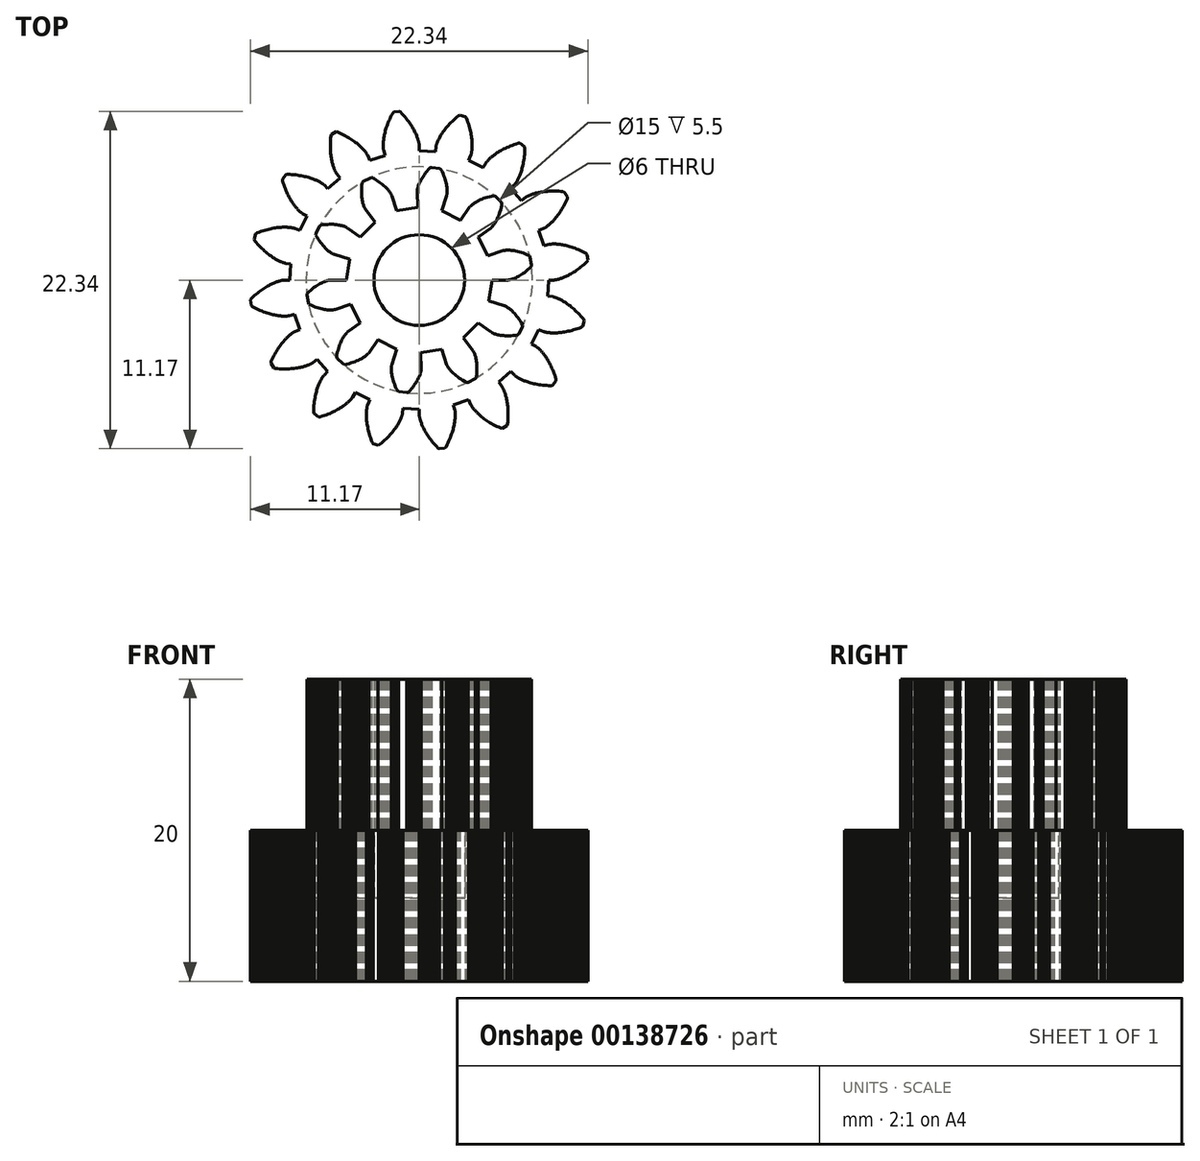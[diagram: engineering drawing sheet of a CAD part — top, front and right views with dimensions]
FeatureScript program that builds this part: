
annotation { "Feature Type Name" : "Feature", "Feature Type Description" : "" }
export const myFeature = defineFeature(function(context is Context, id is Id, definition is map)
    precondition{}
    {
        {
            var Q0;
            Q0=qCreatedBy(makeId("Top.planeOp"),FACE);
            var sketch = newSketch(context, id + "F0", { "sketchPlane" : qUnion([Q0])});
            skLineSegment(sketch, "E0", {"start": v(8.56, 0) * mm, "end": v(8.91, 0) * mm});
            skLineSegment(sketch, "E1", {"start": v(8.91, 0) * mm, "end": v(8.92, 0) * mm});
            skLineSegment(sketch, "E2", {"start": v(8.92, 0) * mm, "end": v(8.93, 0) * mm});
            skLineSegment(sketch, "E3", {"start": v(8.93, 0) * mm, "end": v(8.94, 0) * mm});
            skLineSegment(sketch, "E4", {"start": v(8.94, 0) * mm, "end": v(8.96, 0) * mm});
            skLineSegment(sketch, "E5", {"start": v(8.96, 0) * mm, "end": v(8.98, 0) * mm});
            skLineSegment(sketch, "E6", {"start": v(8.98, 0) * mm, "end": v(9, 0) * mm});
            skLineSegment(sketch, "E7", {"start": v(9, 0) * mm, "end": v(9.04, 0.01) * mm});
            skLineSegment(sketch, "E8", {"start": v(9.04, 0.01) * mm, "end": v(9.07, 0.02) * mm});
            skLineSegment(sketch, "E9", {"start": v(9.07, 0.02) * mm, "end": v(9.11, 0.03) * mm});
            skLineSegment(sketch, "E10", {"start": v(9.11, 0.03) * mm, "end": v(9.15, 0.04) * mm});
            skLineSegment(sketch, "E11", {"start": v(9.15, 0.04) * mm, "end": v(9.2, 0.05) * mm});
            skLineSegment(sketch, "E12", {"start": v(9.2, 0.05) * mm, "end": v(9.25, 0.06) * mm});
            skLineSegment(sketch, "E13", {"start": v(9.25, 0.06) * mm, "end": v(9.3, 0.08) * mm});
            skLineSegment(sketch, "E14", {"start": v(9.3, 0.08) * mm, "end": v(9.36, 0.1) * mm});
            skLineSegment(sketch, "E15", {"start": v(9.36, 0.1) * mm, "end": v(9.42, 0.12) * mm});
            skLineSegment(sketch, "E16", {"start": v(9.42, 0.12) * mm, "end": v(9.49, 0.14) * mm});
            skLineSegment(sketch, "E17", {"start": v(9.49, 0.14) * mm, "end": v(9.56, 0.17) * mm});
            skLineSegment(sketch, "E18", {"start": v(9.56, 0.17) * mm, "end": v(9.63, 0.2) * mm});
            skLineSegment(sketch, "E19", {"start": v(9.63, 0.2) * mm, "end": v(9.7, 0.23) * mm});
            skLineSegment(sketch, "E20", {"start": v(9.7, 0.23) * mm, "end": v(9.78, 0.27) * mm});
            skLineSegment(sketch, "E21", {"start": v(9.78, 0.27) * mm, "end": v(9.86, 0.31) * mm});
            skLineSegment(sketch, "E22", {"start": v(9.86, 0.31) * mm, "end": v(9.95, 0.36) * mm});
            skLineSegment(sketch, "E23", {"start": v(9.95, 0.36) * mm, "end": v(10.03, 0.4) * mm});
            skLineSegment(sketch, "E24", {"start": v(10.03, 0.4) * mm, "end": v(10.12, 0.46) * mm});
            skLineSegment(sketch, "E25", {"start": v(10.12, 0.46) * mm, "end": v(10.21, 0.51) * mm});
            skLineSegment(sketch, "E26", {"start": v(10.21, 0.51) * mm, "end": v(10.3, 0.57) * mm});
            skLineSegment(sketch, "E27", {"start": v(10.3, 0.57) * mm, "end": v(10.4, 0.64) * mm});
            skLineSegment(sketch, "E28", {"start": v(10.4, 0.64) * mm, "end": v(10.5, 0.7) * mm});
            skLineSegment(sketch, "E29", {"start": v(10.5, 0.7) * mm, "end": v(10.6, 0.78) * mm});
            skLineSegment(sketch, "E30", {"start": v(10.6, 0.78) * mm, "end": v(10.7, 0.86) * mm});
            skLineSegment(sketch, "E31", {"start": v(10.7, 0.86) * mm, "end": v(10.8, 0.94) * mm});
            skLineSegment(sketch, "E32", {"start": v(10.8, 0.94) * mm, "end": v(10.9, 1.03) * mm});
            skLineSegment(sketch, "E33", {"start": v(10.9, 1.03) * mm, "end": v(11.01, 1.13) * mm});
            skLineSegment(sketch, "E34", {"start": v(11.01, 1.13) * mm, "end": v(11.12, 1.23) * mm});
            skLineSegment(sketch, "E35", {"start": v(11.12, 1.23) * mm, "end": v(11.17, 1.32) * mm});
            skLineSegment(sketch, "E36", {"start": v(11.17, 1.32) * mm, "end": v(11.12, 1.68) * mm});
            skLineSegment(sketch, "E37", {"start": v(11.12, 1.68) * mm, "end": v(11.05, 1.76) * mm});
            skLineSegment(sketch, "E38", {"start": v(11.05, 1.76) * mm, "end": v(10.92, 1.83) * mm});
            skLineSegment(sketch, "E39", {"start": v(10.92, 1.83) * mm, "end": v(10.8, 1.9) * mm});
            skLineSegment(sketch, "E40", {"start": v(10.8, 1.9) * mm, "end": v(10.67, 1.95) * mm});
            skLineSegment(sketch, "E41", {"start": v(10.67, 1.95) * mm, "end": v(10.55, 2) * mm});
            skLineSegment(sketch, "E42", {"start": v(10.55, 2) * mm, "end": v(10.43, 2.05) * mm});
            skLineSegment(sketch, "E43", {"start": v(10.43, 2.05) * mm, "end": v(10.31, 2.1) * mm});
            skLineSegment(sketch, "E44", {"start": v(10.31, 2.1) * mm, "end": v(10.2, 2.14) * mm});
            skLineSegment(sketch, "E45", {"start": v(10.2, 2.14) * mm, "end": v(10.09, 2.18) * mm});
            skLineSegment(sketch, "E46", {"start": v(10.09, 2.18) * mm, "end": v(9.98, 2.2) * mm});
            skLineSegment(sketch, "E47", {"start": v(9.98, 2.2) * mm, "end": v(9.88, 2.24) * mm});
            skLineSegment(sketch, "E48", {"start": v(9.88, 2.24) * mm, "end": v(9.78, 2.27) * mm});
            skLineSegment(sketch, "E49", {"start": v(9.78, 2.27) * mm, "end": v(9.68, 2.29) * mm});
            skLineSegment(sketch, "E50", {"start": v(9.68, 2.29) * mm, "end": v(9.6, 2.31) * mm});
            skLineSegment(sketch, "E51", {"start": v(9.6, 2.31) * mm, "end": v(9.5, 2.33) * mm});
            skLineSegment(sketch, "E52", {"start": v(9.5, 2.33) * mm, "end": v(9.42, 2.34) * mm});
            skLineSegment(sketch, "E53", {"start": v(9.42, 2.34) * mm, "end": v(9.34, 2.36) * mm});
            skLineSegment(sketch, "E54", {"start": v(9.34, 2.36) * mm, "end": v(9.26, 2.37) * mm});
            skLineSegment(sketch, "E55", {"start": v(9.26, 2.37) * mm, "end": v(9.19, 2.37) * mm});
            skLineSegment(sketch, "E56", {"start": v(9.19, 2.37) * mm, "end": v(9.12, 2.38) * mm});
            skLineSegment(sketch, "E57", {"start": v(9.12, 2.38) * mm, "end": v(9.05, 2.38) * mm});
            skLineSegment(sketch, "E58", {"start": v(9.05, 2.38) * mm, "end": v(9, 2.39) * mm});
            skLineSegment(sketch, "E59", {"start": v(9, 2.39) * mm, "end": v(8.94, 2.39) * mm});
            skLineSegment(sketch, "E60", {"start": v(8.94, 2.39) * mm, "end": v(8.89, 2.39) * mm});
            skLineSegment(sketch, "E61", {"start": v(8.89, 2.39) * mm, "end": v(8.84, 2.39) * mm});
            skLineSegment(sketch, "E62", {"start": v(8.84, 2.39) * mm, "end": v(8.8, 2.39) * mm});
            skLineSegment(sketch, "E63", {"start": v(8.8, 2.39) * mm, "end": v(8.75, 2.38) * mm});
            skLineSegment(sketch, "E64", {"start": v(8.75, 2.38) * mm, "end": v(8.72, 2.38) * mm});
            skLineSegment(sketch, "E65", {"start": v(8.72, 2.38) * mm, "end": v(8.69, 2.38) * mm});
            skLineSegment(sketch, "E66", {"start": v(8.69, 2.38) * mm, "end": v(8.66, 2.37) * mm});
            skLineSegment(sketch, "E67", {"start": v(8.66, 2.37) * mm, "end": v(8.64, 2.37) * mm});
            skLineSegment(sketch, "E68", {"start": v(8.64, 2.37) * mm, "end": v(8.62, 2.37) * mm});
            skLineSegment(sketch, "E69", {"start": v(8.62, 2.37) * mm, "end": v(8.6, 2.36) * mm});
            skLineSegment(sketch, "E70", {"start": v(8.6, 2.36) * mm, "end": v(8.6, 2.36) * mm});
            skLineSegment(sketch, "E71", {"start": v(8.6, 2.36) * mm, "end": v(8.26, 2.27) * mm});
            skLineSegment(sketch, "E72", {"start": v(8.26, 2.27) * mm, "end": v(7.91, 3.28) * mm});
            skLineSegment(sketch, "E73", {"start": v(7.91, 3.28) * mm, "end": v(8.23, 3.41) * mm});
            skLineSegment(sketch, "E74", {"start": v(8.23, 3.41) * mm, "end": v(8.24, 3.41) * mm});
            skLineSegment(sketch, "E75", {"start": v(8.24, 3.41) * mm, "end": v(8.25, 3.42) * mm});
            skLineSegment(sketch, "E76", {"start": v(8.25, 3.42) * mm, "end": v(8.26, 3.42) * mm});
            skLineSegment(sketch, "E77", {"start": v(8.26, 3.42) * mm, "end": v(8.28, 3.43) * mm});
            skLineSegment(sketch, "E78", {"start": v(8.28, 3.43) * mm, "end": v(8.3, 3.44) * mm});
            skLineSegment(sketch, "E79", {"start": v(8.3, 3.44) * mm, "end": v(8.32, 3.46) * mm});
            skLineSegment(sketch, "E80", {"start": v(8.32, 3.46) * mm, "end": v(8.34, 3.47) * mm});
            skLineSegment(sketch, "E81", {"start": v(8.34, 3.47) * mm, "end": v(8.37, 3.5) * mm});
            skLineSegment(sketch, "E82", {"start": v(8.37, 3.5) * mm, "end": v(8.4, 3.51) * mm});
            skLineSegment(sketch, "E83", {"start": v(8.4, 3.51) * mm, "end": v(8.44, 3.54) * mm});
            skLineSegment(sketch, "E84", {"start": v(8.44, 3.54) * mm, "end": v(8.48, 3.57) * mm});
            skLineSegment(sketch, "E85", {"start": v(8.48, 3.57) * mm, "end": v(8.52, 3.6) * mm});
            skLineSegment(sketch, "E86", {"start": v(8.52, 3.6) * mm, "end": v(8.57, 3.63) * mm});
            skLineSegment(sketch, "E87", {"start": v(8.57, 3.63) * mm, "end": v(8.61, 3.67) * mm});
            skLineSegment(sketch, "E88", {"start": v(8.61, 3.67) * mm, "end": v(8.66, 3.72) * mm});
            skLineSegment(sketch, "E89", {"start": v(8.66, 3.72) * mm, "end": v(8.71, 3.76) * mm});
            skLineSegment(sketch, "E90", {"start": v(8.71, 3.76) * mm, "end": v(8.76, 3.82) * mm});
            skLineSegment(sketch, "E91", {"start": v(8.76, 3.82) * mm, "end": v(8.82, 3.87) * mm});
            skLineSegment(sketch, "E92", {"start": v(8.82, 3.87) * mm, "end": v(8.87, 3.93) * mm});
            skLineSegment(sketch, "E93", {"start": v(8.87, 3.93) * mm, "end": v(8.93, 4) * mm});
            skLineSegment(sketch, "E94", {"start": v(8.93, 4) * mm, "end": v(9, 4.06) * mm});
            skLineSegment(sketch, "E95", {"start": v(9, 4.06) * mm, "end": v(9.05, 4.14) * mm});
            skLineSegment(sketch, "E96", {"start": v(9.05, 4.14) * mm, "end": v(9.11, 4.21) * mm});
            skLineSegment(sketch, "E97", {"start": v(9.11, 4.21) * mm, "end": v(9.18, 4.3) * mm});
            skLineSegment(sketch, "E98", {"start": v(9.18, 4.3) * mm, "end": v(9.24, 4.38) * mm});
            skLineSegment(sketch, "E99", {"start": v(9.24, 4.38) * mm, "end": v(9.3, 4.47) * mm});
            skLineSegment(sketch, "E100", {"start": v(9.3, 4.47) * mm, "end": v(9.37, 4.57) * mm});
            skLineSegment(sketch, "E101", {"start": v(9.37, 4.57) * mm, "end": v(9.43, 4.67) * mm});
            skLineSegment(sketch, "E102", {"start": v(9.43, 4.67) * mm, "end": v(9.5, 4.78) * mm});
            skLineSegment(sketch, "E103", {"start": v(9.5, 4.78) * mm, "end": v(9.56, 4.9) * mm});
            skLineSegment(sketch, "E104", {"start": v(9.56, 4.9) * mm, "end": v(9.62, 5) * mm});
            skLineSegment(sketch, "E105", {"start": v(9.62, 5) * mm, "end": v(9.68, 5.13) * mm});
            skLineSegment(sketch, "E106", {"start": v(9.68, 5.13) * mm, "end": v(9.74, 5.26) * mm});
            skLineSegment(sketch, "E107", {"start": v(9.74, 5.26) * mm, "end": v(9.8, 5.39) * mm});
            skLineSegment(sketch, "E108", {"start": v(9.8, 5.39) * mm, "end": v(9.81, 5.5) * mm});
            skLineSegment(sketch, "E109", {"start": v(9.81, 5.5) * mm, "end": v(9.63, 5.81) * mm});
            skLineSegment(sketch, "E110", {"start": v(9.63, 5.81) * mm, "end": v(9.53, 5.86) * mm});
            skLineSegment(sketch, "E111", {"start": v(9.53, 5.86) * mm, "end": v(9.39, 5.87) * mm});
            skLineSegment(sketch, "E112", {"start": v(9.39, 5.87) * mm, "end": v(9.25, 5.88) * mm});
            skLineSegment(sketch, "E113", {"start": v(9.25, 5.88) * mm, "end": v(9.1, 5.88) * mm});
            skLineSegment(sketch, "E114", {"start": v(9.1, 5.88) * mm, "end": v(8.98, 5.89) * mm});
            skLineSegment(sketch, "E115", {"start": v(8.98, 5.89) * mm, "end": v(8.85, 5.89) * mm});
            skLineSegment(sketch, "E116", {"start": v(8.85, 5.89) * mm, "end": v(8.72, 5.88) * mm});
            skLineSegment(sketch, "E117", {"start": v(8.72, 5.88) * mm, "end": v(8.6, 5.88) * mm});
            skLineSegment(sketch, "E118", {"start": v(8.6, 5.88) * mm, "end": v(8.49, 5.87) * mm});
            skLineSegment(sketch, "E119", {"start": v(8.49, 5.87) * mm, "end": v(8.38, 5.86) * mm});
            skLineSegment(sketch, "E120", {"start": v(8.38, 5.86) * mm, "end": v(8.27, 5.85) * mm});
            skLineSegment(sketch, "E121", {"start": v(8.27, 5.85) * mm, "end": v(8.17, 5.84) * mm});
            skLineSegment(sketch, "E122", {"start": v(8.17, 5.84) * mm, "end": v(8.07, 5.82) * mm});
            skLineSegment(sketch, "E123", {"start": v(8.07, 5.82) * mm, "end": v(7.98, 5.8) * mm});
            skLineSegment(sketch, "E124", {"start": v(7.98, 5.8) * mm, "end": v(7.89, 5.79) * mm});
            skLineSegment(sketch, "E125", {"start": v(7.89, 5.79) * mm, "end": v(7.8, 5.77) * mm});
            skLineSegment(sketch, "E126", {"start": v(7.8, 5.77) * mm, "end": v(7.73, 5.75) * mm});
            skLineSegment(sketch, "E127", {"start": v(7.73, 5.75) * mm, "end": v(7.65, 5.73) * mm});
            skLineSegment(sketch, "E128", {"start": v(7.65, 5.73) * mm, "end": v(7.58, 5.7) * mm});
            skLineSegment(sketch, "E129", {"start": v(7.58, 5.7) * mm, "end": v(7.51, 5.69) * mm});
            skLineSegment(sketch, "E130", {"start": v(7.51, 5.69) * mm, "end": v(7.45, 5.67) * mm});
            skLineSegment(sketch, "E131", {"start": v(7.45, 5.67) * mm, "end": v(7.4, 5.65) * mm});
            skLineSegment(sketch, "E132", {"start": v(7.4, 5.65) * mm, "end": v(7.34, 5.63) * mm});
            skLineSegment(sketch, "E133", {"start": v(7.34, 5.63) * mm, "end": v(7.3, 5.6) * mm});
            skLineSegment(sketch, "E134", {"start": v(7.3, 5.6) * mm, "end": v(7.25, 5.59) * mm});
            skLineSegment(sketch, "E135", {"start": v(7.25, 5.59) * mm, "end": v(7.21, 5.57) * mm});
            skLineSegment(sketch, "E136", {"start": v(7.21, 5.57) * mm, "end": v(7.18, 5.55) * mm});
            skLineSegment(sketch, "E137", {"start": v(7.18, 5.55) * mm, "end": v(7.15, 5.54) * mm});
            skLineSegment(sketch, "E138", {"start": v(7.15, 5.54) * mm, "end": v(7.12, 5.52) * mm});
            skLineSegment(sketch, "E139", {"start": v(7.12, 5.52) * mm, "end": v(7.1, 5.5) * mm});
            skLineSegment(sketch, "E140", {"start": v(7.1, 5.5) * mm, "end": v(7.08, 5.5) * mm});
            skLineSegment(sketch, "E141", {"start": v(7.08, 5.5) * mm, "end": v(7.06, 5.49) * mm});
            skLineSegment(sketch, "E142", {"start": v(7.06, 5.49) * mm, "end": v(7.05, 5.48) * mm});
            skLineSegment(sketch, "E143", {"start": v(7.05, 5.48) * mm, "end": v(7.04, 5.47) * mm});
            skLineSegment(sketch, "E144", {"start": v(7.04, 5.47) * mm, "end": v(7.04, 5.47) * mm});
            skLineSegment(sketch, "E145", {"start": v(7.04, 5.47) * mm, "end": v(6.76, 5.25) * mm});
            skLineSegment(sketch, "E146", {"start": v(6.76, 5.25) * mm, "end": v(6.05, 6.05) * mm});
            skLineSegment(sketch, "E147", {"start": v(6.05, 6.05) * mm, "end": v(6.3, 6.3) * mm});
            skLineSegment(sketch, "E148", {"start": v(6.3, 6.3) * mm, "end": v(6.3, 6.3) * mm});
            skLineSegment(sketch, "E149", {"start": v(6.3, 6.3) * mm, "end": v(6.31, 6.31) * mm});
            skLineSegment(sketch, "E150", {"start": v(6.31, 6.31) * mm, "end": v(6.32, 6.32) * mm});
            skLineSegment(sketch, "E151", {"start": v(6.32, 6.32) * mm, "end": v(6.33, 6.34) * mm});
            skLineSegment(sketch, "E152", {"start": v(6.33, 6.34) * mm, "end": v(6.35, 6.35) * mm});
            skLineSegment(sketch, "E153", {"start": v(6.35, 6.35) * mm, "end": v(6.36, 6.38) * mm});
            skLineSegment(sketch, "E154", {"start": v(6.36, 6.38) * mm, "end": v(6.38, 6.4) * mm});
            skLineSegment(sketch, "E155", {"start": v(6.38, 6.4) * mm, "end": v(6.4, 6.43) * mm});
            skLineSegment(sketch, "E156", {"start": v(6.4, 6.43) * mm, "end": v(6.42, 6.46) * mm});
            skLineSegment(sketch, "E157", {"start": v(6.42, 6.46) * mm, "end": v(6.45, 6.5) * mm});
            skLineSegment(sketch, "E158", {"start": v(6.45, 6.5) * mm, "end": v(6.47, 6.54) * mm});
            skLineSegment(sketch, "E159", {"start": v(6.47, 6.54) * mm, "end": v(6.5, 6.59) * mm});
            skLineSegment(sketch, "E160", {"start": v(6.5, 6.59) * mm, "end": v(6.52, 6.64) * mm});
            skLineSegment(sketch, "E161", {"start": v(6.52, 6.64) * mm, "end": v(6.55, 6.7) * mm});
            skLineSegment(sketch, "E162", {"start": v(6.55, 6.7) * mm, "end": v(6.58, 6.75) * mm});
            skLineSegment(sketch, "E163", {"start": v(6.58, 6.75) * mm, "end": v(6.6, 6.81) * mm});
            skLineSegment(sketch, "E164", {"start": v(6.6, 6.81) * mm, "end": v(6.64, 6.88) * mm});
            skLineSegment(sketch, "E165", {"start": v(6.64, 6.88) * mm, "end": v(6.67, 6.95) * mm});
            skLineSegment(sketch, "E166", {"start": v(6.67, 6.95) * mm, "end": v(6.7, 7.03) * mm});
            skLineSegment(sketch, "E167", {"start": v(6.7, 7.03) * mm, "end": v(6.72, 7.1) * mm});
            skLineSegment(sketch, "E168", {"start": v(6.72, 7.1) * mm, "end": v(6.75, 7.2) * mm});
            skLineSegment(sketch, "E169", {"start": v(6.75, 7.2) * mm, "end": v(6.78, 7.28) * mm});
            skLineSegment(sketch, "E170", {"start": v(6.78, 7.28) * mm, "end": v(6.8, 7.38) * mm});
            skLineSegment(sketch, "E171", {"start": v(6.8, 7.38) * mm, "end": v(6.83, 7.48) * mm});
            skLineSegment(sketch, "E172", {"start": v(6.83, 7.48) * mm, "end": v(6.86, 7.58) * mm});
            skLineSegment(sketch, "E173", {"start": v(6.86, 7.58) * mm, "end": v(6.88, 7.7) * mm});
            skLineSegment(sketch, "E174", {"start": v(6.88, 7.7) * mm, "end": v(6.9, 7.8) * mm});
            skLineSegment(sketch, "E175", {"start": v(6.9, 7.8) * mm, "end": v(6.92, 7.92) * mm});
            skLineSegment(sketch, "E176", {"start": v(6.92, 7.92) * mm, "end": v(6.94, 8.05) * mm});
            skLineSegment(sketch, "E177", {"start": v(6.94, 8.05) * mm, "end": v(6.96, 8.18) * mm});
            skLineSegment(sketch, "E178", {"start": v(6.96, 8.18) * mm, "end": v(6.97, 8.3) * mm});
            skLineSegment(sketch, "E179", {"start": v(6.97, 8.3) * mm, "end": v(6.98, 8.44) * mm});
            skLineSegment(sketch, "E180", {"start": v(6.98, 8.44) * mm, "end": v(7, 8.58) * mm});
            skLineSegment(sketch, "E181", {"start": v(7, 8.58) * mm, "end": v(7, 8.73) * mm});
            skLineSegment(sketch, "E182", {"start": v(7, 8.73) * mm, "end": v(6.96, 8.84) * mm});
            skLineSegment(sketch, "E183", {"start": v(6.96, 8.84) * mm, "end": v(6.68, 9.05) * mm});
            skLineSegment(sketch, "E184", {"start": v(6.68, 9.05) * mm, "end": v(6.57, 9.06) * mm});
            skLineSegment(sketch, "E185", {"start": v(6.57, 9.06) * mm, "end": v(6.43, 9.01) * mm});
            skLineSegment(sketch, "E186", {"start": v(6.43, 9.01) * mm, "end": v(6.3, 8.97) * mm});
            skLineSegment(sketch, "E187", {"start": v(6.3, 8.97) * mm, "end": v(6.16, 8.92) * mm});
            skLineSegment(sketch, "E188", {"start": v(6.16, 8.92) * mm, "end": v(6.04, 8.87) * mm});
            skLineSegment(sketch, "E189", {"start": v(6.04, 8.87) * mm, "end": v(5.92, 8.82) * mm});
            skLineSegment(sketch, "E190", {"start": v(5.92, 8.82) * mm, "end": v(5.8, 8.77) * mm});
            skLineSegment(sketch, "E191", {"start": v(5.8, 8.77) * mm, "end": v(5.7, 8.72) * mm});
            skLineSegment(sketch, "E192", {"start": v(5.7, 8.72) * mm, "end": v(5.6, 8.67) * mm});
            skLineSegment(sketch, "E193", {"start": v(5.6, 8.67) * mm, "end": v(5.5, 8.62) * mm});
            skLineSegment(sketch, "E194", {"start": v(5.5, 8.62) * mm, "end": v(5.4, 8.57) * mm});
            skLineSegment(sketch, "E195", {"start": v(5.4, 8.57) * mm, "end": v(5.31, 8.52) * mm});
            skLineSegment(sketch, "E196", {"start": v(5.31, 8.52) * mm, "end": v(5.23, 8.47) * mm});
            skLineSegment(sketch, "E197", {"start": v(5.23, 8.47) * mm, "end": v(5.15, 8.42) * mm});
            skLineSegment(sketch, "E198", {"start": v(5.15, 8.42) * mm, "end": v(5.07, 8.37) * mm});
            skLineSegment(sketch, "E199", {"start": v(5.07, 8.37) * mm, "end": v(5, 8.32) * mm});
            skLineSegment(sketch, "E200", {"start": v(5, 8.32) * mm, "end": v(4.94, 8.27) * mm});
            skLineSegment(sketch, "E201", {"start": v(4.94, 8.27) * mm, "end": v(4.88, 8.22) * mm});
            skLineSegment(sketch, "E202", {"start": v(4.88, 8.22) * mm, "end": v(4.82, 8.18) * mm});
            skLineSegment(sketch, "E203", {"start": v(4.82, 8.18) * mm, "end": v(4.77, 8.13) * mm});
            skLineSegment(sketch, "E204", {"start": v(4.77, 8.13) * mm, "end": v(4.72, 8.09) * mm});
            skLineSegment(sketch, "E205", {"start": v(4.72, 8.09) * mm, "end": v(4.67, 8.05) * mm});
            skLineSegment(sketch, "E206", {"start": v(4.67, 8.05) * mm, "end": v(4.63, 8) * mm});
            skLineSegment(sketch, "E207", {"start": v(4.63, 8) * mm, "end": v(4.6, 7.97) * mm});
            skLineSegment(sketch, "E208", {"start": v(4.6, 7.97) * mm, "end": v(4.56, 7.94) * mm});
            skLineSegment(sketch, "E209", {"start": v(4.56, 7.94) * mm, "end": v(4.53, 7.9) * mm});
            skLineSegment(sketch, "E210", {"start": v(4.53, 7.9) * mm, "end": v(4.5, 7.87) * mm});
            skLineSegment(sketch, "E211", {"start": v(4.5, 7.87) * mm, "end": v(4.48, 7.85) * mm});
            skLineSegment(sketch, "E212", {"start": v(4.48, 7.85) * mm, "end": v(4.46, 7.82) * mm});
            skLineSegment(sketch, "E213", {"start": v(4.46, 7.82) * mm, "end": v(4.45, 7.8) * mm});
            skLineSegment(sketch, "E214", {"start": v(4.45, 7.8) * mm, "end": v(4.43, 7.78) * mm});
            skLineSegment(sketch, "E215", {"start": v(4.43, 7.78) * mm, "end": v(4.42, 7.77) * mm});
            skLineSegment(sketch, "E216", {"start": v(4.42, 7.77) * mm, "end": v(4.42, 7.76) * mm});
            skLineSegment(sketch, "E217", {"start": v(4.42, 7.76) * mm, "end": v(4.41, 7.75) * mm});
            skLineSegment(sketch, "E218", {"start": v(4.41, 7.75) * mm, "end": v(4.4, 7.75) * mm});
            skLineSegment(sketch, "E219", {"start": v(4.4, 7.75) * mm, "end": v(4.24, 7.44) * mm});
            skLineSegment(sketch, "E220", {"start": v(4.24, 7.44) * mm, "end": v(3.28, 7.91) * mm});
            skLineSegment(sketch, "E221", {"start": v(3.28, 7.91) * mm, "end": v(3.41, 8.23) * mm});
            skLineSegment(sketch, "E222", {"start": v(3.41, 8.23) * mm, "end": v(3.41, 8.24) * mm});
            skLineSegment(sketch, "E223", {"start": v(3.41, 8.24) * mm, "end": v(3.42, 8.25) * mm});
            skLineSegment(sketch, "E224", {"start": v(3.42, 8.25) * mm, "end": v(3.42, 8.26) * mm});
            skLineSegment(sketch, "E225", {"start": v(3.42, 8.26) * mm, "end": v(3.43, 8.28) * mm});
            skLineSegment(sketch, "E226", {"start": v(3.43, 8.28) * mm, "end": v(3.43, 8.3) * mm});
            skLineSegment(sketch, "E227", {"start": v(3.43, 8.3) * mm, "end": v(3.44, 8.33) * mm});
            skLineSegment(sketch, "E228", {"start": v(3.44, 8.33) * mm, "end": v(3.45, 8.36) * mm});
            skLineSegment(sketch, "E229", {"start": v(3.45, 8.36) * mm, "end": v(3.45, 8.4) * mm});
            skLineSegment(sketch, "E230", {"start": v(3.45, 8.4) * mm, "end": v(3.46, 8.43) * mm});
            skLineSegment(sketch, "E231", {"start": v(3.46, 8.43) * mm, "end": v(3.47, 8.47) * mm});
            skLineSegment(sketch, "E232", {"start": v(3.47, 8.47) * mm, "end": v(3.47, 8.52) * mm});
            skLineSegment(sketch, "E233", {"start": v(3.47, 8.52) * mm, "end": v(3.48, 8.57) * mm});
            skLineSegment(sketch, "E234", {"start": v(3.48, 8.57) * mm, "end": v(3.49, 8.63) * mm});
            skLineSegment(sketch, "E235", {"start": v(3.49, 8.63) * mm, "end": v(3.5, 8.69) * mm});
            skLineSegment(sketch, "E236", {"start": v(3.5, 8.69) * mm, "end": v(3.5, 8.75) * mm});
            skLineSegment(sketch, "E237", {"start": v(3.5, 8.75) * mm, "end": v(3.5, 8.82) * mm});
            skLineSegment(sketch, "E238", {"start": v(3.5, 8.82) * mm, "end": v(3.5, 8.9) * mm});
            skLineSegment(sketch, "E239", {"start": v(3.5, 8.9) * mm, "end": v(3.5, 8.97) * mm});
            skLineSegment(sketch, "E240", {"start": v(3.5, 8.97) * mm, "end": v(3.5, 9.05) * mm});
            skLineSegment(sketch, "E241", {"start": v(3.5, 9.05) * mm, "end": v(3.5, 9.14) * mm});
            skLineSegment(sketch, "E242", {"start": v(3.5, 9.14) * mm, "end": v(3.49, 9.23) * mm});
            skLineSegment(sketch, "E243", {"start": v(3.49, 9.23) * mm, "end": v(3.48, 9.32) * mm});
            skLineSegment(sketch, "E244", {"start": v(3.48, 9.32) * mm, "end": v(3.47, 9.42) * mm});
            skLineSegment(sketch, "E245", {"start": v(3.47, 9.42) * mm, "end": v(3.45, 9.52) * mm});
            skLineSegment(sketch, "E246", {"start": v(3.45, 9.52) * mm, "end": v(3.43, 9.63) * mm});
            skLineSegment(sketch, "E247", {"start": v(3.43, 9.63) * mm, "end": v(3.41, 9.74) * mm});
            skLineSegment(sketch, "E248", {"start": v(3.41, 9.74) * mm, "end": v(3.4, 9.85) * mm});
            skLineSegment(sketch, "E249", {"start": v(3.4, 9.85) * mm, "end": v(3.36, 9.97) * mm});
            skLineSegment(sketch, "E250", {"start": v(3.36, 9.97) * mm, "end": v(3.33, 10.1) * mm});
            skLineSegment(sketch, "E251", {"start": v(3.33, 10.1) * mm, "end": v(3.3, 10.22) * mm});
            skLineSegment(sketch, "E252", {"start": v(3.3, 10.22) * mm, "end": v(3.26, 10.34) * mm});
            skLineSegment(sketch, "E253", {"start": v(3.26, 10.34) * mm, "end": v(3.22, 10.47) * mm});
            skLineSegment(sketch, "E254", {"start": v(3.22, 10.47) * mm, "end": v(3.17, 10.6) * mm});
            skLineSegment(sketch, "E255", {"start": v(3.17, 10.6) * mm, "end": v(3.12, 10.74) * mm});
            skLineSegment(sketch, "E256", {"start": v(3.12, 10.74) * mm, "end": v(3.05, 10.83) * mm});
            skLineSegment(sketch, "E257", {"start": v(3.05, 10.83) * mm, "end": v(2.7, 10.92) * mm});
            skLineSegment(sketch, "E258", {"start": v(2.7, 10.92) * mm, "end": v(2.6, 10.88) * mm});
            skLineSegment(sketch, "E259", {"start": v(2.6, 10.88) * mm, "end": v(2.49, 10.79) * mm});
            skLineSegment(sketch, "E260", {"start": v(2.49, 10.79) * mm, "end": v(2.38, 10.7) * mm});
            skLineSegment(sketch, "E261", {"start": v(2.38, 10.7) * mm, "end": v(2.28, 10.6) * mm});
            skLineSegment(sketch, "E262", {"start": v(2.28, 10.6) * mm, "end": v(2.18, 10.51) * mm});
            skLineSegment(sketch, "E263", {"start": v(2.18, 10.51) * mm, "end": v(2.1, 10.42) * mm});
            skLineSegment(sketch, "E264", {"start": v(2.1, 10.42) * mm, "end": v(2, 10.33) * mm});
            skLineSegment(sketch, "E265", {"start": v(2, 10.33) * mm, "end": v(1.93, 10.24) * mm});
            skLineSegment(sketch, "E266", {"start": v(1.93, 10.24) * mm, "end": v(1.85, 10.15) * mm});
            skLineSegment(sketch, "E267", {"start": v(1.85, 10.15) * mm, "end": v(1.78, 10.07) * mm});
            skLineSegment(sketch, "E268", {"start": v(1.78, 10.07) * mm, "end": v(1.71, 9.98) * mm});
            skLineSegment(sketch, "E269", {"start": v(1.71, 9.98) * mm, "end": v(1.65, 9.9) * mm});
            skLineSegment(sketch, "E270", {"start": v(1.65, 9.9) * mm, "end": v(1.6, 9.82) * mm});
            skLineSegment(sketch, "E271", {"start": v(1.6, 9.82) * mm, "end": v(1.54, 9.75) * mm});
            skLineSegment(sketch, "E272", {"start": v(1.54, 9.75) * mm, "end": v(1.49, 9.67) * mm});
            skLineSegment(sketch, "E273", {"start": v(1.49, 9.67) * mm, "end": v(1.44, 9.6) * mm});
            skLineSegment(sketch, "E274", {"start": v(1.44, 9.6) * mm, "end": v(1.4, 9.53) * mm});
            skLineSegment(sketch, "E275", {"start": v(1.4, 9.53) * mm, "end": v(1.36, 9.46) * mm});
            skLineSegment(sketch, "E276", {"start": v(1.36, 9.46) * mm, "end": v(1.32, 9.4) * mm});
            skLineSegment(sketch, "E277", {"start": v(1.32, 9.4) * mm, "end": v(1.3, 9.34) * mm});
            skLineSegment(sketch, "E278", {"start": v(1.3, 9.34) * mm, "end": v(1.26, 9.28) * mm});
            skLineSegment(sketch, "E279", {"start": v(1.26, 9.28) * mm, "end": v(1.24, 9.22) * mm});
            skLineSegment(sketch, "E280", {"start": v(1.24, 9.22) * mm, "end": v(1.21, 9.17) * mm});
            skLineSegment(sketch, "E281", {"start": v(1.21, 9.17) * mm, "end": v(1.2, 9.12) * mm});
            skLineSegment(sketch, "E282", {"start": v(1.2, 9.12) * mm, "end": v(1.18, 9.08) * mm});
            skLineSegment(sketch, "E283", {"start": v(1.18, 9.08) * mm, "end": v(1.16, 9.04) * mm});
            skLineSegment(sketch, "E284", {"start": v(1.16, 9.04) * mm, "end": v(1.15, 9) * mm});
            skLineSegment(sketch, "E285", {"start": v(1.15, 9) * mm, "end": v(1.14, 8.97) * mm});
            skLineSegment(sketch, "E286", {"start": v(1.14, 8.97) * mm, "end": v(1.13, 8.94) * mm});
            skLineSegment(sketch, "E287", {"start": v(1.13, 8.94) * mm, "end": v(1.12, 8.91) * mm});
            skLineSegment(sketch, "E288", {"start": v(1.12, 8.91) * mm, "end": v(1.12, 8.89) * mm});
            skLineSegment(sketch, "E289", {"start": v(1.12, 8.89) * mm, "end": v(1.11, 8.87) * mm});
            skLineSegment(sketch, "E290", {"start": v(1.11, 8.87) * mm, "end": v(1.11, 8.86) * mm});
            skLineSegment(sketch, "E291", {"start": v(1.11, 8.86) * mm, "end": v(1.1, 8.85) * mm});
            skLineSegment(sketch, "E292", {"start": v(1.1, 8.85) * mm, "end": v(1.1, 8.84) * mm});
            skLineSegment(sketch, "E293", {"start": v(1.1, 8.84) * mm, "end": v(1.06, 8.5) * mm});
            skLineSegment(sketch, "E294", {"start": v(1.06, 8.5) * mm, "end": v(0, 8.56) * mm});
            skLineSegment(sketch, "E295", {"start": v(0, 8.56) * mm, "end": v(0, 8.91) * mm});
            skLineSegment(sketch, "E296", {"start": v(0, 8.91) * mm, "end": v(0, 8.92) * mm});
            skLineSegment(sketch, "E297", {"start": v(0, 8.92) * mm, "end": v(0, 8.93) * mm});
            skLineSegment(sketch, "E298", {"start": v(0, 8.93) * mm, "end": v(0, 8.94) * mm});
            skLineSegment(sketch, "E299", {"start": v(0, 8.94) * mm, "end": v(0, 8.96) * mm});
            skLineSegment(sketch, "E300", {"start": v(0, 8.96) * mm, "end": v(0, 8.98) * mm});
            skLineSegment(sketch, "E301", {"start": v(0, 8.98) * mm, "end": v(0, 9) * mm});
            skLineSegment(sketch, "E302", {"start": v(0, 9) * mm, "end": v(-0.01, 9.04) * mm});
            skLineSegment(sketch, "E303", {"start": v(-0.01, 9.04) * mm, "end": v(-0.02, 9.07) * mm});
            skLineSegment(sketch, "E304", {"start": v(-0.02, 9.07) * mm, "end": v(-0.03, 9.11) * mm});
            skLineSegment(sketch, "E305", {"start": v(-0.03, 9.11) * mm, "end": v(-0.04, 9.15) * mm});
            skLineSegment(sketch, "E306", {"start": v(-0.04, 9.15) * mm, "end": v(-0.05, 9.2) * mm});
            skLineSegment(sketch, "E307", {"start": v(-0.05, 9.2) * mm, "end": v(-0.06, 9.25) * mm});
            skLineSegment(sketch, "E308", {"start": v(-0.06, 9.25) * mm, "end": v(-0.08, 9.3) * mm});
            skLineSegment(sketch, "E309", {"start": v(-0.08, 9.3) * mm, "end": v(-0.1, 9.36) * mm});
            skLineSegment(sketch, "E310", {"start": v(-0.1, 9.36) * mm, "end": v(-0.12, 9.42) * mm});
            skLineSegment(sketch, "E311", {"start": v(-0.12, 9.42) * mm, "end": v(-0.14, 9.49) * mm});
            skLineSegment(sketch, "E312", {"start": v(-0.14, 9.49) * mm, "end": v(-0.17, 9.56) * mm});
            skLineSegment(sketch, "E313", {"start": v(-0.17, 9.56) * mm, "end": v(-0.2, 9.63) * mm});
            skLineSegment(sketch, "E314", {"start": v(-0.2, 9.63) * mm, "end": v(-0.23, 9.7) * mm});
            skLineSegment(sketch, "E315", {"start": v(-0.23, 9.7) * mm, "end": v(-0.27, 9.78) * mm});
            skLineSegment(sketch, "E316", {"start": v(-0.27, 9.78) * mm, "end": v(-0.31, 9.86) * mm});
            skLineSegment(sketch, "E317", {"start": v(-0.31, 9.86) * mm, "end": v(-0.36, 9.95) * mm});
            skLineSegment(sketch, "E318", {"start": v(-0.36, 9.95) * mm, "end": v(-0.4, 10.03) * mm});
            skLineSegment(sketch, "E319", {"start": v(-0.4, 10.03) * mm, "end": v(-0.46, 10.12) * mm});
            skLineSegment(sketch, "E320", {"start": v(-0.46, 10.12) * mm, "end": v(-0.51, 10.21) * mm});
            skLineSegment(sketch, "E321", {"start": v(-0.51, 10.21) * mm, "end": v(-0.57, 10.3) * mm});
            skLineSegment(sketch, "E322", {"start": v(-0.57, 10.3) * mm, "end": v(-0.64, 10.4) * mm});
            skLineSegment(sketch, "E323", {"start": v(-0.64, 10.4) * mm, "end": v(-0.7, 10.5) * mm});
            skLineSegment(sketch, "E324", {"start": v(-0.7, 10.5) * mm, "end": v(-0.78, 10.6) * mm});
            skLineSegment(sketch, "E325", {"start": v(-0.78, 10.6) * mm, "end": v(-0.86, 10.7) * mm});
            skLineSegment(sketch, "E326", {"start": v(-0.86, 10.7) * mm, "end": v(-0.94, 10.8) * mm});
            skLineSegment(sketch, "E327", {"start": v(-0.94, 10.8) * mm, "end": v(-1.03, 10.9) * mm});
            skLineSegment(sketch, "E328", {"start": v(-1.03, 10.9) * mm, "end": v(-1.13, 11.01) * mm});
            skLineSegment(sketch, "E329", {"start": v(-1.13, 11.01) * mm, "end": v(-1.23, 11.12) * mm});
            skLineSegment(sketch, "E330", {"start": v(-1.23, 11.12) * mm, "end": v(-1.32, 11.17) * mm});
            skLineSegment(sketch, "E331", {"start": v(-1.32, 11.17) * mm, "end": v(-1.68, 11.12) * mm});
            skLineSegment(sketch, "E332", {"start": v(-1.68, 11.12) * mm, "end": v(-1.76, 11.05) * mm});
            skLineSegment(sketch, "E333", {"start": v(-1.76, 11.05) * mm, "end": v(-1.83, 10.92) * mm});
            skLineSegment(sketch, "E334", {"start": v(-1.83, 10.92) * mm, "end": v(-1.9, 10.8) * mm});
            skLineSegment(sketch, "E335", {"start": v(-1.9, 10.8) * mm, "end": v(-1.95, 10.67) * mm});
            skLineSegment(sketch, "E336", {"start": v(-1.95, 10.67) * mm, "end": v(-2, 10.55) * mm});
            skLineSegment(sketch, "E337", {"start": v(-2, 10.55) * mm, "end": v(-2.05, 10.43) * mm});
            skLineSegment(sketch, "E338", {"start": v(-2.05, 10.43) * mm, "end": v(-2.1, 10.31) * mm});
            skLineSegment(sketch, "E339", {"start": v(-2.1, 10.31) * mm, "end": v(-2.14, 10.2) * mm});
            skLineSegment(sketch, "E340", {"start": v(-2.14, 10.2) * mm, "end": v(-2.18, 10.09) * mm});
            skLineSegment(sketch, "E341", {"start": v(-2.18, 10.09) * mm, "end": v(-2.2, 9.98) * mm});
            skLineSegment(sketch, "E342", {"start": v(-2.2, 9.98) * mm, "end": v(-2.24, 9.88) * mm});
            skLineSegment(sketch, "E343", {"start": v(-2.24, 9.88) * mm, "end": v(-2.27, 9.78) * mm});
            skLineSegment(sketch, "E344", {"start": v(-2.27, 9.78) * mm, "end": v(-2.29, 9.68) * mm});
            skLineSegment(sketch, "E345", {"start": v(-2.29, 9.68) * mm, "end": v(-2.31, 9.6) * mm});
            skLineSegment(sketch, "E346", {"start": v(-2.31, 9.6) * mm, "end": v(-2.33, 9.5) * mm});
            skLineSegment(sketch, "E347", {"start": v(-2.33, 9.5) * mm, "end": v(-2.34, 9.42) * mm});
            skLineSegment(sketch, "E348", {"start": v(-2.34, 9.42) * mm, "end": v(-2.36, 9.34) * mm});
            skLineSegment(sketch, "E349", {"start": v(-2.36, 9.34) * mm, "end": v(-2.37, 9.26) * mm});
            skLineSegment(sketch, "E350", {"start": v(-2.37, 9.26) * mm, "end": v(-2.37, 9.19) * mm});
            skLineSegment(sketch, "E351", {"start": v(-2.37, 9.19) * mm, "end": v(-2.38, 9.12) * mm});
            skLineSegment(sketch, "E352", {"start": v(-2.38, 9.12) * mm, "end": v(-2.38, 9.05) * mm});
            skLineSegment(sketch, "E353", {"start": v(-2.38, 9.05) * mm, "end": v(-2.39, 9) * mm});
            skLineSegment(sketch, "E354", {"start": v(-2.39, 9) * mm, "end": v(-2.39, 8.94) * mm});
            skLineSegment(sketch, "E355", {"start": v(-2.39, 8.94) * mm, "end": v(-2.39, 8.89) * mm});
            skLineSegment(sketch, "E356", {"start": v(-2.39, 8.89) * mm, "end": v(-2.39, 8.84) * mm});
            skLineSegment(sketch, "E357", {"start": v(-2.39, 8.84) * mm, "end": v(-2.39, 8.8) * mm});
            skLineSegment(sketch, "E358", {"start": v(-2.39, 8.8) * mm, "end": v(-2.38, 8.75) * mm});
            skLineSegment(sketch, "E359", {"start": v(-2.38, 8.75) * mm, "end": v(-2.38, 8.72) * mm});
            skLineSegment(sketch, "E360", {"start": v(-2.38, 8.72) * mm, "end": v(-2.38, 8.69) * mm});
            skLineSegment(sketch, "E361", {"start": v(-2.38, 8.69) * mm, "end": v(-2.37, 8.66) * mm});
            skLineSegment(sketch, "E362", {"start": v(-2.37, 8.66) * mm, "end": v(-2.37, 8.64) * mm});
            skLineSegment(sketch, "E363", {"start": v(-2.37, 8.64) * mm, "end": v(-2.37, 8.62) * mm});
            skLineSegment(sketch, "E364", {"start": v(-2.37, 8.62) * mm, "end": v(-2.36, 8.6) * mm});
            skLineSegment(sketch, "E365", {"start": v(-2.36, 8.6) * mm, "end": v(-2.36, 8.6) * mm});
            skLineSegment(sketch, "E366", {"start": v(-2.36, 8.6) * mm, "end": v(-2.27, 8.26) * mm});
            skLineSegment(sketch, "E367", {"start": v(-2.27, 8.26) * mm, "end": v(-3.28, 7.91) * mm});
            skLineSegment(sketch, "E368", {"start": v(-3.28, 7.91) * mm, "end": v(-3.41, 8.23) * mm});
            skLineSegment(sketch, "E369", {"start": v(-3.41, 8.23) * mm, "end": v(-3.41, 8.24) * mm});
            skLineSegment(sketch, "E370", {"start": v(-3.41, 8.24) * mm, "end": v(-3.42, 8.25) * mm});
            skLineSegment(sketch, "E371", {"start": v(-3.42, 8.25) * mm, "end": v(-3.42, 8.26) * mm});
            skLineSegment(sketch, "E372", {"start": v(-3.42, 8.26) * mm, "end": v(-3.43, 8.28) * mm});
            skLineSegment(sketch, "E373", {"start": v(-3.43, 8.28) * mm, "end": v(-3.44, 8.3) * mm});
            skLineSegment(sketch, "E374", {"start": v(-3.44, 8.3) * mm, "end": v(-3.46, 8.32) * mm});
            skLineSegment(sketch, "E375", {"start": v(-3.46, 8.32) * mm, "end": v(-3.47, 8.34) * mm});
            skLineSegment(sketch, "E376", {"start": v(-3.47, 8.34) * mm, "end": v(-3.5, 8.37) * mm});
            skLineSegment(sketch, "E377", {"start": v(-3.5, 8.37) * mm, "end": v(-3.51, 8.4) * mm});
            skLineSegment(sketch, "E378", {"start": v(-3.51, 8.4) * mm, "end": v(-3.54, 8.44) * mm});
            skLineSegment(sketch, "E379", {"start": v(-3.54, 8.44) * mm, "end": v(-3.57, 8.48) * mm});
            skLineSegment(sketch, "E380", {"start": v(-3.57, 8.48) * mm, "end": v(-3.6, 8.52) * mm});
            skLineSegment(sketch, "E381", {"start": v(-3.6, 8.52) * mm, "end": v(-3.63, 8.57) * mm});
            skLineSegment(sketch, "E382", {"start": v(-3.63, 8.57) * mm, "end": v(-3.67, 8.61) * mm});
            skLineSegment(sketch, "E383", {"start": v(-3.67, 8.61) * mm, "end": v(-3.72, 8.66) * mm});
            skLineSegment(sketch, "E384", {"start": v(-3.72, 8.66) * mm, "end": v(-3.76, 8.71) * mm});
            skLineSegment(sketch, "E385", {"start": v(-3.76, 8.71) * mm, "end": v(-3.82, 8.76) * mm});
            skLineSegment(sketch, "E386", {"start": v(-3.82, 8.76) * mm, "end": v(-3.87, 8.82) * mm});
            skLineSegment(sketch, "E387", {"start": v(-3.87, 8.82) * mm, "end": v(-3.93, 8.87) * mm});
            skLineSegment(sketch, "E388", {"start": v(-3.93, 8.87) * mm, "end": v(-4, 8.93) * mm});
            skLineSegment(sketch, "E389", {"start": v(-4, 8.93) * mm, "end": v(-4.06, 9) * mm});
            skLineSegment(sketch, "E390", {"start": v(-4.06, 9) * mm, "end": v(-4.14, 9.05) * mm});
            skLineSegment(sketch, "E391", {"start": v(-4.14, 9.05) * mm, "end": v(-4.21, 9.11) * mm});
            skLineSegment(sketch, "E392", {"start": v(-4.21, 9.11) * mm, "end": v(-4.3, 9.18) * mm});
            skLineSegment(sketch, "E393", {"start": v(-4.3, 9.18) * mm, "end": v(-4.38, 9.24) * mm});
            skLineSegment(sketch, "E394", {"start": v(-4.38, 9.24) * mm, "end": v(-4.47, 9.3) * mm});
            skLineSegment(sketch, "E395", {"start": v(-4.47, 9.3) * mm, "end": v(-4.57, 9.37) * mm});
            skLineSegment(sketch, "E396", {"start": v(-4.57, 9.37) * mm, "end": v(-4.67, 9.43) * mm});
            skLineSegment(sketch, "E397", {"start": v(-4.67, 9.43) * mm, "end": v(-4.78, 9.5) * mm});
            skLineSegment(sketch, "E398", {"start": v(-4.78, 9.5) * mm, "end": v(-4.9, 9.56) * mm});
            skLineSegment(sketch, "E399", {"start": v(-4.9, 9.56) * mm, "end": v(-5, 9.62) * mm});
            skLineSegment(sketch, "E400", {"start": v(-5, 9.62) * mm, "end": v(-5.13, 9.68) * mm});
            skLineSegment(sketch, "E401", {"start": v(-5.13, 9.68) * mm, "end": v(-5.26, 9.74) * mm});
            skLineSegment(sketch, "E402", {"start": v(-5.26, 9.74) * mm, "end": v(-5.39, 9.8) * mm});
            skLineSegment(sketch, "E403", {"start": v(-5.39, 9.8) * mm, "end": v(-5.5, 9.81) * mm});
            skLineSegment(sketch, "E404", {"start": v(-5.5, 9.81) * mm, "end": v(-5.81, 9.63) * mm});
            skLineSegment(sketch, "E405", {"start": v(-5.81, 9.63) * mm, "end": v(-5.86, 9.53) * mm});
            skLineSegment(sketch, "E406", {"start": v(-5.86, 9.53) * mm, "end": v(-5.87, 9.39) * mm});
            skLineSegment(sketch, "E407", {"start": v(-5.87, 9.39) * mm, "end": v(-5.88, 9.25) * mm});
            skLineSegment(sketch, "E408", {"start": v(-5.88, 9.25) * mm, "end": v(-5.88, 9.1) * mm});
            skLineSegment(sketch, "E409", {"start": v(-5.88, 9.1) * mm, "end": v(-5.89, 8.98) * mm});
            skLineSegment(sketch, "E410", {"start": v(-5.89, 8.98) * mm, "end": v(-5.89, 8.85) * mm});
            skLineSegment(sketch, "E411", {"start": v(-5.89, 8.85) * mm, "end": v(-5.88, 8.72) * mm});
            skLineSegment(sketch, "E412", {"start": v(-5.88, 8.72) * mm, "end": v(-5.88, 8.6) * mm});
            skLineSegment(sketch, "E413", {"start": v(-5.88, 8.6) * mm, "end": v(-5.87, 8.49) * mm});
            skLineSegment(sketch, "E414", {"start": v(-5.87, 8.49) * mm, "end": v(-5.86, 8.38) * mm});
            skLineSegment(sketch, "E415", {"start": v(-5.86, 8.38) * mm, "end": v(-5.85, 8.27) * mm});
            skLineSegment(sketch, "E416", {"start": v(-5.85, 8.27) * mm, "end": v(-5.84, 8.17) * mm});
            skLineSegment(sketch, "E417", {"start": v(-5.84, 8.17) * mm, "end": v(-5.82, 8.07) * mm});
            skLineSegment(sketch, "E418", {"start": v(-5.82, 8.07) * mm, "end": v(-5.8, 7.98) * mm});
            skLineSegment(sketch, "E419", {"start": v(-5.8, 7.98) * mm, "end": v(-5.79, 7.89) * mm});
            skLineSegment(sketch, "E420", {"start": v(-5.79, 7.89) * mm, "end": v(-5.77, 7.8) * mm});
            skLineSegment(sketch, "E421", {"start": v(-5.77, 7.8) * mm, "end": v(-5.75, 7.73) * mm});
            skLineSegment(sketch, "E422", {"start": v(-5.75, 7.73) * mm, "end": v(-5.73, 7.65) * mm});
            skLineSegment(sketch, "E423", {"start": v(-5.73, 7.65) * mm, "end": v(-5.7, 7.58) * mm});
            skLineSegment(sketch, "E424", {"start": v(-5.7, 7.58) * mm, "end": v(-5.69, 7.51) * mm});
            skLineSegment(sketch, "E425", {"start": v(-5.69, 7.51) * mm, "end": v(-5.67, 7.45) * mm});
            skLineSegment(sketch, "E426", {"start": v(-5.67, 7.45) * mm, "end": v(-5.65, 7.4) * mm});
            skLineSegment(sketch, "E427", {"start": v(-5.65, 7.4) * mm, "end": v(-5.63, 7.34) * mm});
            skLineSegment(sketch, "E428", {"start": v(-5.63, 7.34) * mm, "end": v(-5.6, 7.3) * mm});
            skLineSegment(sketch, "E429", {"start": v(-5.6, 7.3) * mm, "end": v(-5.59, 7.25) * mm});
            skLineSegment(sketch, "E430", {"start": v(-5.59, 7.25) * mm, "end": v(-5.57, 7.21) * mm});
            skLineSegment(sketch, "E431", {"start": v(-5.57, 7.21) * mm, "end": v(-5.55, 7.18) * mm});
            skLineSegment(sketch, "E432", {"start": v(-5.55, 7.18) * mm, "end": v(-5.54, 7.15) * mm});
            skLineSegment(sketch, "E433", {"start": v(-5.54, 7.15) * mm, "end": v(-5.52, 7.12) * mm});
            skLineSegment(sketch, "E434", {"start": v(-5.52, 7.12) * mm, "end": v(-5.5, 7.1) * mm});
            skLineSegment(sketch, "E435", {"start": v(-5.5, 7.1) * mm, "end": v(-5.5, 7.08) * mm});
            skLineSegment(sketch, "E436", {"start": v(-5.5, 7.08) * mm, "end": v(-5.49, 7.06) * mm});
            skLineSegment(sketch, "E437", {"start": v(-5.49, 7.06) * mm, "end": v(-5.48, 7.05) * mm});
            skLineSegment(sketch, "E438", {"start": v(-5.48, 7.05) * mm, "end": v(-5.47, 7.04) * mm});
            skLineSegment(sketch, "E439", {"start": v(-5.47, 7.04) * mm, "end": v(-5.47, 7.04) * mm});
            skLineSegment(sketch, "E440", {"start": v(-5.47, 7.04) * mm, "end": v(-5.25, 6.76) * mm});
            skLineSegment(sketch, "E441", {"start": v(-5.25, 6.76) * mm, "end": v(-6.05, 6.05) * mm});
            skLineSegment(sketch, "E442", {"start": v(-6.05, 6.05) * mm, "end": v(-6.3, 6.3) * mm});
            skLineSegment(sketch, "E443", {"start": v(-6.3, 6.3) * mm, "end": v(-6.3, 6.3) * mm});
            skLineSegment(sketch, "E444", {"start": v(-6.3, 6.3) * mm, "end": v(-6.31, 6.31) * mm});
            skLineSegment(sketch, "E445", {"start": v(-6.31, 6.31) * mm, "end": v(-6.32, 6.32) * mm});
            skLineSegment(sketch, "E446", {"start": v(-6.32, 6.32) * mm, "end": v(-6.34, 6.33) * mm});
            skLineSegment(sketch, "E447", {"start": v(-6.34, 6.33) * mm, "end": v(-6.35, 6.35) * mm});
            skLineSegment(sketch, "E448", {"start": v(-6.35, 6.35) * mm, "end": v(-6.38, 6.36) * mm});
            skLineSegment(sketch, "E449", {"start": v(-6.38, 6.36) * mm, "end": v(-6.4, 6.38) * mm});
            skLineSegment(sketch, "E450", {"start": v(-6.4, 6.38) * mm, "end": v(-6.43, 6.4) * mm});
            skLineSegment(sketch, "E451", {"start": v(-6.43, 6.4) * mm, "end": v(-6.46, 6.42) * mm});
            skLineSegment(sketch, "E452", {"start": v(-6.46, 6.42) * mm, "end": v(-6.5, 6.45) * mm});
            skLineSegment(sketch, "E453", {"start": v(-6.5, 6.45) * mm, "end": v(-6.54, 6.47) * mm});
            skLineSegment(sketch, "E454", {"start": v(-6.54, 6.47) * mm, "end": v(-6.59, 6.5) * mm});
            skLineSegment(sketch, "E455", {"start": v(-6.59, 6.5) * mm, "end": v(-6.64, 6.52) * mm});
            skLineSegment(sketch, "E456", {"start": v(-6.64, 6.52) * mm, "end": v(-6.7, 6.55) * mm});
            skLineSegment(sketch, "E457", {"start": v(-6.7, 6.55) * mm, "end": v(-6.75, 6.58) * mm});
            skLineSegment(sketch, "E458", {"start": v(-6.75, 6.58) * mm, "end": v(-6.81, 6.6) * mm});
            skLineSegment(sketch, "E459", {"start": v(-6.81, 6.6) * mm, "end": v(-6.88, 6.64) * mm});
            skLineSegment(sketch, "E460", {"start": v(-6.88, 6.64) * mm, "end": v(-6.95, 6.67) * mm});
            skLineSegment(sketch, "E461", {"start": v(-6.95, 6.67) * mm, "end": v(-7.03, 6.7) * mm});
            skLineSegment(sketch, "E462", {"start": v(-7.03, 6.7) * mm, "end": v(-7.1, 6.72) * mm});
            skLineSegment(sketch, "E463", {"start": v(-7.1, 6.72) * mm, "end": v(-7.2, 6.75) * mm});
            skLineSegment(sketch, "E464", {"start": v(-7.2, 6.75) * mm, "end": v(-7.28, 6.78) * mm});
            skLineSegment(sketch, "E465", {"start": v(-7.28, 6.78) * mm, "end": v(-7.38, 6.8) * mm});
            skLineSegment(sketch, "E466", {"start": v(-7.38, 6.8) * mm, "end": v(-7.48, 6.83) * mm});
            skLineSegment(sketch, "E467", {"start": v(-7.48, 6.83) * mm, "end": v(-7.58, 6.86) * mm});
            skLineSegment(sketch, "E468", {"start": v(-7.58, 6.86) * mm, "end": v(-7.7, 6.88) * mm});
            skLineSegment(sketch, "E469", {"start": v(-7.7, 6.88) * mm, "end": v(-7.8, 6.9) * mm});
            skLineSegment(sketch, "E470", {"start": v(-7.8, 6.9) * mm, "end": v(-7.92, 6.92) * mm});
            skLineSegment(sketch, "E471", {"start": v(-7.92, 6.92) * mm, "end": v(-8.05, 6.94) * mm});
            skLineSegment(sketch, "E472", {"start": v(-8.05, 6.94) * mm, "end": v(-8.18, 6.96) * mm});
            skLineSegment(sketch, "E473", {"start": v(-8.18, 6.96) * mm, "end": v(-8.3, 6.97) * mm});
            skLineSegment(sketch, "E474", {"start": v(-8.3, 6.97) * mm, "end": v(-8.44, 6.98) * mm});
            skLineSegment(sketch, "E475", {"start": v(-8.44, 6.98) * mm, "end": v(-8.58, 7) * mm});
            skLineSegment(sketch, "E476", {"start": v(-8.58, 7) * mm, "end": v(-8.73, 7) * mm});
            skLineSegment(sketch, "E477", {"start": v(-8.73, 7) * mm, "end": v(-8.84, 6.96) * mm});
            skLineSegment(sketch, "E478", {"start": v(-8.84, 6.96) * mm, "end": v(-9.05, 6.68) * mm});
            skLineSegment(sketch, "E479", {"start": v(-9.05, 6.68) * mm, "end": v(-9.06, 6.57) * mm});
            skLineSegment(sketch, "E480", {"start": v(-9.06, 6.57) * mm, "end": v(-9.01, 6.43) * mm});
            skLineSegment(sketch, "E481", {"start": v(-9.01, 6.43) * mm, "end": v(-8.97, 6.3) * mm});
            skLineSegment(sketch, "E482", {"start": v(-8.97, 6.3) * mm, "end": v(-8.92, 6.16) * mm});
            skLineSegment(sketch, "E483", {"start": v(-8.92, 6.16) * mm, "end": v(-8.87, 6.04) * mm});
            skLineSegment(sketch, "E484", {"start": v(-8.87, 6.04) * mm, "end": v(-8.82, 5.92) * mm});
            skLineSegment(sketch, "E485", {"start": v(-8.82, 5.92) * mm, "end": v(-8.77, 5.8) * mm});
            skLineSegment(sketch, "E486", {"start": v(-8.77, 5.8) * mm, "end": v(-8.72, 5.7) * mm});
            skLineSegment(sketch, "E487", {"start": v(-8.72, 5.7) * mm, "end": v(-8.67, 5.6) * mm});
            skLineSegment(sketch, "E488", {"start": v(-8.67, 5.6) * mm, "end": v(-8.62, 5.5) * mm});
            skLineSegment(sketch, "E489", {"start": v(-8.62, 5.5) * mm, "end": v(-8.57, 5.4) * mm});
            skLineSegment(sketch, "E490", {"start": v(-8.57, 5.4) * mm, "end": v(-8.52, 5.31) * mm});
            skLineSegment(sketch, "E491", {"start": v(-8.52, 5.31) * mm, "end": v(-8.47, 5.23) * mm});
            skLineSegment(sketch, "E492", {"start": v(-8.47, 5.23) * mm, "end": v(-8.42, 5.15) * mm});
            skLineSegment(sketch, "E493", {"start": v(-8.42, 5.15) * mm, "end": v(-8.37, 5.07) * mm});
            skLineSegment(sketch, "E494", {"start": v(-8.37, 5.07) * mm, "end": v(-8.32, 5) * mm});
            skLineSegment(sketch, "E495", {"start": v(-8.32, 5) * mm, "end": v(-8.27, 4.94) * mm});
            skLineSegment(sketch, "E496", {"start": v(-8.27, 4.94) * mm, "end": v(-8.22, 4.88) * mm});
            skLineSegment(sketch, "E497", {"start": v(-8.22, 4.88) * mm, "end": v(-8.18, 4.82) * mm});
            skLineSegment(sketch, "E498", {"start": v(-8.18, 4.82) * mm, "end": v(-8.13, 4.77) * mm});
            skLineSegment(sketch, "E499", {"start": v(-8.13, 4.77) * mm, "end": v(-8.09, 4.72) * mm});
            skLineSegment(sketch, "E500", {"start": v(-8.09, 4.72) * mm, "end": v(-8.05, 4.67) * mm});
            skLineSegment(sketch, "E501", {"start": v(-8.05, 4.67) * mm, "end": v(-8, 4.63) * mm});
            skLineSegment(sketch, "E502", {"start": v(-8, 4.63) * mm, "end": v(-7.97, 4.6) * mm});
            skLineSegment(sketch, "E503", {"start": v(-7.97, 4.6) * mm, "end": v(-7.94, 4.56) * mm});
            skLineSegment(sketch, "E504", {"start": v(-7.94, 4.56) * mm, "end": v(-7.9, 4.53) * mm});
            skLineSegment(sketch, "E505", {"start": v(-7.9, 4.53) * mm, "end": v(-7.87, 4.5) * mm});
            skLineSegment(sketch, "E506", {"start": v(-7.87, 4.5) * mm, "end": v(-7.85, 4.48) * mm});
            skLineSegment(sketch, "E507", {"start": v(-7.85, 4.48) * mm, "end": v(-7.82, 4.46) * mm});
            skLineSegment(sketch, "E508", {"start": v(-7.82, 4.46) * mm, "end": v(-7.8, 4.45) * mm});
            skLineSegment(sketch, "E509", {"start": v(-7.8, 4.45) * mm, "end": v(-7.78, 4.43) * mm});
            skLineSegment(sketch, "E510", {"start": v(-7.78, 4.43) * mm, "end": v(-7.77, 4.42) * mm});
            skLineSegment(sketch, "E511", {"start": v(-7.77, 4.42) * mm, "end": v(-7.76, 4.42) * mm});
            skLineSegment(sketch, "E512", {"start": v(-7.76, 4.42) * mm, "end": v(-7.75, 4.41) * mm});
            skLineSegment(sketch, "E513", {"start": v(-7.75, 4.41) * mm, "end": v(-7.75, 4.4) * mm});
            skLineSegment(sketch, "E514", {"start": v(-7.75, 4.4) * mm, "end": v(-7.44, 4.24) * mm});
            skLineSegment(sketch, "E515", {"start": v(-7.44, 4.24) * mm, "end": v(-7.91, 3.28) * mm});
            skLineSegment(sketch, "E516", {"start": v(-7.91, 3.28) * mm, "end": v(-8.23, 3.41) * mm});
            skLineSegment(sketch, "E517", {"start": v(-8.23, 3.41) * mm, "end": v(-8.24, 3.41) * mm});
            skLineSegment(sketch, "E518", {"start": v(-8.24, 3.41) * mm, "end": v(-8.25, 3.42) * mm});
            skLineSegment(sketch, "E519", {"start": v(-8.25, 3.42) * mm, "end": v(-8.26, 3.42) * mm});
            skLineSegment(sketch, "E520", {"start": v(-8.26, 3.42) * mm, "end": v(-8.28, 3.43) * mm});
            skLineSegment(sketch, "E521", {"start": v(-8.28, 3.43) * mm, "end": v(-8.3, 3.43) * mm});
            skLineSegment(sketch, "E522", {"start": v(-8.3, 3.43) * mm, "end": v(-8.33, 3.44) * mm});
            skLineSegment(sketch, "E523", {"start": v(-8.33, 3.44) * mm, "end": v(-8.36, 3.45) * mm});
            skLineSegment(sketch, "E524", {"start": v(-8.36, 3.45) * mm, "end": v(-8.4, 3.45) * mm});
            skLineSegment(sketch, "E525", {"start": v(-8.4, 3.45) * mm, "end": v(-8.43, 3.46) * mm});
            skLineSegment(sketch, "E526", {"start": v(-8.43, 3.46) * mm, "end": v(-8.47, 3.47) * mm});
            skLineSegment(sketch, "E527", {"start": v(-8.47, 3.47) * mm, "end": v(-8.52, 3.47) * mm});
            skLineSegment(sketch, "E528", {"start": v(-8.52, 3.47) * mm, "end": v(-8.57, 3.48) * mm});
            skLineSegment(sketch, "E529", {"start": v(-8.57, 3.48) * mm, "end": v(-8.63, 3.49) * mm});
            skLineSegment(sketch, "E530", {"start": v(-8.63, 3.49) * mm, "end": v(-8.69, 3.5) * mm});
            skLineSegment(sketch, "E531", {"start": v(-8.69, 3.5) * mm, "end": v(-8.75, 3.5) * mm});
            skLineSegment(sketch, "E532", {"start": v(-8.75, 3.5) * mm, "end": v(-8.82, 3.5) * mm});
            skLineSegment(sketch, "E533", {"start": v(-8.82, 3.5) * mm, "end": v(-8.9, 3.5) * mm});
            skLineSegment(sketch, "E534", {"start": v(-8.9, 3.5) * mm, "end": v(-8.97, 3.5) * mm});
            skLineSegment(sketch, "E535", {"start": v(-8.97, 3.5) * mm, "end": v(-9.05, 3.5) * mm});
            skLineSegment(sketch, "E536", {"start": v(-9.05, 3.5) * mm, "end": v(-9.14, 3.5) * mm});
            skLineSegment(sketch, "E537", {"start": v(-9.14, 3.5) * mm, "end": v(-9.23, 3.49) * mm});
            skLineSegment(sketch, "E538", {"start": v(-9.23, 3.49) * mm, "end": v(-9.32, 3.48) * mm});
            skLineSegment(sketch, "E539", {"start": v(-9.32, 3.48) * mm, "end": v(-9.42, 3.47) * mm});
            skLineSegment(sketch, "E540", {"start": v(-9.42, 3.47) * mm, "end": v(-9.52, 3.45) * mm});
            skLineSegment(sketch, "E541", {"start": v(-9.52, 3.45) * mm, "end": v(-9.63, 3.43) * mm});
            skLineSegment(sketch, "E542", {"start": v(-9.63, 3.43) * mm, "end": v(-9.74, 3.41) * mm});
            skLineSegment(sketch, "E543", {"start": v(-9.74, 3.41) * mm, "end": v(-9.85, 3.4) * mm});
            skLineSegment(sketch, "E544", {"start": v(-9.85, 3.4) * mm, "end": v(-9.97, 3.36) * mm});
            skLineSegment(sketch, "E545", {"start": v(-9.97, 3.36) * mm, "end": v(-10.1, 3.33) * mm});
            skLineSegment(sketch, "E546", {"start": v(-10.1, 3.33) * mm, "end": v(-10.22, 3.3) * mm});
            skLineSegment(sketch, "E547", {"start": v(-10.22, 3.3) * mm, "end": v(-10.34, 3.26) * mm});
            skLineSegment(sketch, "E548", {"start": v(-10.34, 3.26) * mm, "end": v(-10.47, 3.22) * mm});
            skLineSegment(sketch, "E549", {"start": v(-10.47, 3.22) * mm, "end": v(-10.6, 3.17) * mm});
            skLineSegment(sketch, "E550", {"start": v(-10.6, 3.17) * mm, "end": v(-10.74, 3.12) * mm});
            skLineSegment(sketch, "E551", {"start": v(-10.74, 3.12) * mm, "end": v(-10.83, 3.05) * mm});
            skLineSegment(sketch, "E552", {"start": v(-10.83, 3.05) * mm, "end": v(-10.92, 2.7) * mm});
            skLineSegment(sketch, "E553", {"start": v(-10.92, 2.7) * mm, "end": v(-10.88, 2.6) * mm});
            skLineSegment(sketch, "E554", {"start": v(-10.88, 2.6) * mm, "end": v(-10.79, 2.49) * mm});
            skLineSegment(sketch, "E555", {"start": v(-10.79, 2.49) * mm, "end": v(-10.7, 2.38) * mm});
            skLineSegment(sketch, "E556", {"start": v(-10.7, 2.38) * mm, "end": v(-10.6, 2.28) * mm});
            skLineSegment(sketch, "E557", {"start": v(-10.6, 2.28) * mm, "end": v(-10.51, 2.18) * mm});
            skLineSegment(sketch, "E558", {"start": v(-10.51, 2.18) * mm, "end": v(-10.42, 2.1) * mm});
            skLineSegment(sketch, "E559", {"start": v(-10.42, 2.1) * mm, "end": v(-10.33, 2) * mm});
            skLineSegment(sketch, "E560", {"start": v(-10.33, 2) * mm, "end": v(-10.24, 1.93) * mm});
            skLineSegment(sketch, "E561", {"start": v(-10.24, 1.93) * mm, "end": v(-10.15, 1.85) * mm});
            skLineSegment(sketch, "E562", {"start": v(-10.15, 1.85) * mm, "end": v(-10.07, 1.78) * mm});
            skLineSegment(sketch, "E563", {"start": v(-10.07, 1.78) * mm, "end": v(-9.98, 1.71) * mm});
            skLineSegment(sketch, "E564", {"start": v(-9.98, 1.71) * mm, "end": v(-9.9, 1.65) * mm});
            skLineSegment(sketch, "E565", {"start": v(-9.9, 1.65) * mm, "end": v(-9.82, 1.6) * mm});
            skLineSegment(sketch, "E566", {"start": v(-9.82, 1.6) * mm, "end": v(-9.75, 1.54) * mm});
            skLineSegment(sketch, "E567", {"start": v(-9.75, 1.54) * mm, "end": v(-9.67, 1.49) * mm});
            skLineSegment(sketch, "E568", {"start": v(-9.67, 1.49) * mm, "end": v(-9.6, 1.44) * mm});
            skLineSegment(sketch, "E569", {"start": v(-9.6, 1.44) * mm, "end": v(-9.53, 1.4) * mm});
            skLineSegment(sketch, "E570", {"start": v(-9.53, 1.4) * mm, "end": v(-9.46, 1.36) * mm});
            skLineSegment(sketch, "E571", {"start": v(-9.46, 1.36) * mm, "end": v(-9.4, 1.32) * mm});
            skLineSegment(sketch, "E572", {"start": v(-9.4, 1.32) * mm, "end": v(-9.34, 1.3) * mm});
            skLineSegment(sketch, "E573", {"start": v(-9.34, 1.3) * mm, "end": v(-9.28, 1.26) * mm});
            skLineSegment(sketch, "E574", {"start": v(-9.28, 1.26) * mm, "end": v(-9.22, 1.24) * mm});
            skLineSegment(sketch, "E575", {"start": v(-9.22, 1.24) * mm, "end": v(-9.17, 1.21) * mm});
            skLineSegment(sketch, "E576", {"start": v(-9.17, 1.21) * mm, "end": v(-9.12, 1.2) * mm});
            skLineSegment(sketch, "E577", {"start": v(-9.12, 1.2) * mm, "end": v(-9.08, 1.18) * mm});
            skLineSegment(sketch, "E578", {"start": v(-9.08, 1.18) * mm, "end": v(-9.04, 1.16) * mm});
            skLineSegment(sketch, "E579", {"start": v(-9.04, 1.16) * mm, "end": v(-9, 1.15) * mm});
            skLineSegment(sketch, "E580", {"start": v(-9, 1.15) * mm, "end": v(-8.97, 1.14) * mm});
            skLineSegment(sketch, "E581", {"start": v(-8.97, 1.14) * mm, "end": v(-8.94, 1.13) * mm});
            skLineSegment(sketch, "E582", {"start": v(-8.94, 1.13) * mm, "end": v(-8.91, 1.12) * mm});
            skLineSegment(sketch, "E583", {"start": v(-8.91, 1.12) * mm, "end": v(-8.89, 1.12) * mm});
            skLineSegment(sketch, "E584", {"start": v(-8.89, 1.12) * mm, "end": v(-8.87, 1.11) * mm});
            skLineSegment(sketch, "E585", {"start": v(-8.87, 1.11) * mm, "end": v(-8.86, 1.11) * mm});
            skLineSegment(sketch, "E586", {"start": v(-8.86, 1.11) * mm, "end": v(-8.85, 1.1) * mm});
            skLineSegment(sketch, "E587", {"start": v(-8.85, 1.1) * mm, "end": v(-8.84, 1.1) * mm});
            skLineSegment(sketch, "E588", {"start": v(-8.84, 1.1) * mm, "end": v(-8.5, 1.06) * mm});
            skLineSegment(sketch, "E589", {"start": v(-8.5, 1.06) * mm, "end": v(-8.56, 0) * mm});
            skLineSegment(sketch, "E590", {"start": v(-8.56, 0) * mm, "end": v(-8.91, 0) * mm});
            skLineSegment(sketch, "E591", {"start": v(-8.91, 0) * mm, "end": v(-8.92, 0) * mm});
            skLineSegment(sketch, "E592", {"start": v(-8.92, 0) * mm, "end": v(-8.93, 0) * mm});
            skLineSegment(sketch, "E593", {"start": v(-8.93, 0) * mm, "end": v(-8.94, 0) * mm});
            skLineSegment(sketch, "E594", {"start": v(-8.94, 0) * mm, "end": v(-8.96, 0) * mm});
            skLineSegment(sketch, "E595", {"start": v(-8.96, 0) * mm, "end": v(-8.98, 0) * mm});
            skLineSegment(sketch, "E596", {"start": v(-8.98, 0) * mm, "end": v(-9, 0) * mm});
            skLineSegment(sketch, "E597", {"start": v(-9, 0) * mm, "end": v(-9.04, -0.01) * mm});
            skLineSegment(sketch, "E598", {"start": v(-9.04, -0.01) * mm, "end": v(-9.07, -0.02) * mm});
            skLineSegment(sketch, "E599", {"start": v(-9.07, -0.02) * mm, "end": v(-9.11, -0.03) * mm});
            skLineSegment(sketch, "E600", {"start": v(-9.11, -0.03) * mm, "end": v(-9.15, -0.04) * mm});
            skLineSegment(sketch, "E601", {"start": v(-9.15, -0.04) * mm, "end": v(-9.2, -0.05) * mm});
            skLineSegment(sketch, "E602", {"start": v(-9.2, -0.05) * mm, "end": v(-9.25, -0.06) * mm});
            skLineSegment(sketch, "E603", {"start": v(-9.25, -0.06) * mm, "end": v(-9.3, -0.08) * mm});
            skLineSegment(sketch, "E604", {"start": v(-9.3, -0.08) * mm, "end": v(-9.36, -0.1) * mm});
            skLineSegment(sketch, "E605", {"start": v(-9.36, -0.1) * mm, "end": v(-9.42, -0.12) * mm});
            skLineSegment(sketch, "E606", {"start": v(-9.42, -0.12) * mm, "end": v(-9.49, -0.14) * mm});
            skLineSegment(sketch, "E607", {"start": v(-9.49, -0.14) * mm, "end": v(-9.56, -0.17) * mm});
            skLineSegment(sketch, "E608", {"start": v(-9.56, -0.17) * mm, "end": v(-9.63, -0.2) * mm});
            skLineSegment(sketch, "E609", {"start": v(-9.63, -0.2) * mm, "end": v(-9.7, -0.23) * mm});
            skLineSegment(sketch, "E610", {"start": v(-9.7, -0.23) * mm, "end": v(-9.78, -0.27) * mm});
            skLineSegment(sketch, "E611", {"start": v(-9.78, -0.27) * mm, "end": v(-9.86, -0.31) * mm});
            skLineSegment(sketch, "E612", {"start": v(-9.86, -0.31) * mm, "end": v(-9.95, -0.36) * mm});
            skLineSegment(sketch, "E613", {"start": v(-9.95, -0.36) * mm, "end": v(-10.03, -0.4) * mm});
            skLineSegment(sketch, "E614", {"start": v(-10.03, -0.4) * mm, "end": v(-10.12, -0.46) * mm});
            skLineSegment(sketch, "E615", {"start": v(-10.12, -0.46) * mm, "end": v(-10.21, -0.51) * mm});
            skLineSegment(sketch, "E616", {"start": v(-10.21, -0.51) * mm, "end": v(-10.3, -0.57) * mm});
            skLineSegment(sketch, "E617", {"start": v(-10.3, -0.57) * mm, "end": v(-10.4, -0.64) * mm});
            skLineSegment(sketch, "E618", {"start": v(-10.4, -0.64) * mm, "end": v(-10.5, -0.7) * mm});
            skLineSegment(sketch, "E619", {"start": v(-10.5, -0.7) * mm, "end": v(-10.6, -0.78) * mm});
            skLineSegment(sketch, "E620", {"start": v(-10.6, -0.78) * mm, "end": v(-10.7, -0.86) * mm});
            skLineSegment(sketch, "E621", {"start": v(-10.7, -0.86) * mm, "end": v(-10.8, -0.94) * mm});
            skLineSegment(sketch, "E622", {"start": v(-10.8, -0.94) * mm, "end": v(-10.9, -1.03) * mm});
            skLineSegment(sketch, "E623", {"start": v(-10.9, -1.03) * mm, "end": v(-11.01, -1.13) * mm});
            skLineSegment(sketch, "E624", {"start": v(-11.01, -1.13) * mm, "end": v(-11.12, -1.23) * mm});
            skLineSegment(sketch, "E625", {"start": v(-11.12, -1.23) * mm, "end": v(-11.17, -1.32) * mm});
            skLineSegment(sketch, "E626", {"start": v(-11.17, -1.32) * mm, "end": v(-11.12, -1.68) * mm});
            skLineSegment(sketch, "E627", {"start": v(-11.12, -1.68) * mm, "end": v(-11.05, -1.76) * mm});
            skLineSegment(sketch, "E628", {"start": v(-11.05, -1.76) * mm, "end": v(-10.92, -1.83) * mm});
            skLineSegment(sketch, "E629", {"start": v(-10.92, -1.83) * mm, "end": v(-10.8, -1.9) * mm});
            skLineSegment(sketch, "E630", {"start": v(-10.8, -1.9) * mm, "end": v(-10.67, -1.95) * mm});
            skLineSegment(sketch, "E631", {"start": v(-10.67, -1.95) * mm, "end": v(-10.55, -2) * mm});
            skLineSegment(sketch, "E632", {"start": v(-10.55, -2) * mm, "end": v(-10.43, -2.05) * mm});
            skLineSegment(sketch, "E633", {"start": v(-10.43, -2.05) * mm, "end": v(-10.31, -2.1) * mm});
            skLineSegment(sketch, "E634", {"start": v(-10.31, -2.1) * mm, "end": v(-10.2, -2.14) * mm});
            skLineSegment(sketch, "E635", {"start": v(-10.2, -2.14) * mm, "end": v(-10.09, -2.18) * mm});
            skLineSegment(sketch, "E636", {"start": v(-10.09, -2.18) * mm, "end": v(-9.98, -2.2) * mm});
            skLineSegment(sketch, "E637", {"start": v(-9.98, -2.2) * mm, "end": v(-9.88, -2.24) * mm});
            skLineSegment(sketch, "E638", {"start": v(-9.88, -2.24) * mm, "end": v(-9.78, -2.27) * mm});
            skLineSegment(sketch, "E639", {"start": v(-9.78, -2.27) * mm, "end": v(-9.68, -2.29) * mm});
            skLineSegment(sketch, "E640", {"start": v(-9.68, -2.29) * mm, "end": v(-9.6, -2.31) * mm});
            skLineSegment(sketch, "E641", {"start": v(-9.6, -2.31) * mm, "end": v(-9.5, -2.33) * mm});
            skLineSegment(sketch, "E642", {"start": v(-9.5, -2.33) * mm, "end": v(-9.42, -2.34) * mm});
            skLineSegment(sketch, "E643", {"start": v(-9.42, -2.34) * mm, "end": v(-9.34, -2.36) * mm});
            skLineSegment(sketch, "E644", {"start": v(-9.34, -2.36) * mm, "end": v(-9.26, -2.37) * mm});
            skLineSegment(sketch, "E645", {"start": v(-9.26, -2.37) * mm, "end": v(-9.19, -2.37) * mm});
            skLineSegment(sketch, "E646", {"start": v(-9.19, -2.37) * mm, "end": v(-9.12, -2.38) * mm});
            skLineSegment(sketch, "E647", {"start": v(-9.12, -2.38) * mm, "end": v(-9.05, -2.38) * mm});
            skLineSegment(sketch, "E648", {"start": v(-9.05, -2.38) * mm, "end": v(-9, -2.39) * mm});
            skLineSegment(sketch, "E649", {"start": v(-9, -2.39) * mm, "end": v(-8.94, -2.39) * mm});
            skLineSegment(sketch, "E650", {"start": v(-8.94, -2.39) * mm, "end": v(-8.89, -2.39) * mm});
            skLineSegment(sketch, "E651", {"start": v(-8.89, -2.39) * mm, "end": v(-8.84, -2.39) * mm});
            skLineSegment(sketch, "E652", {"start": v(-8.84, -2.39) * mm, "end": v(-8.8, -2.39) * mm});
            skLineSegment(sketch, "E653", {"start": v(-8.8, -2.39) * mm, "end": v(-8.75, -2.38) * mm});
            skLineSegment(sketch, "E654", {"start": v(-8.75, -2.38) * mm, "end": v(-8.72, -2.38) * mm});
            skLineSegment(sketch, "E655", {"start": v(-8.72, -2.38) * mm, "end": v(-8.69, -2.38) * mm});
            skLineSegment(sketch, "E656", {"start": v(-8.69, -2.38) * mm, "end": v(-8.66, -2.37) * mm});
            skLineSegment(sketch, "E657", {"start": v(-8.66, -2.37) * mm, "end": v(-8.64, -2.37) * mm});
            skLineSegment(sketch, "E658", {"start": v(-8.64, -2.37) * mm, "end": v(-8.62, -2.37) * mm});
            skLineSegment(sketch, "E659", {"start": v(-8.62, -2.37) * mm, "end": v(-8.6, -2.36) * mm});
            skLineSegment(sketch, "E660", {"start": v(-8.6, -2.36) * mm, "end": v(-8.6, -2.36) * mm});
            skLineSegment(sketch, "E661", {"start": v(-8.6, -2.36) * mm, "end": v(-8.26, -2.27) * mm});
            skLineSegment(sketch, "E662", {"start": v(-8.26, -2.27) * mm, "end": v(-7.91, -3.28) * mm});
            skLineSegment(sketch, "E663", {"start": v(-7.91, -3.28) * mm, "end": v(-8.23, -3.41) * mm});
            skLineSegment(sketch, "E664", {"start": v(-8.23, -3.41) * mm, "end": v(-8.24, -3.41) * mm});
            skLineSegment(sketch, "E665", {"start": v(-8.24, -3.41) * mm, "end": v(-8.25, -3.42) * mm});
            skLineSegment(sketch, "E666", {"start": v(-8.25, -3.42) * mm, "end": v(-8.26, -3.42) * mm});
            skLineSegment(sketch, "E667", {"start": v(-8.26, -3.42) * mm, "end": v(-8.28, -3.43) * mm});
            skLineSegment(sketch, "E668", {"start": v(-8.28, -3.43) * mm, "end": v(-8.3, -3.44) * mm});
            skLineSegment(sketch, "E669", {"start": v(-8.3, -3.44) * mm, "end": v(-8.32, -3.46) * mm});
            skLineSegment(sketch, "E670", {"start": v(-8.32, -3.46) * mm, "end": v(-8.34, -3.47) * mm});
            skLineSegment(sketch, "E671", {"start": v(-8.34, -3.47) * mm, "end": v(-8.37, -3.5) * mm});
            skLineSegment(sketch, "E672", {"start": v(-8.37, -3.5) * mm, "end": v(-8.4, -3.51) * mm});
            skLineSegment(sketch, "E673", {"start": v(-8.4, -3.51) * mm, "end": v(-8.44, -3.54) * mm});
            skLineSegment(sketch, "E674", {"start": v(-8.44, -3.54) * mm, "end": v(-8.48, -3.57) * mm});
            skLineSegment(sketch, "E675", {"start": v(-8.48, -3.57) * mm, "end": v(-8.52, -3.6) * mm});
            skLineSegment(sketch, "E676", {"start": v(-8.52, -3.6) * mm, "end": v(-8.57, -3.63) * mm});
            skLineSegment(sketch, "E677", {"start": v(-8.57, -3.63) * mm, "end": v(-8.61, -3.67) * mm});
            skLineSegment(sketch, "E678", {"start": v(-8.61, -3.67) * mm, "end": v(-8.66, -3.72) * mm});
            skLineSegment(sketch, "E679", {"start": v(-8.66, -3.72) * mm, "end": v(-8.71, -3.76) * mm});
            skLineSegment(sketch, "E680", {"start": v(-8.71, -3.76) * mm, "end": v(-8.76, -3.82) * mm});
            skLineSegment(sketch, "E681", {"start": v(-8.76, -3.82) * mm, "end": v(-8.82, -3.87) * mm});
            skLineSegment(sketch, "E682", {"start": v(-8.82, -3.87) * mm, "end": v(-8.87, -3.93) * mm});
            skLineSegment(sketch, "E683", {"start": v(-8.87, -3.93) * mm, "end": v(-8.93, -4) * mm});
            skLineSegment(sketch, "E684", {"start": v(-8.93, -4) * mm, "end": v(-9, -4.06) * mm});
            skLineSegment(sketch, "E685", {"start": v(-9, -4.06) * mm, "end": v(-9.05, -4.14) * mm});
            skLineSegment(sketch, "E686", {"start": v(-9.05, -4.14) * mm, "end": v(-9.11, -4.21) * mm});
            skLineSegment(sketch, "E687", {"start": v(-9.11, -4.21) * mm, "end": v(-9.18, -4.3) * mm});
            skLineSegment(sketch, "E688", {"start": v(-9.18, -4.3) * mm, "end": v(-9.24, -4.38) * mm});
            skLineSegment(sketch, "E689", {"start": v(-9.24, -4.38) * mm, "end": v(-9.3, -4.47) * mm});
            skLineSegment(sketch, "E690", {"start": v(-9.3, -4.47) * mm, "end": v(-9.37, -4.57) * mm});
            skLineSegment(sketch, "E691", {"start": v(-9.37, -4.57) * mm, "end": v(-9.43, -4.67) * mm});
            skLineSegment(sketch, "E692", {"start": v(-9.43, -4.67) * mm, "end": v(-9.5, -4.78) * mm});
            skLineSegment(sketch, "E693", {"start": v(-9.5, -4.78) * mm, "end": v(-9.56, -4.9) * mm});
            skLineSegment(sketch, "E694", {"start": v(-9.56, -4.9) * mm, "end": v(-9.62, -5) * mm});
            skLineSegment(sketch, "E695", {"start": v(-9.62, -5) * mm, "end": v(-9.68, -5.13) * mm});
            skLineSegment(sketch, "E696", {"start": v(-9.68, -5.13) * mm, "end": v(-9.74, -5.26) * mm});
            skLineSegment(sketch, "E697", {"start": v(-9.74, -5.26) * mm, "end": v(-9.8, -5.39) * mm});
            skLineSegment(sketch, "E698", {"start": v(-9.8, -5.39) * mm, "end": v(-9.81, -5.5) * mm});
            skLineSegment(sketch, "E699", {"start": v(-9.81, -5.5) * mm, "end": v(-9.63, -5.81) * mm});
            skLineSegment(sketch, "E700", {"start": v(-9.63, -5.81) * mm, "end": v(-9.53, -5.86) * mm});
            skLineSegment(sketch, "E701", {"start": v(-9.53, -5.86) * mm, "end": v(-9.39, -5.87) * mm});
            skLineSegment(sketch, "E702", {"start": v(-9.39, -5.87) * mm, "end": v(-9.25, -5.88) * mm});
            skLineSegment(sketch, "E703", {"start": v(-9.25, -5.88) * mm, "end": v(-9.1, -5.88) * mm});
            skLineSegment(sketch, "E704", {"start": v(-9.1, -5.88) * mm, "end": v(-8.98, -5.89) * mm});
            skLineSegment(sketch, "E705", {"start": v(-8.98, -5.89) * mm, "end": v(-8.85, -5.89) * mm});
            skLineSegment(sketch, "E706", {"start": v(-8.85, -5.89) * mm, "end": v(-8.72, -5.88) * mm});
            skLineSegment(sketch, "E707", {"start": v(-8.72, -5.88) * mm, "end": v(-8.6, -5.88) * mm});
            skLineSegment(sketch, "E708", {"start": v(-8.6, -5.88) * mm, "end": v(-8.49, -5.87) * mm});
            skLineSegment(sketch, "E709", {"start": v(-8.49, -5.87) * mm, "end": v(-8.38, -5.86) * mm});
            skLineSegment(sketch, "E710", {"start": v(-8.38, -5.86) * mm, "end": v(-8.27, -5.85) * mm});
            skLineSegment(sketch, "E711", {"start": v(-8.27, -5.85) * mm, "end": v(-8.17, -5.84) * mm});
            skLineSegment(sketch, "E712", {"start": v(-8.17, -5.84) * mm, "end": v(-8.07, -5.82) * mm});
            skLineSegment(sketch, "E713", {"start": v(-8.07, -5.82) * mm, "end": v(-7.98, -5.8) * mm});
            skLineSegment(sketch, "E714", {"start": v(-7.98, -5.8) * mm, "end": v(-7.89, -5.79) * mm});
            skLineSegment(sketch, "E715", {"start": v(-7.89, -5.79) * mm, "end": v(-7.8, -5.77) * mm});
            skLineSegment(sketch, "E716", {"start": v(-7.8, -5.77) * mm, "end": v(-7.73, -5.75) * mm});
            skLineSegment(sketch, "E717", {"start": v(-7.73, -5.75) * mm, "end": v(-7.65, -5.73) * mm});
            skLineSegment(sketch, "E718", {"start": v(-7.65, -5.73) * mm, "end": v(-7.58, -5.7) * mm});
            skLineSegment(sketch, "E719", {"start": v(-7.58, -5.7) * mm, "end": v(-7.51, -5.69) * mm});
            skLineSegment(sketch, "E720", {"start": v(-7.51, -5.69) * mm, "end": v(-7.45, -5.67) * mm});
            skLineSegment(sketch, "E721", {"start": v(-7.45, -5.67) * mm, "end": v(-7.4, -5.65) * mm});
            skLineSegment(sketch, "E722", {"start": v(-7.4, -5.65) * mm, "end": v(-7.34, -5.63) * mm});
            skLineSegment(sketch, "E723", {"start": v(-7.34, -5.63) * mm, "end": v(-7.3, -5.6) * mm});
            skLineSegment(sketch, "E724", {"start": v(-7.3, -5.6) * mm, "end": v(-7.25, -5.59) * mm});
            skLineSegment(sketch, "E725", {"start": v(-7.25, -5.59) * mm, "end": v(-7.21, -5.57) * mm});
            skLineSegment(sketch, "E726", {"start": v(-7.21, -5.57) * mm, "end": v(-7.18, -5.55) * mm});
            skLineSegment(sketch, "E727", {"start": v(-7.18, -5.55) * mm, "end": v(-7.15, -5.54) * mm});
            skLineSegment(sketch, "E728", {"start": v(-7.15, -5.54) * mm, "end": v(-7.12, -5.52) * mm});
            skLineSegment(sketch, "E729", {"start": v(-7.12, -5.52) * mm, "end": v(-7.1, -5.5) * mm});
            skLineSegment(sketch, "E730", {"start": v(-7.1, -5.5) * mm, "end": v(-7.08, -5.5) * mm});
            skLineSegment(sketch, "E731", {"start": v(-7.08, -5.5) * mm, "end": v(-7.06, -5.49) * mm});
            skLineSegment(sketch, "E732", {"start": v(-7.06, -5.49) * mm, "end": v(-7.05, -5.48) * mm});
            skLineSegment(sketch, "E733", {"start": v(-7.05, -5.48) * mm, "end": v(-7.04, -5.47) * mm});
            skLineSegment(sketch, "E734", {"start": v(-7.04, -5.47) * mm, "end": v(-7.04, -5.47) * mm});
            skLineSegment(sketch, "E735", {"start": v(-7.04, -5.47) * mm, "end": v(-6.76, -5.25) * mm});
            skLineSegment(sketch, "E736", {"start": v(-6.76, -5.25) * mm, "end": v(-6.05, -6.05) * mm});
            skLineSegment(sketch, "E737", {"start": v(-6.05, -6.05) * mm, "end": v(-6.3, -6.3) * mm});
            skLineSegment(sketch, "E738", {"start": v(-6.3, -6.3) * mm, "end": v(-6.3, -6.3) * mm});
            skLineSegment(sketch, "E739", {"start": v(-6.3, -6.3) * mm, "end": v(-6.31, -6.31) * mm});
            skLineSegment(sketch, "E740", {"start": v(-6.31, -6.31) * mm, "end": v(-6.32, -6.32) * mm});
            skLineSegment(sketch, "E741", {"start": v(-6.32, -6.32) * mm, "end": v(-6.33, -6.34) * mm});
            skLineSegment(sketch, "E742", {"start": v(-6.33, -6.34) * mm, "end": v(-6.35, -6.35) * mm});
            skLineSegment(sketch, "E743", {"start": v(-6.35, -6.35) * mm, "end": v(-6.36, -6.38) * mm});
            skLineSegment(sketch, "E744", {"start": v(-6.36, -6.38) * mm, "end": v(-6.38, -6.4) * mm});
            skLineSegment(sketch, "E745", {"start": v(-6.38, -6.4) * mm, "end": v(-6.4, -6.43) * mm});
            skLineSegment(sketch, "E746", {"start": v(-6.4, -6.43) * mm, "end": v(-6.42, -6.46) * mm});
            skLineSegment(sketch, "E747", {"start": v(-6.42, -6.46) * mm, "end": v(-6.45, -6.5) * mm});
            skLineSegment(sketch, "E748", {"start": v(-6.45, -6.5) * mm, "end": v(-6.47, -6.54) * mm});
            skLineSegment(sketch, "E749", {"start": v(-6.47, -6.54) * mm, "end": v(-6.5, -6.59) * mm});
            skLineSegment(sketch, "E750", {"start": v(-6.5, -6.59) * mm, "end": v(-6.52, -6.64) * mm});
            skLineSegment(sketch, "E751", {"start": v(-6.52, -6.64) * mm, "end": v(-6.55, -6.7) * mm});
            skLineSegment(sketch, "E752", {"start": v(-6.55, -6.7) * mm, "end": v(-6.58, -6.75) * mm});
            skLineSegment(sketch, "E753", {"start": v(-6.58, -6.75) * mm, "end": v(-6.6, -6.81) * mm});
            skLineSegment(sketch, "E754", {"start": v(-6.6, -6.81) * mm, "end": v(-6.64, -6.88) * mm});
            skLineSegment(sketch, "E755", {"start": v(-6.64, -6.88) * mm, "end": v(-6.67, -6.95) * mm});
            skLineSegment(sketch, "E756", {"start": v(-6.67, -6.95) * mm, "end": v(-6.7, -7.03) * mm});
            skLineSegment(sketch, "E757", {"start": v(-6.7, -7.03) * mm, "end": v(-6.72, -7.1) * mm});
            skLineSegment(sketch, "E758", {"start": v(-6.72, -7.1) * mm, "end": v(-6.75, -7.2) * mm});
            skLineSegment(sketch, "E759", {"start": v(-6.75, -7.2) * mm, "end": v(-6.78, -7.28) * mm});
            skLineSegment(sketch, "E760", {"start": v(-6.78, -7.28) * mm, "end": v(-6.8, -7.38) * mm});
            skLineSegment(sketch, "E761", {"start": v(-6.8, -7.38) * mm, "end": v(-6.83, -7.48) * mm});
            skLineSegment(sketch, "E762", {"start": v(-6.83, -7.48) * mm, "end": v(-6.86, -7.58) * mm});
            skLineSegment(sketch, "E763", {"start": v(-6.86, -7.58) * mm, "end": v(-6.88, -7.7) * mm});
            skLineSegment(sketch, "E764", {"start": v(-6.88, -7.7) * mm, "end": v(-6.9, -7.8) * mm});
            skLineSegment(sketch, "E765", {"start": v(-6.9, -7.8) * mm, "end": v(-6.92, -7.92) * mm});
            skLineSegment(sketch, "E766", {"start": v(-6.92, -7.92) * mm, "end": v(-6.94, -8.05) * mm});
            skLineSegment(sketch, "E767", {"start": v(-6.94, -8.05) * mm, "end": v(-6.96, -8.18) * mm});
            skLineSegment(sketch, "E768", {"start": v(-6.96, -8.18) * mm, "end": v(-6.97, -8.3) * mm});
            skLineSegment(sketch, "E769", {"start": v(-6.97, -8.3) * mm, "end": v(-6.98, -8.44) * mm});
            skLineSegment(sketch, "E770", {"start": v(-6.98, -8.44) * mm, "end": v(-7, -8.58) * mm});
            skLineSegment(sketch, "E771", {"start": v(-7, -8.58) * mm, "end": v(-7, -8.73) * mm});
            skLineSegment(sketch, "E772", {"start": v(-7, -8.73) * mm, "end": v(-6.96, -8.84) * mm});
            skLineSegment(sketch, "E773", {"start": v(-6.96, -8.84) * mm, "end": v(-6.68, -9.05) * mm});
            skLineSegment(sketch, "E774", {"start": v(-6.68, -9.05) * mm, "end": v(-6.57, -9.06) * mm});
            skLineSegment(sketch, "E775", {"start": v(-6.57, -9.06) * mm, "end": v(-6.43, -9.01) * mm});
            skLineSegment(sketch, "E776", {"start": v(-6.43, -9.01) * mm, "end": v(-6.3, -8.97) * mm});
            skLineSegment(sketch, "E777", {"start": v(-6.3, -8.97) * mm, "end": v(-6.16, -8.92) * mm});
            skLineSegment(sketch, "E778", {"start": v(-6.16, -8.92) * mm, "end": v(-6.04, -8.87) * mm});
            skLineSegment(sketch, "E779", {"start": v(-6.04, -8.87) * mm, "end": v(-5.92, -8.82) * mm});
            skLineSegment(sketch, "E780", {"start": v(-5.92, -8.82) * mm, "end": v(-5.8, -8.77) * mm});
            skLineSegment(sketch, "E781", {"start": v(-5.8, -8.77) * mm, "end": v(-5.7, -8.72) * mm});
            skLineSegment(sketch, "E782", {"start": v(-5.7, -8.72) * mm, "end": v(-5.6, -8.67) * mm});
            skLineSegment(sketch, "E783", {"start": v(-5.6, -8.67) * mm, "end": v(-5.5, -8.62) * mm});
            skLineSegment(sketch, "E784", {"start": v(-5.5, -8.62) * mm, "end": v(-5.4, -8.57) * mm});
            skLineSegment(sketch, "E785", {"start": v(-5.4, -8.57) * mm, "end": v(-5.31, -8.52) * mm});
            skLineSegment(sketch, "E786", {"start": v(-5.31, -8.52) * mm, "end": v(-5.23, -8.47) * mm});
            skLineSegment(sketch, "E787", {"start": v(-5.23, -8.47) * mm, "end": v(-5.15, -8.42) * mm});
            skLineSegment(sketch, "E788", {"start": v(-5.15, -8.42) * mm, "end": v(-5.07, -8.37) * mm});
            skLineSegment(sketch, "E789", {"start": v(-5.07, -8.37) * mm, "end": v(-5, -8.32) * mm});
            skLineSegment(sketch, "E790", {"start": v(-5, -8.32) * mm, "end": v(-4.94, -8.27) * mm});
            skLineSegment(sketch, "E791", {"start": v(-4.94, -8.27) * mm, "end": v(-4.88, -8.22) * mm});
            skLineSegment(sketch, "E792", {"start": v(-4.88, -8.22) * mm, "end": v(-4.82, -8.18) * mm});
            skLineSegment(sketch, "E793", {"start": v(-4.82, -8.18) * mm, "end": v(-4.77, -8.13) * mm});
            skLineSegment(sketch, "E794", {"start": v(-4.77, -8.13) * mm, "end": v(-4.72, -8.09) * mm});
            skLineSegment(sketch, "E795", {"start": v(-4.72, -8.09) * mm, "end": v(-4.67, -8.05) * mm});
            skLineSegment(sketch, "E796", {"start": v(-4.67, -8.05) * mm, "end": v(-4.63, -8) * mm});
            skLineSegment(sketch, "E797", {"start": v(-4.63, -8) * mm, "end": v(-4.6, -7.97) * mm});
            skLineSegment(sketch, "E798", {"start": v(-4.6, -7.97) * mm, "end": v(-4.56, -7.94) * mm});
            skLineSegment(sketch, "E799", {"start": v(-4.56, -7.94) * mm, "end": v(-4.53, -7.9) * mm});
            skLineSegment(sketch, "E800", {"start": v(-4.53, -7.9) * mm, "end": v(-4.5, -7.87) * mm});
            skLineSegment(sketch, "E801", {"start": v(-4.5, -7.87) * mm, "end": v(-4.48, -7.85) * mm});
            skLineSegment(sketch, "E802", {"start": v(-4.48, -7.85) * mm, "end": v(-4.46, -7.82) * mm});
            skLineSegment(sketch, "E803", {"start": v(-4.46, -7.82) * mm, "end": v(-4.45, -7.8) * mm});
            skLineSegment(sketch, "E804", {"start": v(-4.45, -7.8) * mm, "end": v(-4.43, -7.78) * mm});
            skLineSegment(sketch, "E805", {"start": v(-4.43, -7.78) * mm, "end": v(-4.42, -7.77) * mm});
            skLineSegment(sketch, "E806", {"start": v(-4.42, -7.77) * mm, "end": v(-4.42, -7.76) * mm});
            skLineSegment(sketch, "E807", {"start": v(-4.42, -7.76) * mm, "end": v(-4.41, -7.75) * mm});
            skLineSegment(sketch, "E808", {"start": v(-4.41, -7.75) * mm, "end": v(-4.4, -7.75) * mm});
            skLineSegment(sketch, "E809", {"start": v(-4.4, -7.75) * mm, "end": v(-4.24, -7.44) * mm});
            skLineSegment(sketch, "E810", {"start": v(-4.24, -7.44) * mm, "end": v(-3.28, -7.91) * mm});
            skLineSegment(sketch, "E811", {"start": v(-3.28, -7.91) * mm, "end": v(-3.41, -8.23) * mm});
            skLineSegment(sketch, "E812", {"start": v(-3.41, -8.23) * mm, "end": v(-3.41, -8.24) * mm});
            skLineSegment(sketch, "E813", {"start": v(-3.41, -8.24) * mm, "end": v(-3.42, -8.25) * mm});
            skLineSegment(sketch, "E814", {"start": v(-3.42, -8.25) * mm, "end": v(-3.42, -8.26) * mm});
            skLineSegment(sketch, "E815", {"start": v(-3.42, -8.26) * mm, "end": v(-3.43, -8.28) * mm});
            skLineSegment(sketch, "E816", {"start": v(-3.43, -8.28) * mm, "end": v(-3.43, -8.3) * mm});
            skLineSegment(sketch, "E817", {"start": v(-3.43, -8.3) * mm, "end": v(-3.44, -8.33) * mm});
            skLineSegment(sketch, "E818", {"start": v(-3.44, -8.33) * mm, "end": v(-3.45, -8.36) * mm});
            skLineSegment(sketch, "E819", {"start": v(-3.45, -8.36) * mm, "end": v(-3.45, -8.4) * mm});
            skLineSegment(sketch, "E820", {"start": v(-3.45, -8.4) * mm, "end": v(-3.46, -8.43) * mm});
            skLineSegment(sketch, "E821", {"start": v(-3.46, -8.43) * mm, "end": v(-3.47, -8.47) * mm});
            skLineSegment(sketch, "E822", {"start": v(-3.47, -8.47) * mm, "end": v(-3.47, -8.52) * mm});
            skLineSegment(sketch, "E823", {"start": v(-3.47, -8.52) * mm, "end": v(-3.48, -8.57) * mm});
            skLineSegment(sketch, "E824", {"start": v(-3.48, -8.57) * mm, "end": v(-3.49, -8.63) * mm});
            skLineSegment(sketch, "E825", {"start": v(-3.49, -8.63) * mm, "end": v(-3.5, -8.69) * mm});
            skLineSegment(sketch, "E826", {"start": v(-3.5, -8.69) * mm, "end": v(-3.5, -8.75) * mm});
            skLineSegment(sketch, "E827", {"start": v(-3.5, -8.75) * mm, "end": v(-3.5, -8.82) * mm});
            skLineSegment(sketch, "E828", {"start": v(-3.5, -8.82) * mm, "end": v(-3.5, -8.9) * mm});
            skLineSegment(sketch, "E829", {"start": v(-3.5, -8.9) * mm, "end": v(-3.5, -8.97) * mm});
            skLineSegment(sketch, "E830", {"start": v(-3.5, -8.97) * mm, "end": v(-3.5, -9.05) * mm});
            skLineSegment(sketch, "E831", {"start": v(-3.5, -9.05) * mm, "end": v(-3.5, -9.14) * mm});
            skLineSegment(sketch, "E832", {"start": v(-3.5, -9.14) * mm, "end": v(-3.49, -9.23) * mm});
            skLineSegment(sketch, "E833", {"start": v(-3.49, -9.23) * mm, "end": v(-3.48, -9.32) * mm});
            skLineSegment(sketch, "E834", {"start": v(-3.48, -9.32) * mm, "end": v(-3.47, -9.42) * mm});
            skLineSegment(sketch, "E835", {"start": v(-3.47, -9.42) * mm, "end": v(-3.45, -9.52) * mm});
            skLineSegment(sketch, "E836", {"start": v(-3.45, -9.52) * mm, "end": v(-3.43, -9.63) * mm});
            skLineSegment(sketch, "E837", {"start": v(-3.43, -9.63) * mm, "end": v(-3.41, -9.74) * mm});
            skLineSegment(sketch, "E838", {"start": v(-3.41, -9.74) * mm, "end": v(-3.4, -9.85) * mm});
            skLineSegment(sketch, "E839", {"start": v(-3.4, -9.85) * mm, "end": v(-3.36, -9.97) * mm});
            skLineSegment(sketch, "E840", {"start": v(-3.36, -9.97) * mm, "end": v(-3.33, -10.1) * mm});
            skLineSegment(sketch, "E841", {"start": v(-3.33, -10.1) * mm, "end": v(-3.3, -10.22) * mm});
            skLineSegment(sketch, "E842", {"start": v(-3.3, -10.22) * mm, "end": v(-3.26, -10.34) * mm});
            skLineSegment(sketch, "E843", {"start": v(-3.26, -10.34) * mm, "end": v(-3.22, -10.47) * mm});
            skLineSegment(sketch, "E844", {"start": v(-3.22, -10.47) * mm, "end": v(-3.17, -10.6) * mm});
            skLineSegment(sketch, "E845", {"start": v(-3.17, -10.6) * mm, "end": v(-3.12, -10.74) * mm});
            skLineSegment(sketch, "E846", {"start": v(-3.12, -10.74) * mm, "end": v(-3.05, -10.83) * mm});
            skLineSegment(sketch, "E847", {"start": v(-3.05, -10.83) * mm, "end": v(-2.7, -10.92) * mm});
            skLineSegment(sketch, "E848", {"start": v(-2.7, -10.92) * mm, "end": v(-2.6, -10.88) * mm});
            skLineSegment(sketch, "E849", {"start": v(-2.6, -10.88) * mm, "end": v(-2.49, -10.79) * mm});
            skLineSegment(sketch, "E850", {"start": v(-2.49, -10.79) * mm, "end": v(-2.38, -10.7) * mm});
            skLineSegment(sketch, "E851", {"start": v(-2.38, -10.7) * mm, "end": v(-2.28, -10.6) * mm});
            skLineSegment(sketch, "E852", {"start": v(-2.28, -10.6) * mm, "end": v(-2.18, -10.51) * mm});
            skLineSegment(sketch, "E853", {"start": v(-2.18, -10.51) * mm, "end": v(-2.1, -10.42) * mm});
            skLineSegment(sketch, "E854", {"start": v(-2.1, -10.42) * mm, "end": v(-2, -10.33) * mm});
            skLineSegment(sketch, "E855", {"start": v(-2, -10.33) * mm, "end": v(-1.93, -10.24) * mm});
            skLineSegment(sketch, "E856", {"start": v(-1.93, -10.24) * mm, "end": v(-1.85, -10.15) * mm});
            skLineSegment(sketch, "E857", {"start": v(-1.85, -10.15) * mm, "end": v(-1.78, -10.07) * mm});
            skLineSegment(sketch, "E858", {"start": v(-1.78, -10.07) * mm, "end": v(-1.71, -9.98) * mm});
            skLineSegment(sketch, "E859", {"start": v(-1.71, -9.98) * mm, "end": v(-1.65, -9.9) * mm});
            skLineSegment(sketch, "E860", {"start": v(-1.65, -9.9) * mm, "end": v(-1.6, -9.82) * mm});
            skLineSegment(sketch, "E861", {"start": v(-1.6, -9.82) * mm, "end": v(-1.54, -9.75) * mm});
            skLineSegment(sketch, "E862", {"start": v(-1.54, -9.75) * mm, "end": v(-1.49, -9.67) * mm});
            skLineSegment(sketch, "E863", {"start": v(-1.49, -9.67) * mm, "end": v(-1.44, -9.6) * mm});
            skLineSegment(sketch, "E864", {"start": v(-1.44, -9.6) * mm, "end": v(-1.4, -9.53) * mm});
            skLineSegment(sketch, "E865", {"start": v(-1.4, -9.53) * mm, "end": v(-1.36, -9.46) * mm});
            skLineSegment(sketch, "E866", {"start": v(-1.36, -9.46) * mm, "end": v(-1.32, -9.4) * mm});
            skLineSegment(sketch, "E867", {"start": v(-1.32, -9.4) * mm, "end": v(-1.3, -9.34) * mm});
            skLineSegment(sketch, "E868", {"start": v(-1.3, -9.34) * mm, "end": v(-1.26, -9.28) * mm});
            skLineSegment(sketch, "E869", {"start": v(-1.26, -9.28) * mm, "end": v(-1.24, -9.22) * mm});
            skLineSegment(sketch, "E870", {"start": v(-1.24, -9.22) * mm, "end": v(-1.21, -9.17) * mm});
            skLineSegment(sketch, "E871", {"start": v(-1.21, -9.17) * mm, "end": v(-1.2, -9.12) * mm});
            skLineSegment(sketch, "E872", {"start": v(-1.2, -9.12) * mm, "end": v(-1.18, -9.08) * mm});
            skLineSegment(sketch, "E873", {"start": v(-1.18, -9.08) * mm, "end": v(-1.16, -9.04) * mm});
            skLineSegment(sketch, "E874", {"start": v(-1.16, -9.04) * mm, "end": v(-1.15, -9) * mm});
            skLineSegment(sketch, "E875", {"start": v(-1.15, -9) * mm, "end": v(-1.14, -8.97) * mm});
            skLineSegment(sketch, "E876", {"start": v(-1.14, -8.97) * mm, "end": v(-1.13, -8.94) * mm});
            skLineSegment(sketch, "E877", {"start": v(-1.13, -8.94) * mm, "end": v(-1.12, -8.91) * mm});
            skLineSegment(sketch, "E878", {"start": v(-1.12, -8.91) * mm, "end": v(-1.12, -8.89) * mm});
            skLineSegment(sketch, "E879", {"start": v(-1.12, -8.89) * mm, "end": v(-1.11, -8.87) * mm});
            skLineSegment(sketch, "E880", {"start": v(-1.11, -8.87) * mm, "end": v(-1.11, -8.86) * mm});
            skLineSegment(sketch, "E881", {"start": v(-1.11, -8.86) * mm, "end": v(-1.1, -8.85) * mm});
            skLineSegment(sketch, "E882", {"start": v(-1.1, -8.85) * mm, "end": v(-1.1, -8.84) * mm});
            skLineSegment(sketch, "E883", {"start": v(-1.1, -8.84) * mm, "end": v(-1.06, -8.5) * mm});
            skLineSegment(sketch, "E884", {"start": v(-1.06, -8.5) * mm, "end": v(0, -8.56) * mm});
            skLineSegment(sketch, "E885", {"start": v(0, -8.56) * mm, "end": v(0, -8.91) * mm});
            skLineSegment(sketch, "E886", {"start": v(0, -8.91) * mm, "end": v(0, -8.92) * mm});
            skLineSegment(sketch, "E887", {"start": v(0, -8.92) * mm, "end": v(0, -8.93) * mm});
            skLineSegment(sketch, "E888", {"start": v(0, -8.93) * mm, "end": v(0, -8.94) * mm});
            skLineSegment(sketch, "E889", {"start": v(0, -8.94) * mm, "end": v(0, -8.96) * mm});
            skLineSegment(sketch, "E890", {"start": v(0, -8.96) * mm, "end": v(0, -8.98) * mm});
            skLineSegment(sketch, "E891", {"start": v(0, -8.98) * mm, "end": v(0, -9) * mm});
            skLineSegment(sketch, "E892", {"start": v(0, -9) * mm, "end": v(0.01, -9.04) * mm});
            skLineSegment(sketch, "E893", {"start": v(0.01, -9.04) * mm, "end": v(0.02, -9.07) * mm});
            skLineSegment(sketch, "E894", {"start": v(0.02, -9.07) * mm, "end": v(0.03, -9.11) * mm});
            skLineSegment(sketch, "E895", {"start": v(0.03, -9.11) * mm, "end": v(0.04, -9.15) * mm});
            skLineSegment(sketch, "E896", {"start": v(0.04, -9.15) * mm, "end": v(0.05, -9.2) * mm});
            skLineSegment(sketch, "E897", {"start": v(0.05, -9.2) * mm, "end": v(0.06, -9.25) * mm});
            skLineSegment(sketch, "E898", {"start": v(0.06, -9.25) * mm, "end": v(0.08, -9.3) * mm});
            skLineSegment(sketch, "E899", {"start": v(0.08, -9.3) * mm, "end": v(0.1, -9.36) * mm});
            skLineSegment(sketch, "E900", {"start": v(0.1, -9.36) * mm, "end": v(0.12, -9.42) * mm});
            skLineSegment(sketch, "E901", {"start": v(0.12, -9.42) * mm, "end": v(0.14, -9.49) * mm});
            skLineSegment(sketch, "E902", {"start": v(0.14, -9.49) * mm, "end": v(0.17, -9.56) * mm});
            skLineSegment(sketch, "E903", {"start": v(0.17, -9.56) * mm, "end": v(0.2, -9.63) * mm});
            skLineSegment(sketch, "E904", {"start": v(0.2, -9.63) * mm, "end": v(0.23, -9.7) * mm});
            skLineSegment(sketch, "E905", {"start": v(0.23, -9.7) * mm, "end": v(0.27, -9.78) * mm});
            skLineSegment(sketch, "E906", {"start": v(0.27, -9.78) * mm, "end": v(0.31, -9.86) * mm});
            skLineSegment(sketch, "E907", {"start": v(0.31, -9.86) * mm, "end": v(0.36, -9.95) * mm});
            skLineSegment(sketch, "E908", {"start": v(0.36, -9.95) * mm, "end": v(0.4, -10.03) * mm});
            skLineSegment(sketch, "E909", {"start": v(0.4, -10.03) * mm, "end": v(0.46, -10.12) * mm});
            skLineSegment(sketch, "E910", {"start": v(0.46, -10.12) * mm, "end": v(0.51, -10.21) * mm});
            skLineSegment(sketch, "E911", {"start": v(0.51, -10.21) * mm, "end": v(0.57, -10.3) * mm});
            skLineSegment(sketch, "E912", {"start": v(0.57, -10.3) * mm, "end": v(0.64, -10.4) * mm});
            skLineSegment(sketch, "E913", {"start": v(0.64, -10.4) * mm, "end": v(0.7, -10.5) * mm});
            skLineSegment(sketch, "E914", {"start": v(0.7, -10.5) * mm, "end": v(0.78, -10.6) * mm});
            skLineSegment(sketch, "E915", {"start": v(0.78, -10.6) * mm, "end": v(0.86, -10.7) * mm});
            skLineSegment(sketch, "E916", {"start": v(0.86, -10.7) * mm, "end": v(0.94, -10.8) * mm});
            skLineSegment(sketch, "E917", {"start": v(0.94, -10.8) * mm, "end": v(1.03, -10.9) * mm});
            skLineSegment(sketch, "E918", {"start": v(1.03, -10.9) * mm, "end": v(1.13, -11.01) * mm});
            skLineSegment(sketch, "E919", {"start": v(1.13, -11.01) * mm, "end": v(1.23, -11.12) * mm});
            skLineSegment(sketch, "E920", {"start": v(1.23, -11.12) * mm, "end": v(1.32, -11.17) * mm});
            skLineSegment(sketch, "E921", {"start": v(1.32, -11.17) * mm, "end": v(1.68, -11.12) * mm});
            skLineSegment(sketch, "E922", {"start": v(1.68, -11.12) * mm, "end": v(1.76, -11.05) * mm});
            skLineSegment(sketch, "E923", {"start": v(1.76, -11.05) * mm, "end": v(1.83, -10.92) * mm});
            skLineSegment(sketch, "E924", {"start": v(1.83, -10.92) * mm, "end": v(1.9, -10.8) * mm});
            skLineSegment(sketch, "E925", {"start": v(1.9, -10.8) * mm, "end": v(1.95, -10.67) * mm});
            skLineSegment(sketch, "E926", {"start": v(1.95, -10.67) * mm, "end": v(2, -10.55) * mm});
            skLineSegment(sketch, "E927", {"start": v(2, -10.55) * mm, "end": v(2.05, -10.43) * mm});
            skLineSegment(sketch, "E928", {"start": v(2.05, -10.43) * mm, "end": v(2.1, -10.31) * mm});
            skLineSegment(sketch, "E929", {"start": v(2.1, -10.31) * mm, "end": v(2.14, -10.2) * mm});
            skLineSegment(sketch, "E930", {"start": v(2.14, -10.2) * mm, "end": v(2.18, -10.09) * mm});
            skLineSegment(sketch, "E931", {"start": v(2.18, -10.09) * mm, "end": v(2.2, -9.98) * mm});
            skLineSegment(sketch, "E932", {"start": v(2.2, -9.98) * mm, "end": v(2.24, -9.88) * mm});
            skLineSegment(sketch, "E933", {"start": v(2.24, -9.88) * mm, "end": v(2.27, -9.78) * mm});
            skLineSegment(sketch, "E934", {"start": v(2.27, -9.78) * mm, "end": v(2.29, -9.68) * mm});
            skLineSegment(sketch, "E935", {"start": v(2.29, -9.68) * mm, "end": v(2.31, -9.6) * mm});
            skLineSegment(sketch, "E936", {"start": v(2.31, -9.6) * mm, "end": v(2.33, -9.5) * mm});
            skLineSegment(sketch, "E937", {"start": v(2.33, -9.5) * mm, "end": v(2.34, -9.42) * mm});
            skLineSegment(sketch, "E938", {"start": v(2.34, -9.42) * mm, "end": v(2.36, -9.34) * mm});
            skLineSegment(sketch, "E939", {"start": v(2.36, -9.34) * mm, "end": v(2.37, -9.26) * mm});
            skLineSegment(sketch, "E940", {"start": v(2.37, -9.26) * mm, "end": v(2.37, -9.19) * mm});
            skLineSegment(sketch, "E941", {"start": v(2.37, -9.19) * mm, "end": v(2.38, -9.12) * mm});
            skLineSegment(sketch, "E942", {"start": v(2.38, -9.12) * mm, "end": v(2.38, -9.05) * mm});
            skLineSegment(sketch, "E943", {"start": v(2.38, -9.05) * mm, "end": v(2.39, -9) * mm});
            skLineSegment(sketch, "E944", {"start": v(2.39, -9) * mm, "end": v(2.39, -8.94) * mm});
            skLineSegment(sketch, "E945", {"start": v(2.39, -8.94) * mm, "end": v(2.39, -8.89) * mm});
            skLineSegment(sketch, "E946", {"start": v(2.39, -8.89) * mm, "end": v(2.39, -8.84) * mm});
            skLineSegment(sketch, "E947", {"start": v(2.39, -8.84) * mm, "end": v(2.39, -8.8) * mm});
            skLineSegment(sketch, "E948", {"start": v(2.39, -8.8) * mm, "end": v(2.38, -8.75) * mm});
            skLineSegment(sketch, "E949", {"start": v(2.38, -8.75) * mm, "end": v(2.38, -8.72) * mm});
            skLineSegment(sketch, "E950", {"start": v(2.38, -8.72) * mm, "end": v(2.38, -8.69) * mm});
            skLineSegment(sketch, "E951", {"start": v(2.38, -8.69) * mm, "end": v(2.37, -8.66) * mm});
            skLineSegment(sketch, "E952", {"start": v(2.37, -8.66) * mm, "end": v(2.37, -8.64) * mm});
            skLineSegment(sketch, "E953", {"start": v(2.37, -8.64) * mm, "end": v(2.37, -8.62) * mm});
            skLineSegment(sketch, "E954", {"start": v(2.37, -8.62) * mm, "end": v(2.36, -8.6) * mm});
            skLineSegment(sketch, "E955", {"start": v(2.36, -8.6) * mm, "end": v(2.36, -8.6) * mm});
            skLineSegment(sketch, "E956", {"start": v(2.36, -8.6) * mm, "end": v(2.27, -8.26) * mm});
            skLineSegment(sketch, "E957", {"start": v(2.27, -8.26) * mm, "end": v(3.28, -7.91) * mm});
            skLineSegment(sketch, "E958", {"start": v(3.28, -7.91) * mm, "end": v(3.41, -8.23) * mm});
            skLineSegment(sketch, "E959", {"start": v(3.41, -8.23) * mm, "end": v(3.41, -8.24) * mm});
            skLineSegment(sketch, "E960", {"start": v(3.41, -8.24) * mm, "end": v(3.42, -8.25) * mm});
            skLineSegment(sketch, "E961", {"start": v(3.42, -8.25) * mm, "end": v(3.42, -8.26) * mm});
            skLineSegment(sketch, "E962", {"start": v(3.42, -8.26) * mm, "end": v(3.43, -8.28) * mm});
            skLineSegment(sketch, "E963", {"start": v(3.43, -8.28) * mm, "end": v(3.44, -8.3) * mm});
            skLineSegment(sketch, "E964", {"start": v(3.44, -8.3) * mm, "end": v(3.46, -8.32) * mm});
            skLineSegment(sketch, "E965", {"start": v(3.46, -8.32) * mm, "end": v(3.47, -8.34) * mm});
            skLineSegment(sketch, "E966", {"start": v(3.47, -8.34) * mm, "end": v(3.5, -8.37) * mm});
            skLineSegment(sketch, "E967", {"start": v(3.5, -8.37) * mm, "end": v(3.51, -8.4) * mm});
            skLineSegment(sketch, "E968", {"start": v(3.51, -8.4) * mm, "end": v(3.54, -8.44) * mm});
            skLineSegment(sketch, "E969", {"start": v(3.54, -8.44) * mm, "end": v(3.57, -8.48) * mm});
            skLineSegment(sketch, "E970", {"start": v(3.57, -8.48) * mm, "end": v(3.6, -8.52) * mm});
            skLineSegment(sketch, "E971", {"start": v(3.6, -8.52) * mm, "end": v(3.63, -8.57) * mm});
            skLineSegment(sketch, "E972", {"start": v(3.63, -8.57) * mm, "end": v(3.67, -8.61) * mm});
            skLineSegment(sketch, "E973", {"start": v(3.67, -8.61) * mm, "end": v(3.72, -8.66) * mm});
            skLineSegment(sketch, "E974", {"start": v(3.72, -8.66) * mm, "end": v(3.76, -8.71) * mm});
            skLineSegment(sketch, "E975", {"start": v(3.76, -8.71) * mm, "end": v(3.82, -8.76) * mm});
            skLineSegment(sketch, "E976", {"start": v(3.82, -8.76) * mm, "end": v(3.87, -8.82) * mm});
            skLineSegment(sketch, "E977", {"start": v(3.87, -8.82) * mm, "end": v(3.93, -8.87) * mm});
            skLineSegment(sketch, "E978", {"start": v(3.93, -8.87) * mm, "end": v(4, -8.93) * mm});
            skLineSegment(sketch, "E979", {"start": v(4, -8.93) * mm, "end": v(4.06, -9) * mm});
            skLineSegment(sketch, "E980", {"start": v(4.06, -9) * mm, "end": v(4.14, -9.05) * mm});
            skLineSegment(sketch, "E981", {"start": v(4.14, -9.05) * mm, "end": v(4.21, -9.11) * mm});
            skLineSegment(sketch, "E982", {"start": v(4.21, -9.11) * mm, "end": v(4.3, -9.18) * mm});
            skLineSegment(sketch, "E983", {"start": v(4.3, -9.18) * mm, "end": v(4.38, -9.24) * mm});
            skLineSegment(sketch, "E984", {"start": v(4.38, -9.24) * mm, "end": v(4.47, -9.3) * mm});
            skLineSegment(sketch, "E985", {"start": v(4.47, -9.3) * mm, "end": v(4.57, -9.37) * mm});
            skLineSegment(sketch, "E986", {"start": v(4.57, -9.37) * mm, "end": v(4.67, -9.43) * mm});
            skLineSegment(sketch, "E987", {"start": v(4.67, -9.43) * mm, "end": v(4.78, -9.5) * mm});
            skLineSegment(sketch, "E988", {"start": v(4.78, -9.5) * mm, "end": v(4.9, -9.56) * mm});
            skLineSegment(sketch, "E989", {"start": v(4.9, -9.56) * mm, "end": v(5, -9.62) * mm});
            skLineSegment(sketch, "E990", {"start": v(5, -9.62) * mm, "end": v(5.13, -9.68) * mm});
            skLineSegment(sketch, "E991", {"start": v(5.13, -9.68) * mm, "end": v(5.26, -9.74) * mm});
            skLineSegment(sketch, "E992", {"start": v(5.26, -9.74) * mm, "end": v(5.39, -9.8) * mm});
            skLineSegment(sketch, "E993", {"start": v(5.39, -9.8) * mm, "end": v(5.5, -9.81) * mm});
            skLineSegment(sketch, "E994", {"start": v(5.5, -9.81) * mm, "end": v(5.81, -9.63) * mm});
            skLineSegment(sketch, "E995", {"start": v(5.81, -9.63) * mm, "end": v(5.86, -9.53) * mm});
            skLineSegment(sketch, "E996", {"start": v(5.86, -9.53) * mm, "end": v(5.87, -9.39) * mm});
            skLineSegment(sketch, "E997", {"start": v(5.87, -9.39) * mm, "end": v(5.88, -9.25) * mm});
            skLineSegment(sketch, "E998", {"start": v(5.88, -9.25) * mm, "end": v(5.88, -9.1) * mm});
            skLineSegment(sketch, "E999", {"start": v(5.88, -9.1) * mm, "end": v(5.89, -8.98) * mm});
            skLineSegment(sketch, "E1000", {"start": v(5.89, -8.98) * mm, "end": v(5.89, -8.85) * mm});
            skLineSegment(sketch, "E1001", {"start": v(5.89, -8.85) * mm, "end": v(5.88, -8.72) * mm});
            skLineSegment(sketch, "E1002", {"start": v(5.88, -8.72) * mm, "end": v(5.88, -8.6) * mm});
            skLineSegment(sketch, "E1003", {"start": v(5.88, -8.6) * mm, "end": v(5.87, -8.49) * mm});
            skLineSegment(sketch, "E1004", {"start": v(5.87, -8.49) * mm, "end": v(5.86, -8.38) * mm});
            skLineSegment(sketch, "E1005", {"start": v(5.86, -8.38) * mm, "end": v(5.85, -8.27) * mm});
            skLineSegment(sketch, "E1006", {"start": v(5.85, -8.27) * mm, "end": v(5.84, -8.17) * mm});
            skLineSegment(sketch, "E1007", {"start": v(5.84, -8.17) * mm, "end": v(5.82, -8.07) * mm});
            skLineSegment(sketch, "E1008", {"start": v(5.82, -8.07) * mm, "end": v(5.8, -7.98) * mm});
            skLineSegment(sketch, "E1009", {"start": v(5.8, -7.98) * mm, "end": v(5.79, -7.89) * mm});
            skLineSegment(sketch, "E1010", {"start": v(5.79, -7.89) * mm, "end": v(5.77, -7.8) * mm});
            skLineSegment(sketch, "E1011", {"start": v(5.77, -7.8) * mm, "end": v(5.75, -7.73) * mm});
            skLineSegment(sketch, "E1012", {"start": v(5.75, -7.73) * mm, "end": v(5.73, -7.65) * mm});
            skLineSegment(sketch, "E1013", {"start": v(5.73, -7.65) * mm, "end": v(5.7, -7.58) * mm});
            skLineSegment(sketch, "E1014", {"start": v(5.7, -7.58) * mm, "end": v(5.69, -7.51) * mm});
            skLineSegment(sketch, "E1015", {"start": v(5.69, -7.51) * mm, "end": v(5.67, -7.45) * mm});
            skLineSegment(sketch, "E1016", {"start": v(5.67, -7.45) * mm, "end": v(5.65, -7.4) * mm});
            skLineSegment(sketch, "E1017", {"start": v(5.65, -7.4) * mm, "end": v(5.63, -7.34) * mm});
            skLineSegment(sketch, "E1018", {"start": v(5.63, -7.34) * mm, "end": v(5.6, -7.3) * mm});
            skLineSegment(sketch, "E1019", {"start": v(5.6, -7.3) * mm, "end": v(5.59, -7.25) * mm});
            skLineSegment(sketch, "E1020", {"start": v(5.59, -7.25) * mm, "end": v(5.57, -7.21) * mm});
            skLineSegment(sketch, "E1021", {"start": v(5.57, -7.21) * mm, "end": v(5.55, -7.18) * mm});
            skLineSegment(sketch, "E1022", {"start": v(5.55, -7.18) * mm, "end": v(5.54, -7.15) * mm});
            skLineSegment(sketch, "E1023", {"start": v(5.54, -7.15) * mm, "end": v(5.52, -7.12) * mm});
            skLineSegment(sketch, "E1024", {"start": v(5.52, -7.12) * mm, "end": v(5.5, -7.1) * mm});
            skLineSegment(sketch, "E1025", {"start": v(5.5, -7.1) * mm, "end": v(5.5, -7.08) * mm});
            skLineSegment(sketch, "E1026", {"start": v(5.5, -7.08) * mm, "end": v(5.49, -7.06) * mm});
            skLineSegment(sketch, "E1027", {"start": v(5.49, -7.06) * mm, "end": v(5.48, -7.05) * mm});
            skLineSegment(sketch, "E1028", {"start": v(5.48, -7.05) * mm, "end": v(5.47, -7.04) * mm});
            skLineSegment(sketch, "E1029", {"start": v(5.47, -7.04) * mm, "end": v(5.47, -7.04) * mm});
            skLineSegment(sketch, "E1030", {"start": v(5.47, -7.04) * mm, "end": v(5.25, -6.76) * mm});
            skLineSegment(sketch, "E1031", {"start": v(5.25, -6.76) * mm, "end": v(6.05, -6.05) * mm});
            skLineSegment(sketch, "E1032", {"start": v(6.05, -6.05) * mm, "end": v(6.3, -6.3) * mm});
            skLineSegment(sketch, "E1033", {"start": v(6.3, -6.3) * mm, "end": v(6.3, -6.3) * mm});
            skLineSegment(sketch, "E1034", {"start": v(6.3, -6.3) * mm, "end": v(6.31, -6.31) * mm});
            skLineSegment(sketch, "E1035", {"start": v(6.31, -6.31) * mm, "end": v(6.32, -6.32) * mm});
            skLineSegment(sketch, "E1036", {"start": v(6.32, -6.32) * mm, "end": v(6.34, -6.33) * mm});
            skLineSegment(sketch, "E1037", {"start": v(6.34, -6.33) * mm, "end": v(6.35, -6.35) * mm});
            skLineSegment(sketch, "E1038", {"start": v(6.35, -6.35) * mm, "end": v(6.38, -6.36) * mm});
            skLineSegment(sketch, "E1039", {"start": v(6.38, -6.36) * mm, "end": v(6.4, -6.38) * mm});
            skLineSegment(sketch, "E1040", {"start": v(6.4, -6.38) * mm, "end": v(6.43, -6.4) * mm});
            skLineSegment(sketch, "E1041", {"start": v(6.43, -6.4) * mm, "end": v(6.46, -6.42) * mm});
            skLineSegment(sketch, "E1042", {"start": v(6.46, -6.42) * mm, "end": v(6.5, -6.45) * mm});
            skLineSegment(sketch, "E1043", {"start": v(6.5, -6.45) * mm, "end": v(6.54, -6.47) * mm});
            skLineSegment(sketch, "E1044", {"start": v(6.54, -6.47) * mm, "end": v(6.59, -6.5) * mm});
            skLineSegment(sketch, "E1045", {"start": v(6.59, -6.5) * mm, "end": v(6.64, -6.52) * mm});
            skLineSegment(sketch, "E1046", {"start": v(6.64, -6.52) * mm, "end": v(6.7, -6.55) * mm});
            skLineSegment(sketch, "E1047", {"start": v(6.7, -6.55) * mm, "end": v(6.75, -6.58) * mm});
            skLineSegment(sketch, "E1048", {"start": v(6.75, -6.58) * mm, "end": v(6.81, -6.6) * mm});
            skLineSegment(sketch, "E1049", {"start": v(6.81, -6.6) * mm, "end": v(6.88, -6.64) * mm});
            skLineSegment(sketch, "E1050", {"start": v(6.88, -6.64) * mm, "end": v(6.95, -6.67) * mm});
            skLineSegment(sketch, "E1051", {"start": v(6.95, -6.67) * mm, "end": v(7.03, -6.7) * mm});
            skLineSegment(sketch, "E1052", {"start": v(7.03, -6.7) * mm, "end": v(7.1, -6.72) * mm});
            skLineSegment(sketch, "E1053", {"start": v(7.1, -6.72) * mm, "end": v(7.2, -6.75) * mm});
            skLineSegment(sketch, "E1054", {"start": v(7.2, -6.75) * mm, "end": v(7.28, -6.78) * mm});
            skLineSegment(sketch, "E1055", {"start": v(7.28, -6.78) * mm, "end": v(7.38, -6.8) * mm});
            skLineSegment(sketch, "E1056", {"start": v(7.38, -6.8) * mm, "end": v(7.48, -6.83) * mm});
            skLineSegment(sketch, "E1057", {"start": v(7.48, -6.83) * mm, "end": v(7.58, -6.86) * mm});
            skLineSegment(sketch, "E1058", {"start": v(7.58, -6.86) * mm, "end": v(7.7, -6.88) * mm});
            skLineSegment(sketch, "E1059", {"start": v(7.7, -6.88) * mm, "end": v(7.8, -6.9) * mm});
            skLineSegment(sketch, "E1060", {"start": v(7.8, -6.9) * mm, "end": v(7.92, -6.92) * mm});
            skLineSegment(sketch, "E1061", {"start": v(7.92, -6.92) * mm, "end": v(8.05, -6.94) * mm});
            skLineSegment(sketch, "E1062", {"start": v(8.05, -6.94) * mm, "end": v(8.18, -6.96) * mm});
            skLineSegment(sketch, "E1063", {"start": v(8.18, -6.96) * mm, "end": v(8.3, -6.97) * mm});
            skLineSegment(sketch, "E1064", {"start": v(8.3, -6.97) * mm, "end": v(8.44, -6.98) * mm});
            skLineSegment(sketch, "E1065", {"start": v(8.44, -6.98) * mm, "end": v(8.58, -7) * mm});
            skLineSegment(sketch, "E1066", {"start": v(8.58, -7) * mm, "end": v(8.73, -7) * mm});
            skLineSegment(sketch, "E1067", {"start": v(8.73, -7) * mm, "end": v(8.84, -6.96) * mm});
            skLineSegment(sketch, "E1068", {"start": v(8.84, -6.96) * mm, "end": v(9.05, -6.68) * mm});
            skLineSegment(sketch, "E1069", {"start": v(9.05, -6.68) * mm, "end": v(9.06, -6.57) * mm});
            skLineSegment(sketch, "E1070", {"start": v(9.06, -6.57) * mm, "end": v(9.01, -6.43) * mm});
            skLineSegment(sketch, "E1071", {"start": v(9.01, -6.43) * mm, "end": v(8.97, -6.3) * mm});
            skLineSegment(sketch, "E1072", {"start": v(8.97, -6.3) * mm, "end": v(8.92, -6.16) * mm});
            skLineSegment(sketch, "E1073", {"start": v(8.92, -6.16) * mm, "end": v(8.87, -6.04) * mm});
            skLineSegment(sketch, "E1074", {"start": v(8.87, -6.04) * mm, "end": v(8.82, -5.92) * mm});
            skLineSegment(sketch, "E1075", {"start": v(8.82, -5.92) * mm, "end": v(8.77, -5.8) * mm});
            skLineSegment(sketch, "E1076", {"start": v(8.77, -5.8) * mm, "end": v(8.72, -5.7) * mm});
            skLineSegment(sketch, "E1077", {"start": v(8.72, -5.7) * mm, "end": v(8.67, -5.6) * mm});
            skLineSegment(sketch, "E1078", {"start": v(8.67, -5.6) * mm, "end": v(8.62, -5.5) * mm});
            skLineSegment(sketch, "E1079", {"start": v(8.62, -5.5) * mm, "end": v(8.57, -5.4) * mm});
            skLineSegment(sketch, "E1080", {"start": v(8.57, -5.4) * mm, "end": v(8.52, -5.31) * mm});
            skLineSegment(sketch, "E1081", {"start": v(8.52, -5.31) * mm, "end": v(8.47, -5.23) * mm});
            skLineSegment(sketch, "E1082", {"start": v(8.47, -5.23) * mm, "end": v(8.42, -5.15) * mm});
            skLineSegment(sketch, "E1083", {"start": v(8.42, -5.15) * mm, "end": v(8.37, -5.07) * mm});
            skLineSegment(sketch, "E1084", {"start": v(8.37, -5.07) * mm, "end": v(8.32, -5) * mm});
            skLineSegment(sketch, "E1085", {"start": v(8.32, -5) * mm, "end": v(8.27, -4.94) * mm});
            skLineSegment(sketch, "E1086", {"start": v(8.27, -4.94) * mm, "end": v(8.22, -4.88) * mm});
            skLineSegment(sketch, "E1087", {"start": v(8.22, -4.88) * mm, "end": v(8.18, -4.82) * mm});
            skLineSegment(sketch, "E1088", {"start": v(8.18, -4.82) * mm, "end": v(8.13, -4.77) * mm});
            skLineSegment(sketch, "E1089", {"start": v(8.13, -4.77) * mm, "end": v(8.09, -4.72) * mm});
            skLineSegment(sketch, "E1090", {"start": v(8.09, -4.72) * mm, "end": v(8.05, -4.67) * mm});
            skLineSegment(sketch, "E1091", {"start": v(8.05, -4.67) * mm, "end": v(8, -4.63) * mm});
            skLineSegment(sketch, "E1092", {"start": v(8, -4.63) * mm, "end": v(7.97, -4.6) * mm});
            skLineSegment(sketch, "E1093", {"start": v(7.97, -4.6) * mm, "end": v(7.94, -4.56) * mm});
            skLineSegment(sketch, "E1094", {"start": v(7.94, -4.56) * mm, "end": v(7.9, -4.53) * mm});
            skLineSegment(sketch, "E1095", {"start": v(7.9, -4.53) * mm, "end": v(7.87, -4.5) * mm});
            skLineSegment(sketch, "E1096", {"start": v(7.87, -4.5) * mm, "end": v(7.85, -4.48) * mm});
            skLineSegment(sketch, "E1097", {"start": v(7.85, -4.48) * mm, "end": v(7.82, -4.46) * mm});
            skLineSegment(sketch, "E1098", {"start": v(7.82, -4.46) * mm, "end": v(7.8, -4.45) * mm});
            skLineSegment(sketch, "E1099", {"start": v(7.8, -4.45) * mm, "end": v(7.78, -4.43) * mm});
            skLineSegment(sketch, "E1100", {"start": v(7.78, -4.43) * mm, "end": v(7.77, -4.42) * mm});
            skLineSegment(sketch, "E1101", {"start": v(7.77, -4.42) * mm, "end": v(7.76, -4.42) * mm});
            skLineSegment(sketch, "E1102", {"start": v(7.76, -4.42) * mm, "end": v(7.75, -4.41) * mm});
            skLineSegment(sketch, "E1103", {"start": v(7.75, -4.41) * mm, "end": v(7.75, -4.4) * mm});
            skLineSegment(sketch, "E1104", {"start": v(7.75, -4.4) * mm, "end": v(7.44, -4.24) * mm});
            skLineSegment(sketch, "E1105", {"start": v(7.44, -4.24) * mm, "end": v(7.91, -3.28) * mm});
            skLineSegment(sketch, "E1106", {"start": v(7.91, -3.28) * mm, "end": v(8.23, -3.41) * mm});
            skLineSegment(sketch, "E1107", {"start": v(8.23, -3.41) * mm, "end": v(8.24, -3.41) * mm});
            skLineSegment(sketch, "E1108", {"start": v(8.24, -3.41) * mm, "end": v(8.25, -3.42) * mm});
            skLineSegment(sketch, "E1109", {"start": v(8.25, -3.42) * mm, "end": v(8.26, -3.42) * mm});
            skLineSegment(sketch, "E1110", {"start": v(8.26, -3.42) * mm, "end": v(8.28, -3.43) * mm});
            skLineSegment(sketch, "E1111", {"start": v(8.28, -3.43) * mm, "end": v(8.3, -3.43) * mm});
            skLineSegment(sketch, "E1112", {"start": v(8.3, -3.43) * mm, "end": v(8.33, -3.44) * mm});
            skLineSegment(sketch, "E1113", {"start": v(8.33, -3.44) * mm, "end": v(8.36, -3.45) * mm});
            skLineSegment(sketch, "E1114", {"start": v(8.36, -3.45) * mm, "end": v(8.4, -3.45) * mm});
            skLineSegment(sketch, "E1115", {"start": v(8.4, -3.45) * mm, "end": v(8.43, -3.46) * mm});
            skLineSegment(sketch, "E1116", {"start": v(8.43, -3.46) * mm, "end": v(8.47, -3.47) * mm});
            skLineSegment(sketch, "E1117", {"start": v(8.47, -3.47) * mm, "end": v(8.52, -3.47) * mm});
            skLineSegment(sketch, "E1118", {"start": v(8.52, -3.47) * mm, "end": v(8.57, -3.48) * mm});
            skLineSegment(sketch, "E1119", {"start": v(8.57, -3.48) * mm, "end": v(8.63, -3.49) * mm});
            skLineSegment(sketch, "E1120", {"start": v(8.63, -3.49) * mm, "end": v(8.69, -3.5) * mm});
            skLineSegment(sketch, "E1121", {"start": v(8.69, -3.5) * mm, "end": v(8.75, -3.5) * mm});
            skLineSegment(sketch, "E1122", {"start": v(8.75, -3.5) * mm, "end": v(8.82, -3.5) * mm});
            skLineSegment(sketch, "E1123", {"start": v(8.82, -3.5) * mm, "end": v(8.9, -3.5) * mm});
            skLineSegment(sketch, "E1124", {"start": v(8.9, -3.5) * mm, "end": v(8.97, -3.5) * mm});
            skLineSegment(sketch, "E1125", {"start": v(8.97, -3.5) * mm, "end": v(9.05, -3.5) * mm});
            skLineSegment(sketch, "E1126", {"start": v(9.05, -3.5) * mm, "end": v(9.14, -3.5) * mm});
            skLineSegment(sketch, "E1127", {"start": v(9.14, -3.5) * mm, "end": v(9.23, -3.49) * mm});
            skLineSegment(sketch, "E1128", {"start": v(9.23, -3.49) * mm, "end": v(9.32, -3.48) * mm});
            skLineSegment(sketch, "E1129", {"start": v(9.32, -3.48) * mm, "end": v(9.42, -3.47) * mm});
            skLineSegment(sketch, "E1130", {"start": v(9.42, -3.47) * mm, "end": v(9.52, -3.45) * mm});
            skLineSegment(sketch, "E1131", {"start": v(9.52, -3.45) * mm, "end": v(9.63, -3.43) * mm});
            skLineSegment(sketch, "E1132", {"start": v(9.63, -3.43) * mm, "end": v(9.74, -3.41) * mm});
            skLineSegment(sketch, "E1133", {"start": v(9.74, -3.41) * mm, "end": v(9.85, -3.4) * mm});
            skLineSegment(sketch, "E1134", {"start": v(9.85, -3.4) * mm, "end": v(9.97, -3.36) * mm});
            skLineSegment(sketch, "E1135", {"start": v(9.97, -3.36) * mm, "end": v(10.1, -3.33) * mm});
            skLineSegment(sketch, "E1136", {"start": v(10.1, -3.33) * mm, "end": v(10.22, -3.3) * mm});
            skLineSegment(sketch, "E1137", {"start": v(10.22, -3.3) * mm, "end": v(10.34, -3.26) * mm});
            skLineSegment(sketch, "E1138", {"start": v(10.34, -3.26) * mm, "end": v(10.47, -3.22) * mm});
            skLineSegment(sketch, "E1139", {"start": v(10.47, -3.22) * mm, "end": v(10.6, -3.17) * mm});
            skLineSegment(sketch, "E1140", {"start": v(10.6, -3.17) * mm, "end": v(10.74, -3.12) * mm});
            skLineSegment(sketch, "E1141", {"start": v(10.74, -3.12) * mm, "end": v(10.83, -3.05) * mm});
            skLineSegment(sketch, "E1142", {"start": v(10.83, -3.05) * mm, "end": v(10.92, -2.7) * mm});
            skLineSegment(sketch, "E1143", {"start": v(10.92, -2.7) * mm, "end": v(10.88, -2.6) * mm});
            skLineSegment(sketch, "E1144", {"start": v(10.88, -2.6) * mm, "end": v(10.79, -2.49) * mm});
            skLineSegment(sketch, "E1145", {"start": v(10.79, -2.49) * mm, "end": v(10.7, -2.38) * mm});
            skLineSegment(sketch, "E1146", {"start": v(10.7, -2.38) * mm, "end": v(10.6, -2.28) * mm});
            skLineSegment(sketch, "E1147", {"start": v(10.6, -2.28) * mm, "end": v(10.51, -2.18) * mm});
            skLineSegment(sketch, "E1148", {"start": v(10.51, -2.18) * mm, "end": v(10.42, -2.1) * mm});
            skLineSegment(sketch, "E1149", {"start": v(10.42, -2.1) * mm, "end": v(10.33, -2) * mm});
            skLineSegment(sketch, "E1150", {"start": v(10.33, -2) * mm, "end": v(10.24, -1.93) * mm});
            skLineSegment(sketch, "E1151", {"start": v(10.24, -1.93) * mm, "end": v(10.15, -1.85) * mm});
            skLineSegment(sketch, "E1152", {"start": v(10.15, -1.85) * mm, "end": v(10.07, -1.78) * mm});
            skLineSegment(sketch, "E1153", {"start": v(10.07, -1.78) * mm, "end": v(9.98, -1.71) * mm});
            skLineSegment(sketch, "E1154", {"start": v(9.98, -1.71) * mm, "end": v(9.9, -1.65) * mm});
            skLineSegment(sketch, "E1155", {"start": v(9.9, -1.65) * mm, "end": v(9.82, -1.6) * mm});
            skLineSegment(sketch, "E1156", {"start": v(9.82, -1.6) * mm, "end": v(9.75, -1.54) * mm});
            skLineSegment(sketch, "E1157", {"start": v(9.75, -1.54) * mm, "end": v(9.67, -1.49) * mm});
            skLineSegment(sketch, "E1158", {"start": v(9.67, -1.49) * mm, "end": v(9.6, -1.44) * mm});
            skLineSegment(sketch, "E1159", {"start": v(9.6, -1.44) * mm, "end": v(9.53, -1.4) * mm});
            skLineSegment(sketch, "E1160", {"start": v(9.53, -1.4) * mm, "end": v(9.46, -1.36) * mm});
            skLineSegment(sketch, "E1161", {"start": v(9.46, -1.36) * mm, "end": v(9.4, -1.32) * mm});
            skLineSegment(sketch, "E1162", {"start": v(9.4, -1.32) * mm, "end": v(9.34, -1.3) * mm});
            skLineSegment(sketch, "E1163", {"start": v(9.34, -1.3) * mm, "end": v(9.28, -1.26) * mm});
            skLineSegment(sketch, "E1164", {"start": v(9.28, -1.26) * mm, "end": v(9.22, -1.24) * mm});
            skLineSegment(sketch, "E1165", {"start": v(9.22, -1.24) * mm, "end": v(9.17, -1.21) * mm});
            skLineSegment(sketch, "E1166", {"start": v(9.17, -1.21) * mm, "end": v(9.12, -1.2) * mm});
            skLineSegment(sketch, "E1167", {"start": v(9.12, -1.2) * mm, "end": v(9.08, -1.18) * mm});
            skLineSegment(sketch, "E1168", {"start": v(9.08, -1.18) * mm, "end": v(9.04, -1.16) * mm});
            skLineSegment(sketch, "E1169", {"start": v(9.04, -1.16) * mm, "end": v(9, -1.15) * mm});
            skLineSegment(sketch, "E1170", {"start": v(9, -1.15) * mm, "end": v(8.97, -1.14) * mm});
            skLineSegment(sketch, "E1171", {"start": v(8.97, -1.14) * mm, "end": v(8.94, -1.13) * mm});
            skLineSegment(sketch, "E1172", {"start": v(8.94, -1.13) * mm, "end": v(8.91, -1.12) * mm});
            skLineSegment(sketch, "E1173", {"start": v(8.91, -1.12) * mm, "end": v(8.89, -1.12) * mm});
            skLineSegment(sketch, "E1174", {"start": v(8.89, -1.12) * mm, "end": v(8.87, -1.11) * mm});
            skLineSegment(sketch, "E1175", {"start": v(8.87, -1.11) * mm, "end": v(8.86, -1.11) * mm});
            skLineSegment(sketch, "E1176", {"start": v(8.86, -1.11) * mm, "end": v(8.85, -1.1) * mm});
            skLineSegment(sketch, "E1177", {"start": v(8.85, -1.1) * mm, "end": v(8.84, -1.1) * mm});
            skLineSegment(sketch, "E1178", {"start": v(8.84, -1.1) * mm, "end": v(8.5, -1.06) * mm});
            skLineSegment(sketch, "E1179", {"start": v(8.5, -1.06) * mm, "end": v(8.56, 0) * mm});
            skSolve(sketch);
        }
        {
            var Q0;
            Q0 = qSketchRegion(id + "F0", true);
            extrude(context, id + "F1", {"entities" : qUnion([Q0]), "depth" : 10 * mm});
        }
        {
            var Q0;
            Q0=qCreatedBy(makeId("Top.planeOp"),FACE);
            var sketch = newSketch(context, id + "F2", { "sketchPlane" : qUnion([Q0])});
            skCircle(sketch, "E1180", {"center": v(0, 0) * mm, "radius": 7.5 * mm});
            skSolve(sketch);
        }
        {
            var Q0;
            Q0 = qSketchRegion(id + "F2", true);
            extrude(context, id + "F3", {"entities" : qUnion([Q0]), "operationType" : NewBodyOperationType.REMOVE, "depth" : 5.5 * mm});
        }
        {
            var Q0;
            Q0=makeQuery(id+"F1.opExtrude","CAP_FACE",FACE,{"disambiguationData":[OSD([sQuery(id+"F0.wireOp",EDGE,"E0"),sQuery(id+"F0.wireOp",EDGE,"E1"),sQuery(id+"F0.wireOp",EDGE,"E2"),sQuery(id+"F0.wireOp",EDGE,"E3"),sQuery(id+"F0.wireOp",EDGE,"E4"),sQuery(id+"F0.wireOp",EDGE,"E5"),sQuery(id+"F0.wireOp",EDGE,"E6"),sQuery(id+"F0.wireOp",EDGE,"E7"),sQuery(id+"F0.wireOp",EDGE,"E8"),sQuery(id+"F0.wireOp",EDGE,"E9"),sQuery(id+"F0.wireOp",EDGE,"E10"),sQuery(id+"F0.wireOp",EDGE,"E11"),sQuery(id+"F0.wireOp",EDGE,"E12"),sQuery(id+"F0.wireOp",EDGE,"E13"),sQuery(id+"F0.wireOp",EDGE,"E14"),sQuery(id+"F0.wireOp",EDGE,"E15"),sQuery(id+"F0.wireOp",EDGE,"E16"),sQuery(id+"F0.wireOp",EDGE,"E17"),sQuery(id+"F0.wireOp",EDGE,"E18"),sQuery(id+"F0.wireOp",EDGE,"E19"),sQuery(id+"F0.wireOp",EDGE,"E20"),sQuery(id+"F0.wireOp",EDGE,"E21"),sQuery(id+"F0.wireOp",EDGE,"E22"),sQuery(id+"F0.wireOp",EDGE,"E23"),sQuery(id+"F0.wireOp",EDGE,"E24"),sQuery(id+"F0.wireOp",EDGE,"E25"),sQuery(id+"F0.wireOp",EDGE,"E26"),sQuery(id+"F0.wireOp",EDGE,"E27"),sQuery(id+"F0.wireOp",EDGE,"E28"),sQuery(id+"F0.wireOp",EDGE,"E29"),sQuery(id+"F0.wireOp",EDGE,"E30"),sQuery(id+"F0.wireOp",EDGE,"E31"),sQuery(id+"F0.wireOp",EDGE,"E32"),sQuery(id+"F0.wireOp",EDGE,"E33"),sQuery(id+"F0.wireOp",EDGE,"E34"),sQuery(id+"F0.wireOp",EDGE,"E35"),sQuery(id+"F0.wireOp",EDGE,"E36"),sQuery(id+"F0.wireOp",EDGE,"E37"),sQuery(id+"F0.wireOp",EDGE,"E38"),sQuery(id+"F0.wireOp",EDGE,"E39"),sQuery(id+"F0.wireOp",EDGE,"E40"),sQuery(id+"F0.wireOp",EDGE,"E41"),sQuery(id+"F0.wireOp",EDGE,"E42"),sQuery(id+"F0.wireOp",EDGE,"E43"),sQuery(id+"F0.wireOp",EDGE,"E44"),sQuery(id+"F0.wireOp",EDGE,"E45"),sQuery(id+"F0.wireOp",EDGE,"E46"),sQuery(id+"F0.wireOp",EDGE,"E47"),sQuery(id+"F0.wireOp",EDGE,"E48"),sQuery(id+"F0.wireOp",EDGE,"E49"),sQuery(id+"F0.wireOp",EDGE,"E50"),sQuery(id+"F0.wireOp",EDGE,"E51"),sQuery(id+"F0.wireOp",EDGE,"E52"),sQuery(id+"F0.wireOp",EDGE,"E53"),sQuery(id+"F0.wireOp",EDGE,"E54"),sQuery(id+"F0.wireOp",EDGE,"E55"),sQuery(id+"F0.wireOp",EDGE,"E56"),sQuery(id+"F0.wireOp",EDGE,"E57"),sQuery(id+"F0.wireOp",EDGE,"E58"),sQuery(id+"F0.wireOp",EDGE,"E59"),sQuery(id+"F0.wireOp",EDGE,"E60"),sQuery(id+"F0.wireOp",EDGE,"E61"),sQuery(id+"F0.wireOp",EDGE,"E62"),sQuery(id+"F0.wireOp",EDGE,"E63"),sQuery(id+"F0.wireOp",EDGE,"E64"),sQuery(id+"F0.wireOp",EDGE,"E65"),sQuery(id+"F0.wireOp",EDGE,"E66"),sQuery(id+"F0.wireOp",EDGE,"E67"),sQuery(id+"F0.wireOp",EDGE,"E68"),sQuery(id+"F0.wireOp",EDGE,"E69"),sQuery(id+"F0.wireOp",EDGE,"E70"),sQuery(id+"F0.wireOp",EDGE,"E70"),sQuery(id+"F0.wireOp",EDGE,"E71"),sQuery(id+"F0.wireOp",EDGE,"E72"),sQuery(id+"F0.wireOp",EDGE,"E73"),sQuery(id+"F0.wireOp",EDGE,"E74"),sQuery(id+"F0.wireOp",EDGE,"E75"),sQuery(id+"F0.wireOp",EDGE,"E76"),sQuery(id+"F0.wireOp",EDGE,"E77"),sQuery(id+"F0.wireOp",EDGE,"E78"),sQuery(id+"F0.wireOp",EDGE,"E79"),sQuery(id+"F0.wireOp",EDGE,"E80"),sQuery(id+"F0.wireOp",EDGE,"E81"),sQuery(id+"F0.wireOp",EDGE,"E82"),sQuery(id+"F0.wireOp",EDGE,"E83"),sQuery(id+"F0.wireOp",EDGE,"E84"),sQuery(id+"F0.wireOp",EDGE,"E85"),sQuery(id+"F0.wireOp",EDGE,"E86"),sQuery(id+"F0.wireOp",EDGE,"E87"),sQuery(id+"F0.wireOp",EDGE,"E88"),sQuery(id+"F0.wireOp",EDGE,"E89"),sQuery(id+"F0.wireOp",EDGE,"E90"),sQuery(id+"F0.wireOp",EDGE,"E91"),sQuery(id+"F0.wireOp",EDGE,"E92"),sQuery(id+"F0.wireOp",EDGE,"E93"),sQuery(id+"F0.wireOp",EDGE,"E94"),sQuery(id+"F0.wireOp",EDGE,"E95"),sQuery(id+"F0.wireOp",EDGE,"E96"),sQuery(id+"F0.wireOp",EDGE,"E97"),sQuery(id+"F0.wireOp",EDGE,"E98"),sQuery(id+"F0.wireOp",EDGE,"E99"),sQuery(id+"F0.wireOp",EDGE,"E100"),sQuery(id+"F0.wireOp",EDGE,"E101"),sQuery(id+"F0.wireOp",EDGE,"E102"),sQuery(id+"F0.wireOp",EDGE,"E103"),sQuery(id+"F0.wireOp",EDGE,"E104"),sQuery(id+"F0.wireOp",EDGE,"E105"),sQuery(id+"F0.wireOp",EDGE,"E106"),sQuery(id+"F0.wireOp",EDGE,"E107"),sQuery(id+"F0.wireOp",EDGE,"E108"),sQuery(id+"F0.wireOp",EDGE,"E109"),sQuery(id+"F0.wireOp",EDGE,"E110"),sQuery(id+"F0.wireOp",EDGE,"E111"),sQuery(id+"F0.wireOp",EDGE,"E112"),sQuery(id+"F0.wireOp",EDGE,"E113"),sQuery(id+"F0.wireOp",EDGE,"E114"),sQuery(id+"F0.wireOp",EDGE,"E115"),sQuery(id+"F0.wireOp",EDGE,"E116"),sQuery(id+"F0.wireOp",EDGE,"E117"),sQuery(id+"F0.wireOp",EDGE,"E118"),sQuery(id+"F0.wireOp",EDGE,"E119"),sQuery(id+"F0.wireOp",EDGE,"E120"),sQuery(id+"F0.wireOp",EDGE,"E121"),sQuery(id+"F0.wireOp",EDGE,"E122"),sQuery(id+"F0.wireOp",EDGE,"E123"),sQuery(id+"F0.wireOp",EDGE,"E124"),sQuery(id+"F0.wireOp",EDGE,"E125"),sQuery(id+"F0.wireOp",EDGE,"E126"),sQuery(id+"F0.wireOp",EDGE,"E127"),sQuery(id+"F0.wireOp",EDGE,"E128"),sQuery(id+"F0.wireOp",EDGE,"E129"),sQuery(id+"F0.wireOp",EDGE,"E130"),sQuery(id+"F0.wireOp",EDGE,"E131"),sQuery(id+"F0.wireOp",EDGE,"E132"),sQuery(id+"F0.wireOp",EDGE,"E133"),sQuery(id+"F0.wireOp",EDGE,"E134"),sQuery(id+"F0.wireOp",EDGE,"E135"),sQuery(id+"F0.wireOp",EDGE,"E136"),sQuery(id+"F0.wireOp",EDGE,"E137"),sQuery(id+"F0.wireOp",EDGE,"E138"),sQuery(id+"F0.wireOp",EDGE,"E139"),sQuery(id+"F0.wireOp",EDGE,"E140"),sQuery(id+"F0.wireOp",EDGE,"E141"),sQuery(id+"F0.wireOp",EDGE,"E142"),sQuery(id+"F0.wireOp",EDGE,"E143"),sQuery(id+"F0.wireOp",EDGE,"E144"),sQuery(id+"F0.wireOp",EDGE,"E145"),sQuery(id+"F0.wireOp",EDGE,"E146"),sQuery(id+"F0.wireOp",EDGE,"E147"),sQuery(id+"F0.wireOp",EDGE,"E148"),sQuery(id+"F0.wireOp",EDGE,"E149"),sQuery(id+"F0.wireOp",EDGE,"E150"),sQuery(id+"F0.wireOp",EDGE,"E151"),sQuery(id+"F0.wireOp",EDGE,"E152"),sQuery(id+"F0.wireOp",EDGE,"E153"),sQuery(id+"F0.wireOp",EDGE,"E154"),sQuery(id+"F0.wireOp",EDGE,"E155"),sQuery(id+"F0.wireOp",EDGE,"E156"),sQuery(id+"F0.wireOp",EDGE,"E157"),sQuery(id+"F0.wireOp",EDGE,"E158"),sQuery(id+"F0.wireOp",EDGE,"E159"),sQuery(id+"F0.wireOp",EDGE,"E160"),sQuery(id+"F0.wireOp",EDGE,"E161"),sQuery(id+"F0.wireOp",EDGE,"E162"),sQuery(id+"F0.wireOp",EDGE,"E163"),sQuery(id+"F0.wireOp",EDGE,"E164"),sQuery(id+"F0.wireOp",EDGE,"E165"),sQuery(id+"F0.wireOp",EDGE,"E166"),sQuery(id+"F0.wireOp",EDGE,"E167"),sQuery(id+"F0.wireOp",EDGE,"E168"),sQuery(id+"F0.wireOp",EDGE,"E169"),sQuery(id+"F0.wireOp",EDGE,"E170"),sQuery(id+"F0.wireOp",EDGE,"E171"),sQuery(id+"F0.wireOp",EDGE,"E172"),sQuery(id+"F0.wireOp",EDGE,"E173"),sQuery(id+"F0.wireOp",EDGE,"E174"),sQuery(id+"F0.wireOp",EDGE,"E175"),sQuery(id+"F0.wireOp",EDGE,"E176"),sQuery(id+"F0.wireOp",EDGE,"E177"),sQuery(id+"F0.wireOp",EDGE,"E178"),sQuery(id+"F0.wireOp",EDGE,"E179"),sQuery(id+"F0.wireOp",EDGE,"E180"),sQuery(id+"F0.wireOp",EDGE,"E181"),sQuery(id+"F0.wireOp",EDGE,"E182"),sQuery(id+"F0.wireOp",EDGE,"E183"),sQuery(id+"F0.wireOp",EDGE,"E184"),sQuery(id+"F0.wireOp",EDGE,"E185"),sQuery(id+"F0.wireOp",EDGE,"E186"),sQuery(id+"F0.wireOp",EDGE,"E187"),sQuery(id+"F0.wireOp",EDGE,"E188"),sQuery(id+"F0.wireOp",EDGE,"E189"),sQuery(id+"F0.wireOp",EDGE,"E190"),sQuery(id+"F0.wireOp",EDGE,"E191"),sQuery(id+"F0.wireOp",EDGE,"E192"),sQuery(id+"F0.wireOp",EDGE,"E193"),sQuery(id+"F0.wireOp",EDGE,"E194"),sQuery(id+"F0.wireOp",EDGE,"E195"),sQuery(id+"F0.wireOp",EDGE,"E196"),sQuery(id+"F0.wireOp",EDGE,"E197"),sQuery(id+"F0.wireOp",EDGE,"E198"),sQuery(id+"F0.wireOp",EDGE,"E199"),sQuery(id+"F0.wireOp",EDGE,"E200"),sQuery(id+"F0.wireOp",EDGE,"E201"),sQuery(id+"F0.wireOp",EDGE,"E202"),sQuery(id+"F0.wireOp",EDGE,"E203"),sQuery(id+"F0.wireOp",EDGE,"E204"),sQuery(id+"F0.wireOp",EDGE,"E205"),sQuery(id+"F0.wireOp",EDGE,"E206"),sQuery(id+"F0.wireOp",EDGE,"E207"),sQuery(id+"F0.wireOp",EDGE,"E208"),sQuery(id+"F0.wireOp",EDGE,"E209"),sQuery(id+"F0.wireOp",EDGE,"E210"),sQuery(id+"F0.wireOp",EDGE,"E211"),sQuery(id+"F0.wireOp",EDGE,"E212"),sQuery(id+"F0.wireOp",EDGE,"E213"),sQuery(id+"F0.wireOp",EDGE,"E214"),sQuery(id+"F0.wireOp",EDGE,"E215"),sQuery(id+"F0.wireOp",EDGE,"E216"),sQuery(id+"F0.wireOp",EDGE,"E217"),sQuery(id+"F0.wireOp",EDGE,"E218"),sQuery(id+"F0.wireOp",EDGE,"E219"),sQuery(id+"F0.wireOp",EDGE,"E220"),sQuery(id+"F0.wireOp",EDGE,"E221"),sQuery(id+"F0.wireOp",EDGE,"E222"),sQuery(id+"F0.wireOp",EDGE,"E223"),sQuery(id+"F0.wireOp",EDGE,"E224"),sQuery(id+"F0.wireOp",EDGE,"E225"),sQuery(id+"F0.wireOp",EDGE,"E226"),sQuery(id+"F0.wireOp",EDGE,"E227"),sQuery(id+"F0.wireOp",EDGE,"E228"),sQuery(id+"F0.wireOp",EDGE,"E229"),sQuery(id+"F0.wireOp",EDGE,"E230"),sQuery(id+"F0.wireOp",EDGE,"E231"),sQuery(id+"F0.wireOp",EDGE,"E232"),sQuery(id+"F0.wireOp",EDGE,"E233"),sQuery(id+"F0.wireOp",EDGE,"E234"),sQuery(id+"F0.wireOp",EDGE,"E235"),sQuery(id+"F0.wireOp",EDGE,"E236"),sQuery(id+"F0.wireOp",EDGE,"E237"),sQuery(id+"F0.wireOp",EDGE,"E238"),sQuery(id+"F0.wireOp",EDGE,"E239"),sQuery(id+"F0.wireOp",EDGE,"E240"),sQuery(id+"F0.wireOp",EDGE,"E241"),sQuery(id+"F0.wireOp",EDGE,"E242"),sQuery(id+"F0.wireOp",EDGE,"E243"),sQuery(id+"F0.wireOp",EDGE,"E244"),sQuery(id+"F0.wireOp",EDGE,"E245"),sQuery(id+"F0.wireOp",EDGE,"E246"),sQuery(id+"F0.wireOp",EDGE,"E247"),sQuery(id+"F0.wireOp",EDGE,"E248"),sQuery(id+"F0.wireOp",EDGE,"E249"),sQuery(id+"F0.wireOp",EDGE,"E250"),sQuery(id+"F0.wireOp",EDGE,"E251"),sQuery(id+"F0.wireOp",EDGE,"E252"),sQuery(id+"F0.wireOp",EDGE,"E253"),sQuery(id+"F0.wireOp",EDGE,"E254"),sQuery(id+"F0.wireOp",EDGE,"E255"),sQuery(id+"F0.wireOp",EDGE,"E256"),sQuery(id+"F0.wireOp",EDGE,"E257"),sQuery(id+"F0.wireOp",EDGE,"E258"),sQuery(id+"F0.wireOp",EDGE,"E259"),sQuery(id+"F0.wireOp",EDGE,"E260"),sQuery(id+"F0.wireOp",EDGE,"E261"),sQuery(id+"F0.wireOp",EDGE,"E262"),sQuery(id+"F0.wireOp",EDGE,"E263"),sQuery(id+"F0.wireOp",EDGE,"E264"),sQuery(id+"F0.wireOp",EDGE,"E265"),sQuery(id+"F0.wireOp",EDGE,"E266"),sQuery(id+"F0.wireOp",EDGE,"E267"),sQuery(id+"F0.wireOp",EDGE,"E268"),sQuery(id+"F0.wireOp",EDGE,"E269"),sQuery(id+"F0.wireOp",EDGE,"E270"),sQuery(id+"F0.wireOp",EDGE,"E271"),sQuery(id+"F0.wireOp",EDGE,"E272"),sQuery(id+"F0.wireOp",EDGE,"E273"),sQuery(id+"F0.wireOp",EDGE,"E274"),sQuery(id+"F0.wireOp",EDGE,"E275"),sQuery(id+"F0.wireOp",EDGE,"E276"),sQuery(id+"F0.wireOp",EDGE,"E277"),sQuery(id+"F0.wireOp",EDGE,"E278"),sQuery(id+"F0.wireOp",EDGE,"E279"),sQuery(id+"F0.wireOp",EDGE,"E280"),sQuery(id+"F0.wireOp",EDGE,"E281"),sQuery(id+"F0.wireOp",EDGE,"E282"),sQuery(id+"F0.wireOp",EDGE,"E283"),sQuery(id+"F0.wireOp",EDGE,"E284"),sQuery(id+"F0.wireOp",EDGE,"E285"),sQuery(id+"F0.wireOp",EDGE,"E286"),sQuery(id+"F0.wireOp",EDGE,"E287"),sQuery(id+"F0.wireOp",EDGE,"E288"),sQuery(id+"F0.wireOp",EDGE,"E289"),sQuery(id+"F0.wireOp",EDGE,"E290"),sQuery(id+"F0.wireOp",EDGE,"E291"),sQuery(id+"F0.wireOp",EDGE,"E292"),sQuery(id+"F0.wireOp",EDGE,"E293"),sQuery(id+"F0.wireOp",EDGE,"E294"),sQuery(id+"F0.wireOp",EDGE,"E295"),sQuery(id+"F0.wireOp",EDGE,"E296"),sQuery(id+"F0.wireOp",EDGE,"E297"),sQuery(id+"F0.wireOp",EDGE,"E298"),sQuery(id+"F0.wireOp",EDGE,"E299"),sQuery(id+"F0.wireOp",EDGE,"E300"),sQuery(id+"F0.wireOp",EDGE,"E301"),sQuery(id+"F0.wireOp",EDGE,"E302"),sQuery(id+"F0.wireOp",EDGE,"E303"),sQuery(id+"F0.wireOp",EDGE,"E304"),sQuery(id+"F0.wireOp",EDGE,"E305"),sQuery(id+"F0.wireOp",EDGE,"E306"),sQuery(id+"F0.wireOp",EDGE,"E307"),sQuery(id+"F0.wireOp",EDGE,"E308"),sQuery(id+"F0.wireOp",EDGE,"E309"),sQuery(id+"F0.wireOp",EDGE,"E310"),sQuery(id+"F0.wireOp",EDGE,"E311"),sQuery(id+"F0.wireOp",EDGE,"E312"),sQuery(id+"F0.wireOp",EDGE,"E313"),sQuery(id+"F0.wireOp",EDGE,"E314"),sQuery(id+"F0.wireOp",EDGE,"E315"),sQuery(id+"F0.wireOp",EDGE,"E316"),sQuery(id+"F0.wireOp",EDGE,"E317"),sQuery(id+"F0.wireOp",EDGE,"E318"),sQuery(id+"F0.wireOp",EDGE,"E319"),sQuery(id+"F0.wireOp",EDGE,"E320"),sQuery(id+"F0.wireOp",EDGE,"E321"),sQuery(id+"F0.wireOp",EDGE,"E322"),sQuery(id+"F0.wireOp",EDGE,"E323"),sQuery(id+"F0.wireOp",EDGE,"E324"),sQuery(id+"F0.wireOp",EDGE,"E325"),sQuery(id+"F0.wireOp",EDGE,"E326"),sQuery(id+"F0.wireOp",EDGE,"E327"),sQuery(id+"F0.wireOp",EDGE,"E328"),sQuery(id+"F0.wireOp",EDGE,"E329"),sQuery(id+"F0.wireOp",EDGE,"E330"),sQuery(id+"F0.wireOp",EDGE,"E331"),sQuery(id+"F0.wireOp",EDGE,"E332"),sQuery(id+"F0.wireOp",EDGE,"E333"),sQuery(id+"F0.wireOp",EDGE,"E334"),sQuery(id+"F0.wireOp",EDGE,"E335"),sQuery(id+"F0.wireOp",EDGE,"E336"),sQuery(id+"F0.wireOp",EDGE,"E337"),sQuery(id+"F0.wireOp",EDGE,"E338"),sQuery(id+"F0.wireOp",EDGE,"E339"),sQuery(id+"F0.wireOp",EDGE,"E340"),sQuery(id+"F0.wireOp",EDGE,"E341"),sQuery(id+"F0.wireOp",EDGE,"E342"),sQuery(id+"F0.wireOp",EDGE,"E343"),sQuery(id+"F0.wireOp",EDGE,"E344"),sQuery(id+"F0.wireOp",EDGE,"E345"),sQuery(id+"F0.wireOp",EDGE,"E346"),sQuery(id+"F0.wireOp",EDGE,"E347"),sQuery(id+"F0.wireOp",EDGE,"E348"),sQuery(id+"F0.wireOp",EDGE,"E349"),sQuery(id+"F0.wireOp",EDGE,"E350"),sQuery(id+"F0.wireOp",EDGE,"E351"),sQuery(id+"F0.wireOp",EDGE,"E352"),sQuery(id+"F0.wireOp",EDGE,"E353"),sQuery(id+"F0.wireOp",EDGE,"E354"),sQuery(id+"F0.wireOp",EDGE,"E355"),sQuery(id+"F0.wireOp",EDGE,"E356"),sQuery(id+"F0.wireOp",EDGE,"E357"),sQuery(id+"F0.wireOp",EDGE,"E358"),sQuery(id+"F0.wireOp",EDGE,"E359"),sQuery(id+"F0.wireOp",EDGE,"E360"),sQuery(id+"F0.wireOp",EDGE,"E361"),sQuery(id+"F0.wireOp",EDGE,"E362"),sQuery(id+"F0.wireOp",EDGE,"E363"),sQuery(id+"F0.wireOp",EDGE,"E364"),sQuery(id+"F0.wireOp",EDGE,"E365"),sQuery(id+"F0.wireOp",EDGE,"E365"),sQuery(id+"F0.wireOp",EDGE,"E366"),sQuery(id+"F0.wireOp",EDGE,"E367"),sQuery(id+"F0.wireOp",EDGE,"E368"),sQuery(id+"F0.wireOp",EDGE,"E369"),sQuery(id+"F0.wireOp",EDGE,"E370"),sQuery(id+"F0.wireOp",EDGE,"E371"),sQuery(id+"F0.wireOp",EDGE,"E372"),sQuery(id+"F0.wireOp",EDGE,"E373"),sQuery(id+"F0.wireOp",EDGE,"E374"),sQuery(id+"F0.wireOp",EDGE,"E375"),sQuery(id+"F0.wireOp",EDGE,"E376"),sQuery(id+"F0.wireOp",EDGE,"E377"),sQuery(id+"F0.wireOp",EDGE,"E378"),sQuery(id+"F0.wireOp",EDGE,"E379"),sQuery(id+"F0.wireOp",EDGE,"E380"),sQuery(id+"F0.wireOp",EDGE,"E381"),sQuery(id+"F0.wireOp",EDGE,"E382"),sQuery(id+"F0.wireOp",EDGE,"E383"),sQuery(id+"F0.wireOp",EDGE,"E384"),sQuery(id+"F0.wireOp",EDGE,"E385"),sQuery(id+"F0.wireOp",EDGE,"E386"),sQuery(id+"F0.wireOp",EDGE,"E387"),sQuery(id+"F0.wireOp",EDGE,"E388"),sQuery(id+"F0.wireOp",EDGE,"E389"),sQuery(id+"F0.wireOp",EDGE,"E390"),sQuery(id+"F0.wireOp",EDGE,"E391"),sQuery(id+"F0.wireOp",EDGE,"E392"),sQuery(id+"F0.wireOp",EDGE,"E393"),sQuery(id+"F0.wireOp",EDGE,"E394"),sQuery(id+"F0.wireOp",EDGE,"E395"),sQuery(id+"F0.wireOp",EDGE,"E396"),sQuery(id+"F0.wireOp",EDGE,"E397"),sQuery(id+"F0.wireOp",EDGE,"E398"),sQuery(id+"F0.wireOp",EDGE,"E399"),sQuery(id+"F0.wireOp",EDGE,"E400"),sQuery(id+"F0.wireOp",EDGE,"E401"),sQuery(id+"F0.wireOp",EDGE,"E402"),sQuery(id+"F0.wireOp",EDGE,"E403"),sQuery(id+"F0.wireOp",EDGE,"E404"),sQuery(id+"F0.wireOp",EDGE,"E405"),sQuery(id+"F0.wireOp",EDGE,"E406"),sQuery(id+"F0.wireOp",EDGE,"E407"),sQuery(id+"F0.wireOp",EDGE,"E408"),sQuery(id+"F0.wireOp",EDGE,"E409"),sQuery(id+"F0.wireOp",EDGE,"E410"),sQuery(id+"F0.wireOp",EDGE,"E411"),sQuery(id+"F0.wireOp",EDGE,"E412"),sQuery(id+"F0.wireOp",EDGE,"E413"),sQuery(id+"F0.wireOp",EDGE,"E414"),sQuery(id+"F0.wireOp",EDGE,"E415"),sQuery(id+"F0.wireOp",EDGE,"E416"),sQuery(id+"F0.wireOp",EDGE,"E417"),sQuery(id+"F0.wireOp",EDGE,"E418"),sQuery(id+"F0.wireOp",EDGE,"E419"),sQuery(id+"F0.wireOp",EDGE,"E420"),sQuery(id+"F0.wireOp",EDGE,"E421"),sQuery(id+"F0.wireOp",EDGE,"E422"),sQuery(id+"F0.wireOp",EDGE,"E423"),sQuery(id+"F0.wireOp",EDGE,"E424"),sQuery(id+"F0.wireOp",EDGE,"E425"),sQuery(id+"F0.wireOp",EDGE,"E426"),sQuery(id+"F0.wireOp",EDGE,"E427"),sQuery(id+"F0.wireOp",EDGE,"E428"),sQuery(id+"F0.wireOp",EDGE,"E429"),sQuery(id+"F0.wireOp",EDGE,"E430"),sQuery(id+"F0.wireOp",EDGE,"E431"),sQuery(id+"F0.wireOp",EDGE,"E432"),sQuery(id+"F0.wireOp",EDGE,"E433"),sQuery(id+"F0.wireOp",EDGE,"E434"),sQuery(id+"F0.wireOp",EDGE,"E435"),sQuery(id+"F0.wireOp",EDGE,"E436"),sQuery(id+"F0.wireOp",EDGE,"E437"),sQuery(id+"F0.wireOp",EDGE,"E438"),sQuery(id+"F0.wireOp",EDGE,"E439"),sQuery(id+"F0.wireOp",EDGE,"E440"),sQuery(id+"F0.wireOp",EDGE,"E441"),sQuery(id+"F0.wireOp",EDGE,"E442"),sQuery(id+"F0.wireOp",EDGE,"E443"),sQuery(id+"F0.wireOp",EDGE,"E444"),sQuery(id+"F0.wireOp",EDGE,"E445"),sQuery(id+"F0.wireOp",EDGE,"E446"),sQuery(id+"F0.wireOp",EDGE,"E447"),sQuery(id+"F0.wireOp",EDGE,"E448"),sQuery(id+"F0.wireOp",EDGE,"E449"),sQuery(id+"F0.wireOp",EDGE,"E450"),sQuery(id+"F0.wireOp",EDGE,"E451"),sQuery(id+"F0.wireOp",EDGE,"E452"),sQuery(id+"F0.wireOp",EDGE,"E453"),sQuery(id+"F0.wireOp",EDGE,"E454"),sQuery(id+"F0.wireOp",EDGE,"E455"),sQuery(id+"F0.wireOp",EDGE,"E456"),sQuery(id+"F0.wireOp",EDGE,"E457"),sQuery(id+"F0.wireOp",EDGE,"E458"),sQuery(id+"F0.wireOp",EDGE,"E459"),sQuery(id+"F0.wireOp",EDGE,"E460"),sQuery(id+"F0.wireOp",EDGE,"E461"),sQuery(id+"F0.wireOp",EDGE,"E462"),sQuery(id+"F0.wireOp",EDGE,"E463"),sQuery(id+"F0.wireOp",EDGE,"E464"),sQuery(id+"F0.wireOp",EDGE,"E465"),sQuery(id+"F0.wireOp",EDGE,"E466"),sQuery(id+"F0.wireOp",EDGE,"E467"),sQuery(id+"F0.wireOp",EDGE,"E468"),sQuery(id+"F0.wireOp",EDGE,"E469"),sQuery(id+"F0.wireOp",EDGE,"E470"),sQuery(id+"F0.wireOp",EDGE,"E471"),sQuery(id+"F0.wireOp",EDGE,"E472"),sQuery(id+"F0.wireOp",EDGE,"E473"),sQuery(id+"F0.wireOp",EDGE,"E474"),sQuery(id+"F0.wireOp",EDGE,"E475"),sQuery(id+"F0.wireOp",EDGE,"E476"),sQuery(id+"F0.wireOp",EDGE,"E477"),sQuery(id+"F0.wireOp",EDGE,"E478"),sQuery(id+"F0.wireOp",EDGE,"E479"),sQuery(id+"F0.wireOp",EDGE,"E480"),sQuery(id+"F0.wireOp",EDGE,"E481"),sQuery(id+"F0.wireOp",EDGE,"E482"),sQuery(id+"F0.wireOp",EDGE,"E483"),sQuery(id+"F0.wireOp",EDGE,"E484"),sQuery(id+"F0.wireOp",EDGE,"E485"),sQuery(id+"F0.wireOp",EDGE,"E486"),sQuery(id+"F0.wireOp",EDGE,"E487"),sQuery(id+"F0.wireOp",EDGE,"E488"),sQuery(id+"F0.wireOp",EDGE,"E489"),sQuery(id+"F0.wireOp",EDGE,"E490"),sQuery(id+"F0.wireOp",EDGE,"E491"),sQuery(id+"F0.wireOp",EDGE,"E492"),sQuery(id+"F0.wireOp",EDGE,"E493"),sQuery(id+"F0.wireOp",EDGE,"E494"),sQuery(id+"F0.wireOp",EDGE,"E495"),sQuery(id+"F0.wireOp",EDGE,"E496"),sQuery(id+"F0.wireOp",EDGE,"E497"),sQuery(id+"F0.wireOp",EDGE,"E498"),sQuery(id+"F0.wireOp",EDGE,"E499"),sQuery(id+"F0.wireOp",EDGE,"E500"),sQuery(id+"F0.wireOp",EDGE,"E501"),sQuery(id+"F0.wireOp",EDGE,"E502"),sQuery(id+"F0.wireOp",EDGE,"E503"),sQuery(id+"F0.wireOp",EDGE,"E504"),sQuery(id+"F0.wireOp",EDGE,"E505"),sQuery(id+"F0.wireOp",EDGE,"E506"),sQuery(id+"F0.wireOp",EDGE,"E507"),sQuery(id+"F0.wireOp",EDGE,"E508"),sQuery(id+"F0.wireOp",EDGE,"E509"),sQuery(id+"F0.wireOp",EDGE,"E510"),sQuery(id+"F0.wireOp",EDGE,"E511"),sQuery(id+"F0.wireOp",EDGE,"E512"),sQuery(id+"F0.wireOp",EDGE,"E513"),sQuery(id+"F0.wireOp",EDGE,"E514"),sQuery(id+"F0.wireOp",EDGE,"E515"),sQuery(id+"F0.wireOp",EDGE,"E516"),sQuery(id+"F0.wireOp",EDGE,"E517"),sQuery(id+"F0.wireOp",EDGE,"E518"),sQuery(id+"F0.wireOp",EDGE,"E519"),sQuery(id+"F0.wireOp",EDGE,"E520"),sQuery(id+"F0.wireOp",EDGE,"E521"),sQuery(id+"F0.wireOp",EDGE,"E522"),sQuery(id+"F0.wireOp",EDGE,"E523"),sQuery(id+"F0.wireOp",EDGE,"E524"),sQuery(id+"F0.wireOp",EDGE,"E525"),sQuery(id+"F0.wireOp",EDGE,"E526"),sQuery(id+"F0.wireOp",EDGE,"E527"),sQuery(id+"F0.wireOp",EDGE,"E528"),sQuery(id+"F0.wireOp",EDGE,"E529"),sQuery(id+"F0.wireOp",EDGE,"E530"),sQuery(id+"F0.wireOp",EDGE,"E531"),sQuery(id+"F0.wireOp",EDGE,"E532"),sQuery(id+"F0.wireOp",EDGE,"E533"),sQuery(id+"F0.wireOp",EDGE,"E534"),sQuery(id+"F0.wireOp",EDGE,"E535"),sQuery(id+"F0.wireOp",EDGE,"E536"),sQuery(id+"F0.wireOp",EDGE,"E537"),sQuery(id+"F0.wireOp",EDGE,"E538"),sQuery(id+"F0.wireOp",EDGE,"E539"),sQuery(id+"F0.wireOp",EDGE,"E540"),sQuery(id+"F0.wireOp",EDGE,"E541"),sQuery(id+"F0.wireOp",EDGE,"E542"),sQuery(id+"F0.wireOp",EDGE,"E543"),sQuery(id+"F0.wireOp",EDGE,"E544"),sQuery(id+"F0.wireOp",EDGE,"E545"),sQuery(id+"F0.wireOp",EDGE,"E546"),sQuery(id+"F0.wireOp",EDGE,"E547"),sQuery(id+"F0.wireOp",EDGE,"E548"),sQuery(id+"F0.wireOp",EDGE,"E549"),sQuery(id+"F0.wireOp",EDGE,"E550"),sQuery(id+"F0.wireOp",EDGE,"E551"),sQuery(id+"F0.wireOp",EDGE,"E552"),sQuery(id+"F0.wireOp",EDGE,"E553"),sQuery(id+"F0.wireOp",EDGE,"E554"),sQuery(id+"F0.wireOp",EDGE,"E555"),sQuery(id+"F0.wireOp",EDGE,"E556"),sQuery(id+"F0.wireOp",EDGE,"E557"),sQuery(id+"F0.wireOp",EDGE,"E558"),sQuery(id+"F0.wireOp",EDGE,"E559"),sQuery(id+"F0.wireOp",EDGE,"E560"),sQuery(id+"F0.wireOp",EDGE,"E561"),sQuery(id+"F0.wireOp",EDGE,"E562"),sQuery(id+"F0.wireOp",EDGE,"E563"),sQuery(id+"F0.wireOp",EDGE,"E564"),sQuery(id+"F0.wireOp",EDGE,"E565"),sQuery(id+"F0.wireOp",EDGE,"E566"),sQuery(id+"F0.wireOp",EDGE,"E567"),sQuery(id+"F0.wireOp",EDGE,"E568"),sQuery(id+"F0.wireOp",EDGE,"E569"),sQuery(id+"F0.wireOp",EDGE,"E570"),sQuery(id+"F0.wireOp",EDGE,"E571"),sQuery(id+"F0.wireOp",EDGE,"E572"),sQuery(id+"F0.wireOp",EDGE,"E573"),sQuery(id+"F0.wireOp",EDGE,"E574"),sQuery(id+"F0.wireOp",EDGE,"E575"),sQuery(id+"F0.wireOp",EDGE,"E576"),sQuery(id+"F0.wireOp",EDGE,"E577"),sQuery(id+"F0.wireOp",EDGE,"E578"),sQuery(id+"F0.wireOp",EDGE,"E579"),sQuery(id+"F0.wireOp",EDGE,"E580"),sQuery(id+"F0.wireOp",EDGE,"E581"),sQuery(id+"F0.wireOp",EDGE,"E582"),sQuery(id+"F0.wireOp",EDGE,"E583"),sQuery(id+"F0.wireOp",EDGE,"E584"),sQuery(id+"F0.wireOp",EDGE,"E585"),sQuery(id+"F0.wireOp",EDGE,"E586"),sQuery(id+"F0.wireOp",EDGE,"E587"),sQuery(id+"F0.wireOp",EDGE,"E588"),sQuery(id+"F0.wireOp",EDGE,"E589"),sQuery(id+"F0.wireOp",EDGE,"E590"),sQuery(id+"F0.wireOp",EDGE,"E591"),sQuery(id+"F0.wireOp",EDGE,"E592"),sQuery(id+"F0.wireOp",EDGE,"E593"),sQuery(id+"F0.wireOp",EDGE,"E594"),sQuery(id+"F0.wireOp",EDGE,"E595"),sQuery(id+"F0.wireOp",EDGE,"E596"),sQuery(id+"F0.wireOp",EDGE,"E597"),sQuery(id+"F0.wireOp",EDGE,"E598"),sQuery(id+"F0.wireOp",EDGE,"E599"),sQuery(id+"F0.wireOp",EDGE,"E600"),sQuery(id+"F0.wireOp",EDGE,"E601"),sQuery(id+"F0.wireOp",EDGE,"E602"),sQuery(id+"F0.wireOp",EDGE,"E603"),sQuery(id+"F0.wireOp",EDGE,"E604"),sQuery(id+"F0.wireOp",EDGE,"E605"),sQuery(id+"F0.wireOp",EDGE,"E606"),sQuery(id+"F0.wireOp",EDGE,"E607"),sQuery(id+"F0.wireOp",EDGE,"E608"),sQuery(id+"F0.wireOp",EDGE,"E609"),sQuery(id+"F0.wireOp",EDGE,"E610"),sQuery(id+"F0.wireOp",EDGE,"E611"),sQuery(id+"F0.wireOp",EDGE,"E612"),sQuery(id+"F0.wireOp",EDGE,"E613"),sQuery(id+"F0.wireOp",EDGE,"E614"),sQuery(id+"F0.wireOp",EDGE,"E615"),sQuery(id+"F0.wireOp",EDGE,"E616"),sQuery(id+"F0.wireOp",EDGE,"E617"),sQuery(id+"F0.wireOp",EDGE,"E618"),sQuery(id+"F0.wireOp",EDGE,"E619"),sQuery(id+"F0.wireOp",EDGE,"E620"),sQuery(id+"F0.wireOp",EDGE,"E621"),sQuery(id+"F0.wireOp",EDGE,"E622"),sQuery(id+"F0.wireOp",EDGE,"E623"),sQuery(id+"F0.wireOp",EDGE,"E624"),sQuery(id+"F0.wireOp",EDGE,"E625"),sQuery(id+"F0.wireOp",EDGE,"E626"),sQuery(id+"F0.wireOp",EDGE,"E627"),sQuery(id+"F0.wireOp",EDGE,"E628"),sQuery(id+"F0.wireOp",EDGE,"E629"),sQuery(id+"F0.wireOp",EDGE,"E630"),sQuery(id+"F0.wireOp",EDGE,"E631"),sQuery(id+"F0.wireOp",EDGE,"E632"),sQuery(id+"F0.wireOp",EDGE,"E633"),sQuery(id+"F0.wireOp",EDGE,"E634"),sQuery(id+"F0.wireOp",EDGE,"E635"),sQuery(id+"F0.wireOp",EDGE,"E636"),sQuery(id+"F0.wireOp",EDGE,"E637"),sQuery(id+"F0.wireOp",EDGE,"E638"),sQuery(id+"F0.wireOp",EDGE,"E639"),sQuery(id+"F0.wireOp",EDGE,"E640"),sQuery(id+"F0.wireOp",EDGE,"E641"),sQuery(id+"F0.wireOp",EDGE,"E642"),sQuery(id+"F0.wireOp",EDGE,"E643"),sQuery(id+"F0.wireOp",EDGE,"E644"),sQuery(id+"F0.wireOp",EDGE,"E645"),sQuery(id+"F0.wireOp",EDGE,"E646"),sQuery(id+"F0.wireOp",EDGE,"E647"),sQuery(id+"F0.wireOp",EDGE,"E648"),sQuery(id+"F0.wireOp",EDGE,"E649"),sQuery(id+"F0.wireOp",EDGE,"E650"),sQuery(id+"F0.wireOp",EDGE,"E651"),sQuery(id+"F0.wireOp",EDGE,"E652"),sQuery(id+"F0.wireOp",EDGE,"E653"),sQuery(id+"F0.wireOp",EDGE,"E654"),sQuery(id+"F0.wireOp",EDGE,"E655"),sQuery(id+"F0.wireOp",EDGE,"E656"),sQuery(id+"F0.wireOp",EDGE,"E657"),sQuery(id+"F0.wireOp",EDGE,"E658"),sQuery(id+"F0.wireOp",EDGE,"E659"),sQuery(id+"F0.wireOp",EDGE,"E660"),sQuery(id+"F0.wireOp",EDGE,"E660"),sQuery(id+"F0.wireOp",EDGE,"E661"),sQuery(id+"F0.wireOp",EDGE,"E662"),sQuery(id+"F0.wireOp",EDGE,"E663"),sQuery(id+"F0.wireOp",EDGE,"E664"),sQuery(id+"F0.wireOp",EDGE,"E665"),sQuery(id+"F0.wireOp",EDGE,"E666"),sQuery(id+"F0.wireOp",EDGE,"E667"),sQuery(id+"F0.wireOp",EDGE,"E668"),sQuery(id+"F0.wireOp",EDGE,"E669"),sQuery(id+"F0.wireOp",EDGE,"E670"),sQuery(id+"F0.wireOp",EDGE,"E671"),sQuery(id+"F0.wireOp",EDGE,"E672"),sQuery(id+"F0.wireOp",EDGE,"E673"),sQuery(id+"F0.wireOp",EDGE,"E674"),sQuery(id+"F0.wireOp",EDGE,"E675"),sQuery(id+"F0.wireOp",EDGE,"E676"),sQuery(id+"F0.wireOp",EDGE,"E677"),sQuery(id+"F0.wireOp",EDGE,"E678"),sQuery(id+"F0.wireOp",EDGE,"E679"),sQuery(id+"F0.wireOp",EDGE,"E680"),sQuery(id+"F0.wireOp",EDGE,"E681"),sQuery(id+"F0.wireOp",EDGE,"E682"),sQuery(id+"F0.wireOp",EDGE,"E683"),sQuery(id+"F0.wireOp",EDGE,"E684"),sQuery(id+"F0.wireOp",EDGE,"E685"),sQuery(id+"F0.wireOp",EDGE,"E686"),sQuery(id+"F0.wireOp",EDGE,"E687"),sQuery(id+"F0.wireOp",EDGE,"E688"),sQuery(id+"F0.wireOp",EDGE,"E689"),sQuery(id+"F0.wireOp",EDGE,"E690"),sQuery(id+"F0.wireOp",EDGE,"E691"),sQuery(id+"F0.wireOp",EDGE,"E692"),sQuery(id+"F0.wireOp",EDGE,"E693"),sQuery(id+"F0.wireOp",EDGE,"E694"),sQuery(id+"F0.wireOp",EDGE,"E695"),sQuery(id+"F0.wireOp",EDGE,"E696"),sQuery(id+"F0.wireOp",EDGE,"E697"),sQuery(id+"F0.wireOp",EDGE,"E698"),sQuery(id+"F0.wireOp",EDGE,"E699"),sQuery(id+"F0.wireOp",EDGE,"E700"),sQuery(id+"F0.wireOp",EDGE,"E701"),sQuery(id+"F0.wireOp",EDGE,"E702"),sQuery(id+"F0.wireOp",EDGE,"E703"),sQuery(id+"F0.wireOp",EDGE,"E704"),sQuery(id+"F0.wireOp",EDGE,"E705"),sQuery(id+"F0.wireOp",EDGE,"E706"),sQuery(id+"F0.wireOp",EDGE,"E707"),sQuery(id+"F0.wireOp",EDGE,"E708"),sQuery(id+"F0.wireOp",EDGE,"E709"),sQuery(id+"F0.wireOp",EDGE,"E710"),sQuery(id+"F0.wireOp",EDGE,"E711"),sQuery(id+"F0.wireOp",EDGE,"E712"),sQuery(id+"F0.wireOp",EDGE,"E713"),sQuery(id+"F0.wireOp",EDGE,"E714"),sQuery(id+"F0.wireOp",EDGE,"E715"),sQuery(id+"F0.wireOp",EDGE,"E716"),sQuery(id+"F0.wireOp",EDGE,"E717"),sQuery(id+"F0.wireOp",EDGE,"E718"),sQuery(id+"F0.wireOp",EDGE,"E719"),sQuery(id+"F0.wireOp",EDGE,"E720"),sQuery(id+"F0.wireOp",EDGE,"E721"),sQuery(id+"F0.wireOp",EDGE,"E722"),sQuery(id+"F0.wireOp",EDGE,"E723"),sQuery(id+"F0.wireOp",EDGE,"E724"),sQuery(id+"F0.wireOp",EDGE,"E725"),sQuery(id+"F0.wireOp",EDGE,"E726"),sQuery(id+"F0.wireOp",EDGE,"E727"),sQuery(id+"F0.wireOp",EDGE,"E728"),sQuery(id+"F0.wireOp",EDGE,"E729"),sQuery(id+"F0.wireOp",EDGE,"E730"),sQuery(id+"F0.wireOp",EDGE,"E731"),sQuery(id+"F0.wireOp",EDGE,"E732"),sQuery(id+"F0.wireOp",EDGE,"E733"),sQuery(id+"F0.wireOp",EDGE,"E734"),sQuery(id+"F0.wireOp",EDGE,"E735"),sQuery(id+"F0.wireOp",EDGE,"E736"),sQuery(id+"F0.wireOp",EDGE,"E737"),sQuery(id+"F0.wireOp",EDGE,"E738"),sQuery(id+"F0.wireOp",EDGE,"E739"),sQuery(id+"F0.wireOp",EDGE,"E740"),sQuery(id+"F0.wireOp",EDGE,"E741"),sQuery(id+"F0.wireOp",EDGE,"E742"),sQuery(id+"F0.wireOp",EDGE,"E743"),sQuery(id+"F0.wireOp",EDGE,"E744"),sQuery(id+"F0.wireOp",EDGE,"E745"),sQuery(id+"F0.wireOp",EDGE,"E746"),sQuery(id+"F0.wireOp",EDGE,"E747"),sQuery(id+"F0.wireOp",EDGE,"E748"),sQuery(id+"F0.wireOp",EDGE,"E749"),sQuery(id+"F0.wireOp",EDGE,"E750"),sQuery(id+"F0.wireOp",EDGE,"E751"),sQuery(id+"F0.wireOp",EDGE,"E752"),sQuery(id+"F0.wireOp",EDGE,"E753"),sQuery(id+"F0.wireOp",EDGE,"E754"),sQuery(id+"F0.wireOp",EDGE,"E755"),sQuery(id+"F0.wireOp",EDGE,"E756"),sQuery(id+"F0.wireOp",EDGE,"E757"),sQuery(id+"F0.wireOp",EDGE,"E758"),sQuery(id+"F0.wireOp",EDGE,"E759"),sQuery(id+"F0.wireOp",EDGE,"E760"),sQuery(id+"F0.wireOp",EDGE,"E761"),sQuery(id+"F0.wireOp",EDGE,"E762"),sQuery(id+"F0.wireOp",EDGE,"E763"),sQuery(id+"F0.wireOp",EDGE,"E764"),sQuery(id+"F0.wireOp",EDGE,"E765"),sQuery(id+"F0.wireOp",EDGE,"E766"),sQuery(id+"F0.wireOp",EDGE,"E767"),sQuery(id+"F0.wireOp",EDGE,"E768"),sQuery(id+"F0.wireOp",EDGE,"E769"),sQuery(id+"F0.wireOp",EDGE,"E770"),sQuery(id+"F0.wireOp",EDGE,"E771"),sQuery(id+"F0.wireOp",EDGE,"E772"),sQuery(id+"F0.wireOp",EDGE,"E773"),sQuery(id+"F0.wireOp",EDGE,"E774"),sQuery(id+"F0.wireOp",EDGE,"E775"),sQuery(id+"F0.wireOp",EDGE,"E776"),sQuery(id+"F0.wireOp",EDGE,"E777"),sQuery(id+"F0.wireOp",EDGE,"E778"),sQuery(id+"F0.wireOp",EDGE,"E779"),sQuery(id+"F0.wireOp",EDGE,"E780"),sQuery(id+"F0.wireOp",EDGE,"E781"),sQuery(id+"F0.wireOp",EDGE,"E782"),sQuery(id+"F0.wireOp",EDGE,"E783"),sQuery(id+"F0.wireOp",EDGE,"E784"),sQuery(id+"F0.wireOp",EDGE,"E785"),sQuery(id+"F0.wireOp",EDGE,"E786"),sQuery(id+"F0.wireOp",EDGE,"E787"),sQuery(id+"F0.wireOp",EDGE,"E788"),sQuery(id+"F0.wireOp",EDGE,"E789"),sQuery(id+"F0.wireOp",EDGE,"E790"),sQuery(id+"F0.wireOp",EDGE,"E791"),sQuery(id+"F0.wireOp",EDGE,"E792"),sQuery(id+"F0.wireOp",EDGE,"E793"),sQuery(id+"F0.wireOp",EDGE,"E794"),sQuery(id+"F0.wireOp",EDGE,"E795"),sQuery(id+"F0.wireOp",EDGE,"E796"),sQuery(id+"F0.wireOp",EDGE,"E797"),sQuery(id+"F0.wireOp",EDGE,"E798"),sQuery(id+"F0.wireOp",EDGE,"E799"),sQuery(id+"F0.wireOp",EDGE,"E800"),sQuery(id+"F0.wireOp",EDGE,"E801"),sQuery(id+"F0.wireOp",EDGE,"E802"),sQuery(id+"F0.wireOp",EDGE,"E803"),sQuery(id+"F0.wireOp",EDGE,"E804"),sQuery(id+"F0.wireOp",EDGE,"E805"),sQuery(id+"F0.wireOp",EDGE,"E806"),sQuery(id+"F0.wireOp",EDGE,"E807"),sQuery(id+"F0.wireOp",EDGE,"E808"),sQuery(id+"F0.wireOp",EDGE,"E809"),sQuery(id+"F0.wireOp",EDGE,"E810"),sQuery(id+"F0.wireOp",EDGE,"E811"),sQuery(id+"F0.wireOp",EDGE,"E812"),sQuery(id+"F0.wireOp",EDGE,"E813"),sQuery(id+"F0.wireOp",EDGE,"E814"),sQuery(id+"F0.wireOp",EDGE,"E815"),sQuery(id+"F0.wireOp",EDGE,"E816"),sQuery(id+"F0.wireOp",EDGE,"E817"),sQuery(id+"F0.wireOp",EDGE,"E818"),sQuery(id+"F0.wireOp",EDGE,"E819"),sQuery(id+"F0.wireOp",EDGE,"E820"),sQuery(id+"F0.wireOp",EDGE,"E821"),sQuery(id+"F0.wireOp",EDGE,"E822"),sQuery(id+"F0.wireOp",EDGE,"E823"),sQuery(id+"F0.wireOp",EDGE,"E824"),sQuery(id+"F0.wireOp",EDGE,"E825"),sQuery(id+"F0.wireOp",EDGE,"E826"),sQuery(id+"F0.wireOp",EDGE,"E827"),sQuery(id+"F0.wireOp",EDGE,"E828"),sQuery(id+"F0.wireOp",EDGE,"E829"),sQuery(id+"F0.wireOp",EDGE,"E830"),sQuery(id+"F0.wireOp",EDGE,"E831"),sQuery(id+"F0.wireOp",EDGE,"E832"),sQuery(id+"F0.wireOp",EDGE,"E833"),sQuery(id+"F0.wireOp",EDGE,"E834"),sQuery(id+"F0.wireOp",EDGE,"E835"),sQuery(id+"F0.wireOp",EDGE,"E836"),sQuery(id+"F0.wireOp",EDGE,"E837"),sQuery(id+"F0.wireOp",EDGE,"E838"),sQuery(id+"F0.wireOp",EDGE,"E839"),sQuery(id+"F0.wireOp",EDGE,"E840"),sQuery(id+"F0.wireOp",EDGE,"E841"),sQuery(id+"F0.wireOp",EDGE,"E842"),sQuery(id+"F0.wireOp",EDGE,"E843"),sQuery(id+"F0.wireOp",EDGE,"E844"),sQuery(id+"F0.wireOp",EDGE,"E845"),sQuery(id+"F0.wireOp",EDGE,"E846"),sQuery(id+"F0.wireOp",EDGE,"E847"),sQuery(id+"F0.wireOp",EDGE,"E848"),sQuery(id+"F0.wireOp",EDGE,"E849"),sQuery(id+"F0.wireOp",EDGE,"E850"),sQuery(id+"F0.wireOp",EDGE,"E851"),sQuery(id+"F0.wireOp",EDGE,"E852"),sQuery(id+"F0.wireOp",EDGE,"E853"),sQuery(id+"F0.wireOp",EDGE,"E854"),sQuery(id+"F0.wireOp",EDGE,"E855"),sQuery(id+"F0.wireOp",EDGE,"E856"),sQuery(id+"F0.wireOp",EDGE,"E857"),sQuery(id+"F0.wireOp",EDGE,"E858"),sQuery(id+"F0.wireOp",EDGE,"E859"),sQuery(id+"F0.wireOp",EDGE,"E860"),sQuery(id+"F0.wireOp",EDGE,"E861"),sQuery(id+"F0.wireOp",EDGE,"E862"),sQuery(id+"F0.wireOp",EDGE,"E863"),sQuery(id+"F0.wireOp",EDGE,"E864"),sQuery(id+"F0.wireOp",EDGE,"E865"),sQuery(id+"F0.wireOp",EDGE,"E866"),sQuery(id+"F0.wireOp",EDGE,"E867"),sQuery(id+"F0.wireOp",EDGE,"E868"),sQuery(id+"F0.wireOp",EDGE,"E869"),sQuery(id+"F0.wireOp",EDGE,"E870"),sQuery(id+"F0.wireOp",EDGE,"E871"),sQuery(id+"F0.wireOp",EDGE,"E872"),sQuery(id+"F0.wireOp",EDGE,"E873"),sQuery(id+"F0.wireOp",EDGE,"E874"),sQuery(id+"F0.wireOp",EDGE,"E875"),sQuery(id+"F0.wireOp",EDGE,"E876"),sQuery(id+"F0.wireOp",EDGE,"E877"),sQuery(id+"F0.wireOp",EDGE,"E878"),sQuery(id+"F0.wireOp",EDGE,"E879"),sQuery(id+"F0.wireOp",EDGE,"E880"),sQuery(id+"F0.wireOp",EDGE,"E881"),sQuery(id+"F0.wireOp",EDGE,"E882"),sQuery(id+"F0.wireOp",EDGE,"E883"),sQuery(id+"F0.wireOp",EDGE,"E884"),sQuery(id+"F0.wireOp",EDGE,"E885"),sQuery(id+"F0.wireOp",EDGE,"E886"),sQuery(id+"F0.wireOp",EDGE,"E887"),sQuery(id+"F0.wireOp",EDGE,"E888"),sQuery(id+"F0.wireOp",EDGE,"E889"),sQuery(id+"F0.wireOp",EDGE,"E890"),sQuery(id+"F0.wireOp",EDGE,"E891"),sQuery(id+"F0.wireOp",EDGE,"E892"),sQuery(id+"F0.wireOp",EDGE,"E893"),sQuery(id+"F0.wireOp",EDGE,"E894"),sQuery(id+"F0.wireOp",EDGE,"E895"),sQuery(id+"F0.wireOp",EDGE,"E896"),sQuery(id+"F0.wireOp",EDGE,"E897"),sQuery(id+"F0.wireOp",EDGE,"E898"),sQuery(id+"F0.wireOp",EDGE,"E899"),sQuery(id+"F0.wireOp",EDGE,"E900"),sQuery(id+"F0.wireOp",EDGE,"E901"),sQuery(id+"F0.wireOp",EDGE,"E902"),sQuery(id+"F0.wireOp",EDGE,"E903"),sQuery(id+"F0.wireOp",EDGE,"E904"),sQuery(id+"F0.wireOp",EDGE,"E905"),sQuery(id+"F0.wireOp",EDGE,"E906"),sQuery(id+"F0.wireOp",EDGE,"E907"),sQuery(id+"F0.wireOp",EDGE,"E908"),sQuery(id+"F0.wireOp",EDGE,"E909"),sQuery(id+"F0.wireOp",EDGE,"E910"),sQuery(id+"F0.wireOp",EDGE,"E911"),sQuery(id+"F0.wireOp",EDGE,"E912"),sQuery(id+"F0.wireOp",EDGE,"E913"),sQuery(id+"F0.wireOp",EDGE,"E914"),sQuery(id+"F0.wireOp",EDGE,"E915"),sQuery(id+"F0.wireOp",EDGE,"E916"),sQuery(id+"F0.wireOp",EDGE,"E917"),sQuery(id+"F0.wireOp",EDGE,"E918"),sQuery(id+"F0.wireOp",EDGE,"E919"),sQuery(id+"F0.wireOp",EDGE,"E920"),sQuery(id+"F0.wireOp",EDGE,"E921"),sQuery(id+"F0.wireOp",EDGE,"E922"),sQuery(id+"F0.wireOp",EDGE,"E923"),sQuery(id+"F0.wireOp",EDGE,"E924"),sQuery(id+"F0.wireOp",EDGE,"E925"),sQuery(id+"F0.wireOp",EDGE,"E926"),sQuery(id+"F0.wireOp",EDGE,"E927"),sQuery(id+"F0.wireOp",EDGE,"E928"),sQuery(id+"F0.wireOp",EDGE,"E929"),sQuery(id+"F0.wireOp",EDGE,"E930"),sQuery(id+"F0.wireOp",EDGE,"E931"),sQuery(id+"F0.wireOp",EDGE,"E932"),sQuery(id+"F0.wireOp",EDGE,"E933"),sQuery(id+"F0.wireOp",EDGE,"E934"),sQuery(id+"F0.wireOp",EDGE,"E935"),sQuery(id+"F0.wireOp",EDGE,"E936"),sQuery(id+"F0.wireOp",EDGE,"E937"),sQuery(id+"F0.wireOp",EDGE,"E938"),sQuery(id+"F0.wireOp",EDGE,"E939"),sQuery(id+"F0.wireOp",EDGE,"E940"),sQuery(id+"F0.wireOp",EDGE,"E941"),sQuery(id+"F0.wireOp",EDGE,"E942"),sQuery(id+"F0.wireOp",EDGE,"E943"),sQuery(id+"F0.wireOp",EDGE,"E944"),sQuery(id+"F0.wireOp",EDGE,"E945"),sQuery(id+"F0.wireOp",EDGE,"E946"),sQuery(id+"F0.wireOp",EDGE,"E947"),sQuery(id+"F0.wireOp",EDGE,"E948"),sQuery(id+"F0.wireOp",EDGE,"E949"),sQuery(id+"F0.wireOp",EDGE,"E950"),sQuery(id+"F0.wireOp",EDGE,"E951"),sQuery(id+"F0.wireOp",EDGE,"E952"),sQuery(id+"F0.wireOp",EDGE,"E953"),sQuery(id+"F0.wireOp",EDGE,"E954"),sQuery(id+"F0.wireOp",EDGE,"E955"),sQuery(id+"F0.wireOp",EDGE,"E955"),sQuery(id+"F0.wireOp",EDGE,"E956"),sQuery(id+"F0.wireOp",EDGE,"E957"),sQuery(id+"F0.wireOp",EDGE,"E958"),sQuery(id+"F0.wireOp",EDGE,"E959"),sQuery(id+"F0.wireOp",EDGE,"E960"),sQuery(id+"F0.wireOp",EDGE,"E961"),sQuery(id+"F0.wireOp",EDGE,"E962"),sQuery(id+"F0.wireOp",EDGE,"E963"),sQuery(id+"F0.wireOp",EDGE,"E964"),sQuery(id+"F0.wireOp",EDGE,"E965"),sQuery(id+"F0.wireOp",EDGE,"E966"),sQuery(id+"F0.wireOp",EDGE,"E967"),sQuery(id+"F0.wireOp",EDGE,"E968"),sQuery(id+"F0.wireOp",EDGE,"E969"),sQuery(id+"F0.wireOp",EDGE,"E970"),sQuery(id+"F0.wireOp",EDGE,"E971"),sQuery(id+"F0.wireOp",EDGE,"E972"),sQuery(id+"F0.wireOp",EDGE,"E973"),sQuery(id+"F0.wireOp",EDGE,"E974"),sQuery(id+"F0.wireOp",EDGE,"E975"),sQuery(id+"F0.wireOp",EDGE,"E976"),sQuery(id+"F0.wireOp",EDGE,"E977"),sQuery(id+"F0.wireOp",EDGE,"E978"),sQuery(id+"F0.wireOp",EDGE,"E979"),sQuery(id+"F0.wireOp",EDGE,"E980"),sQuery(id+"F0.wireOp",EDGE,"E981"),sQuery(id+"F0.wireOp",EDGE,"E982"),sQuery(id+"F0.wireOp",EDGE,"E983"),sQuery(id+"F0.wireOp",EDGE,"E984"),sQuery(id+"F0.wireOp",EDGE,"E985"),sQuery(id+"F0.wireOp",EDGE,"E986"),sQuery(id+"F0.wireOp",EDGE,"E987"),sQuery(id+"F0.wireOp",EDGE,"E988"),sQuery(id+"F0.wireOp",EDGE,"E989"),sQuery(id+"F0.wireOp",EDGE,"E990"),sQuery(id+"F0.wireOp",EDGE,"E991"),sQuery(id+"F0.wireOp",EDGE,"E992"),sQuery(id+"F0.wireOp",EDGE,"E993"),sQuery(id+"F0.wireOp",EDGE,"E994"),sQuery(id+"F0.wireOp",EDGE,"E995"),sQuery(id+"F0.wireOp",EDGE,"E996"),sQuery(id+"F0.wireOp",EDGE,"E997"),sQuery(id+"F0.wireOp",EDGE,"E998"),sQuery(id+"F0.wireOp",EDGE,"E999"),sQuery(id+"F0.wireOp",EDGE,"E1000"),sQuery(id+"F0.wireOp",EDGE,"E1001"),sQuery(id+"F0.wireOp",EDGE,"E1002"),sQuery(id+"F0.wireOp",EDGE,"E1003"),sQuery(id+"F0.wireOp",EDGE,"E1004"),sQuery(id+"F0.wireOp",EDGE,"E1005"),sQuery(id+"F0.wireOp",EDGE,"E1006"),sQuery(id+"F0.wireOp",EDGE,"E1007"),sQuery(id+"F0.wireOp",EDGE,"E1008"),sQuery(id+"F0.wireOp",EDGE,"E1009"),sQuery(id+"F0.wireOp",EDGE,"E1010"),sQuery(id+"F0.wireOp",EDGE,"E1011"),sQuery(id+"F0.wireOp",EDGE,"E1012"),sQuery(id+"F0.wireOp",EDGE,"E1013"),sQuery(id+"F0.wireOp",EDGE,"E1014"),sQuery(id+"F0.wireOp",EDGE,"E1015"),sQuery(id+"F0.wireOp",EDGE,"E1016"),sQuery(id+"F0.wireOp",EDGE,"E1017"),sQuery(id+"F0.wireOp",EDGE,"E1018"),sQuery(id+"F0.wireOp",EDGE,"E1019"),sQuery(id+"F0.wireOp",EDGE,"E1020"),sQuery(id+"F0.wireOp",EDGE,"E1021"),sQuery(id+"F0.wireOp",EDGE,"E1022"),sQuery(id+"F0.wireOp",EDGE,"E1023"),sQuery(id+"F0.wireOp",EDGE,"E1024"),sQuery(id+"F0.wireOp",EDGE,"E1025"),sQuery(id+"F0.wireOp",EDGE,"E1026"),sQuery(id+"F0.wireOp",EDGE,"E1027"),sQuery(id+"F0.wireOp",EDGE,"E1028"),sQuery(id+"F0.wireOp",EDGE,"E1029"),sQuery(id+"F0.wireOp",EDGE,"E1030"),sQuery(id+"F0.wireOp",EDGE,"E1031"),sQuery(id+"F0.wireOp",EDGE,"E1032"),sQuery(id+"F0.wireOp",EDGE,"E1033"),sQuery(id+"F0.wireOp",EDGE,"E1034"),sQuery(id+"F0.wireOp",EDGE,"E1035"),sQuery(id+"F0.wireOp",EDGE,"E1036"),sQuery(id+"F0.wireOp",EDGE,"E1037"),sQuery(id+"F0.wireOp",EDGE,"E1038"),sQuery(id+"F0.wireOp",EDGE,"E1039"),sQuery(id+"F0.wireOp",EDGE,"E1040"),sQuery(id+"F0.wireOp",EDGE,"E1041"),sQuery(id+"F0.wireOp",EDGE,"E1042"),sQuery(id+"F0.wireOp",EDGE,"E1043"),sQuery(id+"F0.wireOp",EDGE,"E1044"),sQuery(id+"F0.wireOp",EDGE,"E1045"),sQuery(id+"F0.wireOp",EDGE,"E1046"),sQuery(id+"F0.wireOp",EDGE,"E1047"),sQuery(id+"F0.wireOp",EDGE,"E1048"),sQuery(id+"F0.wireOp",EDGE,"E1049"),sQuery(id+"F0.wireOp",EDGE,"E1050"),sQuery(id+"F0.wireOp",EDGE,"E1051"),sQuery(id+"F0.wireOp",EDGE,"E1052"),sQuery(id+"F0.wireOp",EDGE,"E1053"),sQuery(id+"F0.wireOp",EDGE,"E1054"),sQuery(id+"F0.wireOp",EDGE,"E1055"),sQuery(id+"F0.wireOp",EDGE,"E1056"),sQuery(id+"F0.wireOp",EDGE,"E1057"),sQuery(id+"F0.wireOp",EDGE,"E1058"),sQuery(id+"F0.wireOp",EDGE,"E1059"),sQuery(id+"F0.wireOp",EDGE,"E1060"),sQuery(id+"F0.wireOp",EDGE,"E1061"),sQuery(id+"F0.wireOp",EDGE,"E1062"),sQuery(id+"F0.wireOp",EDGE,"E1063"),sQuery(id+"F0.wireOp",EDGE,"E1064"),sQuery(id+"F0.wireOp",EDGE,"E1065"),sQuery(id+"F0.wireOp",EDGE,"E1066"),sQuery(id+"F0.wireOp",EDGE,"E1067"),sQuery(id+"F0.wireOp",EDGE,"E1068"),sQuery(id+"F0.wireOp",EDGE,"E1069"),sQuery(id+"F0.wireOp",EDGE,"E1070"),sQuery(id+"F0.wireOp",EDGE,"E1071"),sQuery(id+"F0.wireOp",EDGE,"E1072"),sQuery(id+"F0.wireOp",EDGE,"E1073"),sQuery(id+"F0.wireOp",EDGE,"E1074"),sQuery(id+"F0.wireOp",EDGE,"E1075"),sQuery(id+"F0.wireOp",EDGE,"E1076"),sQuery(id+"F0.wireOp",EDGE,"E1077"),sQuery(id+"F0.wireOp",EDGE,"E1078"),sQuery(id+"F0.wireOp",EDGE,"E1079"),sQuery(id+"F0.wireOp",EDGE,"E1080"),sQuery(id+"F0.wireOp",EDGE,"E1081"),sQuery(id+"F0.wireOp",EDGE,"E1082"),sQuery(id+"F0.wireOp",EDGE,"E1083"),sQuery(id+"F0.wireOp",EDGE,"E1084"),sQuery(id+"F0.wireOp",EDGE,"E1085"),sQuery(id+"F0.wireOp",EDGE,"E1086"),sQuery(id+"F0.wireOp",EDGE,"E1087"),sQuery(id+"F0.wireOp",EDGE,"E1088"),sQuery(id+"F0.wireOp",EDGE,"E1089"),sQuery(id+"F0.wireOp",EDGE,"E1090"),sQuery(id+"F0.wireOp",EDGE,"E1091"),sQuery(id+"F0.wireOp",EDGE,"E1092"),sQuery(id+"F0.wireOp",EDGE,"E1093"),sQuery(id+"F0.wireOp",EDGE,"E1094"),sQuery(id+"F0.wireOp",EDGE,"E1095"),sQuery(id+"F0.wireOp",EDGE,"E1096"),sQuery(id+"F0.wireOp",EDGE,"E1097"),sQuery(id+"F0.wireOp",EDGE,"E1098"),sQuery(id+"F0.wireOp",EDGE,"E1099"),sQuery(id+"F0.wireOp",EDGE,"E1100"),sQuery(id+"F0.wireOp",EDGE,"E1101"),sQuery(id+"F0.wireOp",EDGE,"E1102"),sQuery(id+"F0.wireOp",EDGE,"E1103"),sQuery(id+"F0.wireOp",EDGE,"E1104"),sQuery(id+"F0.wireOp",EDGE,"E1105"),sQuery(id+"F0.wireOp",EDGE,"E1106"),sQuery(id+"F0.wireOp",EDGE,"E1107"),sQuery(id+"F0.wireOp",EDGE,"E1108"),sQuery(id+"F0.wireOp",EDGE,"E1109"),sQuery(id+"F0.wireOp",EDGE,"E1110"),sQuery(id+"F0.wireOp",EDGE,"E1111"),sQuery(id+"F0.wireOp",EDGE,"E1112"),sQuery(id+"F0.wireOp",EDGE,"E1113"),sQuery(id+"F0.wireOp",EDGE,"E1114"),sQuery(id+"F0.wireOp",EDGE,"E1115"),sQuery(id+"F0.wireOp",EDGE,"E1116"),sQuery(id+"F0.wireOp",EDGE,"E1117"),sQuery(id+"F0.wireOp",EDGE,"E1118"),sQuery(id+"F0.wireOp",EDGE,"E1119"),sQuery(id+"F0.wireOp",EDGE,"E1120"),sQuery(id+"F0.wireOp",EDGE,"E1121"),sQuery(id+"F0.wireOp",EDGE,"E1122"),sQuery(id+"F0.wireOp",EDGE,"E1123"),sQuery(id+"F0.wireOp",EDGE,"E1124"),sQuery(id+"F0.wireOp",EDGE,"E1125"),sQuery(id+"F0.wireOp",EDGE,"E1126"),sQuery(id+"F0.wireOp",EDGE,"E1127"),sQuery(id+"F0.wireOp",EDGE,"E1128"),sQuery(id+"F0.wireOp",EDGE,"E1129"),sQuery(id+"F0.wireOp",EDGE,"E1130"),sQuery(id+"F0.wireOp",EDGE,"E1131"),sQuery(id+"F0.wireOp",EDGE,"E1132"),sQuery(id+"F0.wireOp",EDGE,"E1133"),sQuery(id+"F0.wireOp",EDGE,"E1134"),sQuery(id+"F0.wireOp",EDGE,"E1135"),sQuery(id+"F0.wireOp",EDGE,"E1136"),sQuery(id+"F0.wireOp",EDGE,"E1137"),sQuery(id+"F0.wireOp",EDGE,"E1138"),sQuery(id+"F0.wireOp",EDGE,"E1139"),sQuery(id+"F0.wireOp",EDGE,"E1140"),sQuery(id+"F0.wireOp",EDGE,"E1141"),sQuery(id+"F0.wireOp",EDGE,"E1142"),sQuery(id+"F0.wireOp",EDGE,"E1143"),sQuery(id+"F0.wireOp",EDGE,"E1144"),sQuery(id+"F0.wireOp",EDGE,"E1145"),sQuery(id+"F0.wireOp",EDGE,"E1146"),sQuery(id+"F0.wireOp",EDGE,"E1147"),sQuery(id+"F0.wireOp",EDGE,"E1148"),sQuery(id+"F0.wireOp",EDGE,"E1149"),sQuery(id+"F0.wireOp",EDGE,"E1150"),sQuery(id+"F0.wireOp",EDGE,"E1151"),sQuery(id+"F0.wireOp",EDGE,"E1152"),sQuery(id+"F0.wireOp",EDGE,"E1153"),sQuery(id+"F0.wireOp",EDGE,"E1154"),sQuery(id+"F0.wireOp",EDGE,"E1155"),sQuery(id+"F0.wireOp",EDGE,"E1156"),sQuery(id+"F0.wireOp",EDGE,"E1157"),sQuery(id+"F0.wireOp",EDGE,"E1158"),sQuery(id+"F0.wireOp",EDGE,"E1159"),sQuery(id+"F0.wireOp",EDGE,"E1160"),sQuery(id+"F0.wireOp",EDGE,"E1161"),sQuery(id+"F0.wireOp",EDGE,"E1162"),sQuery(id+"F0.wireOp",EDGE,"E1163"),sQuery(id+"F0.wireOp",EDGE,"E1164"),sQuery(id+"F0.wireOp",EDGE,"E1165"),sQuery(id+"F0.wireOp",EDGE,"E1166"),sQuery(id+"F0.wireOp",EDGE,"E1167"),sQuery(id+"F0.wireOp",EDGE,"E1168"),sQuery(id+"F0.wireOp",EDGE,"E1169"),sQuery(id+"F0.wireOp",EDGE,"E1170"),sQuery(id+"F0.wireOp",EDGE,"E1171"),sQuery(id+"F0.wireOp",EDGE,"E1172"),sQuery(id+"F0.wireOp",EDGE,"E1173"),sQuery(id+"F0.wireOp",EDGE,"E1174"),sQuery(id+"F0.wireOp",EDGE,"E1175"),sQuery(id+"F0.wireOp",EDGE,"E1176"),sQuery(id+"F0.wireOp",EDGE,"E1177"),sQuery(id+"F0.wireOp",EDGE,"E1178"),sQuery(id+"F0.wireOp",EDGE,"E1179")])],"isStart":false});
            var sketch = newSketch(context, id + "F4", { "sketchPlane" : qUnion([Q0])});
            skLineSegment(sketch, "E1181", {"start": v(4.81, 0) * mm, "end": v(5.87, 0) * mm});
            skLineSegment(sketch, "E1182", {"start": v(5.87, 0) * mm, "end": v(5.88, 0) * mm});
            skLineSegment(sketch, "E1183", {"start": v(5.88, 0) * mm, "end": v(5.9, 0) * mm});
            skLineSegment(sketch, "E1184", {"start": v(5.9, 0) * mm, "end": v(5.92, 0) * mm});
            skLineSegment(sketch, "E1185", {"start": v(5.92, 0) * mm, "end": v(5.95, 0) * mm});
            skLineSegment(sketch, "E1186", {"start": v(5.95, 0) * mm, "end": v(5.98, 0.01) * mm});
            skLineSegment(sketch, "E1187", {"start": v(5.98, 0.01) * mm, "end": v(6.02, 0.02) * mm});
            skLineSegment(sketch, "E1188", {"start": v(6.02, 0.02) * mm, "end": v(6.07, 0.03) * mm});
            skLineSegment(sketch, "E1189", {"start": v(6.07, 0.03) * mm, "end": v(6.13, 0.05) * mm});
            skLineSegment(sketch, "E1190", {"start": v(6.13, 0.05) * mm, "end": v(6.19, 0.07) * mm});
            skLineSegment(sketch, "E1191", {"start": v(6.19, 0.07) * mm, "end": v(6.25, 0.1) * mm});
            skLineSegment(sketch, "E1192", {"start": v(6.25, 0.1) * mm, "end": v(6.33, 0.12) * mm});
            skLineSegment(sketch, "E1193", {"start": v(6.33, 0.12) * mm, "end": v(6.4, 0.16) * mm});
            skLineSegment(sketch, "E1194", {"start": v(6.4, 0.16) * mm, "end": v(6.49, 0.2) * mm});
            skLineSegment(sketch, "E1195", {"start": v(6.49, 0.2) * mm, "end": v(6.58, 0.25) * mm});
            skLineSegment(sketch, "E1196", {"start": v(6.58, 0.25) * mm, "end": v(6.67, 0.3) * mm});
            skLineSegment(sketch, "E1197", {"start": v(6.67, 0.3) * mm, "end": v(6.77, 0.36) * mm});
            skLineSegment(sketch, "E1198", {"start": v(6.77, 0.36) * mm, "end": v(6.87, 0.43) * mm});
            skLineSegment(sketch, "E1199", {"start": v(6.87, 0.43) * mm, "end": v(6.97, 0.5) * mm});
            skLineSegment(sketch, "E1200", {"start": v(6.97, 0.5) * mm, "end": v(7.08, 0.59) * mm});
            skLineSegment(sketch, "E1201", {"start": v(7.08, 0.59) * mm, "end": v(7.19, 0.68) * mm});
            skLineSegment(sketch, "E1202", {"start": v(7.19, 0.68) * mm, "end": v(7.3, 0.78) * mm});
            skLineSegment(sketch, "E1203", {"start": v(7.3, 0.78) * mm, "end": v(7.41, 0.9) * mm});
            skLineSegment(sketch, "E1204", {"start": v(7.41, 0.9) * mm, "end": v(7.43, 1) * mm});
            skLineSegment(sketch, "E1205", {"start": v(7.43, 1) * mm, "end": v(7.34, 1.52) * mm});
            skLineSegment(sketch, "E1206", {"start": v(7.34, 1.52) * mm, "end": v(7.3, 1.61) * mm});
            skLineSegment(sketch, "E1207", {"start": v(7.3, 1.61) * mm, "end": v(7.15, 1.68) * mm});
            skLineSegment(sketch, "E1208", {"start": v(7.15, 1.68) * mm, "end": v(7.01, 1.73) * mm});
            skLineSegment(sketch, "E1209", {"start": v(7.01, 1.73) * mm, "end": v(6.88, 1.78) * mm});
            skLineSegment(sketch, "E1210", {"start": v(6.88, 1.78) * mm, "end": v(6.75, 1.83) * mm});
            skLineSegment(sketch, "E1211", {"start": v(6.75, 1.83) * mm, "end": v(6.62, 1.87) * mm});
            skLineSegment(sketch, "E1212", {"start": v(6.62, 1.87) * mm, "end": v(6.5, 1.9) * mm});
            skLineSegment(sketch, "E1213", {"start": v(6.5, 1.9) * mm, "end": v(6.4, 1.92) * mm});
            skLineSegment(sketch, "E1214", {"start": v(6.4, 1.92) * mm, "end": v(6.29, 1.94) * mm});
            skLineSegment(sketch, "E1215", {"start": v(6.29, 1.94) * mm, "end": v(6.2, 1.96) * mm});
            skLineSegment(sketch, "E1216", {"start": v(6.2, 1.96) * mm, "end": v(6.1, 1.97) * mm});
            skLineSegment(sketch, "E1217", {"start": v(6.1, 1.97) * mm, "end": v(6.01, 1.97) * mm});
            skLineSegment(sketch, "E1218", {"start": v(6.01, 1.97) * mm, "end": v(5.93, 1.98) * mm});
            skLineSegment(sketch, "E1219", {"start": v(5.93, 1.98) * mm, "end": v(5.86, 1.98) * mm});
            skLineSegment(sketch, "E1220", {"start": v(5.86, 1.98) * mm, "end": v(5.8, 1.98) * mm});
            skLineSegment(sketch, "E1221", {"start": v(5.8, 1.98) * mm, "end": v(5.74, 1.97) * mm});
            skLineSegment(sketch, "E1222", {"start": v(5.74, 1.97) * mm, "end": v(5.7, 1.97) * mm});
            skLineSegment(sketch, "E1223", {"start": v(5.7, 1.97) * mm, "end": v(5.65, 1.96) * mm});
            skLineSegment(sketch, "E1224", {"start": v(5.65, 1.96) * mm, "end": v(5.61, 1.96) * mm});
            skLineSegment(sketch, "E1225", {"start": v(5.61, 1.96) * mm, "end": v(5.59, 1.95) * mm});
            skLineSegment(sketch, "E1226", {"start": v(5.59, 1.95) * mm, "end": v(5.56, 1.95) * mm});
            skLineSegment(sketch, "E1227", {"start": v(5.56, 1.95) * mm, "end": v(5.55, 1.94) * mm});
            skLineSegment(sketch, "E1228", {"start": v(5.55, 1.94) * mm, "end": v(5.54, 1.94) * mm});
            skLineSegment(sketch, "E1229", {"start": v(5.54, 1.94) * mm, "end": v(4.54, 1.6) * mm});
            skLineSegment(sketch, "E1230", {"start": v(4.54, 1.6) * mm, "end": v(3.9, 2.83) * mm});
            skLineSegment(sketch, "E1231", {"start": v(3.9, 2.83) * mm, "end": v(4.75, 3.45) * mm});
            skLineSegment(sketch, "E1232", {"start": v(4.75, 3.45) * mm, "end": v(4.76, 3.46) * mm});
            skLineSegment(sketch, "E1233", {"start": v(4.76, 3.46) * mm, "end": v(4.77, 3.47) * mm});
            skLineSegment(sketch, "E1234", {"start": v(4.77, 3.47) * mm, "end": v(4.78, 3.48) * mm});
            skLineSegment(sketch, "E1235", {"start": v(4.78, 3.48) * mm, "end": v(4.8, 3.5) * mm});
            skLineSegment(sketch, "E1236", {"start": v(4.8, 3.5) * mm, "end": v(4.83, 3.53) * mm});
            skLineSegment(sketch, "E1237", {"start": v(4.83, 3.53) * mm, "end": v(4.86, 3.56) * mm});
            skLineSegment(sketch, "E1238", {"start": v(4.86, 3.56) * mm, "end": v(4.9, 3.6) * mm});
            skLineSegment(sketch, "E1239", {"start": v(4.9, 3.6) * mm, "end": v(4.93, 3.64) * mm});
            skLineSegment(sketch, "E1240", {"start": v(4.93, 3.64) * mm, "end": v(4.96, 3.7) * mm});
            skLineSegment(sketch, "E1241", {"start": v(4.96, 3.7) * mm, "end": v(5, 3.75) * mm});
            skLineSegment(sketch, "E1242", {"start": v(5, 3.75) * mm, "end": v(5.05, 3.82) * mm});
            skLineSegment(sketch, "E1243", {"start": v(5.05, 3.82) * mm, "end": v(5.09, 3.9) * mm});
            skLineSegment(sketch, "E1244", {"start": v(5.09, 3.9) * mm, "end": v(5.13, 3.98) * mm});
            skLineSegment(sketch, "E1245", {"start": v(5.13, 3.98) * mm, "end": v(5.18, 4.07) * mm});
            skLineSegment(sketch, "E1246", {"start": v(5.18, 4.07) * mm, "end": v(5.22, 4.16) * mm});
            skLineSegment(sketch, "E1247", {"start": v(5.22, 4.16) * mm, "end": v(5.26, 4.27) * mm});
            skLineSegment(sketch, "E1248", {"start": v(5.26, 4.27) * mm, "end": v(5.3, 4.39) * mm});
            skLineSegment(sketch, "E1249", {"start": v(5.3, 4.39) * mm, "end": v(5.34, 4.5) * mm});
            skLineSegment(sketch, "E1250", {"start": v(5.34, 4.5) * mm, "end": v(5.38, 4.64) * mm});
            skLineSegment(sketch, "E1251", {"start": v(5.38, 4.64) * mm, "end": v(5.42, 4.78) * mm});
            skLineSegment(sketch, "E1252", {"start": v(5.42, 4.78) * mm, "end": v(5.45, 4.92) * mm});
            skLineSegment(sketch, "E1253", {"start": v(5.45, 4.92) * mm, "end": v(5.47, 5.08) * mm});
            skLineSegment(sketch, "E1254", {"start": v(5.47, 5.08) * mm, "end": v(5.43, 5.18) * mm});
            skLineSegment(sketch, "E1255", {"start": v(5.43, 5.18) * mm, "end": v(5.05, 5.54) * mm});
            skLineSegment(sketch, "E1256", {"start": v(5.05, 5.54) * mm, "end": v(4.95, 5.59) * mm});
            skLineSegment(sketch, "E1257", {"start": v(4.95, 5.59) * mm, "end": v(4.8, 5.56) * mm});
            skLineSegment(sketch, "E1258", {"start": v(4.8, 5.56) * mm, "end": v(4.65, 5.52) * mm});
            skLineSegment(sketch, "E1259", {"start": v(4.65, 5.52) * mm, "end": v(4.51, 5.49) * mm});
            skLineSegment(sketch, "E1260", {"start": v(4.51, 5.49) * mm, "end": v(4.38, 5.45) * mm});
            skLineSegment(sketch, "E1261", {"start": v(4.38, 5.45) * mm, "end": v(4.26, 5.4) * mm});
            skLineSegment(sketch, "E1262", {"start": v(4.26, 5.4) * mm, "end": v(4.15, 5.36) * mm});
            skLineSegment(sketch, "E1263", {"start": v(4.15, 5.36) * mm, "end": v(4.04, 5.31) * mm});
            skLineSegment(sketch, "E1264", {"start": v(4.04, 5.31) * mm, "end": v(3.95, 5.27) * mm});
            skLineSegment(sketch, "E1265", {"start": v(3.95, 5.27) * mm, "end": v(3.86, 5.22) * mm});
            skLineSegment(sketch, "E1266", {"start": v(3.86, 5.22) * mm, "end": v(3.78, 5.18) * mm});
            skLineSegment(sketch, "E1267", {"start": v(3.78, 5.18) * mm, "end": v(3.7, 5.13) * mm});
            skLineSegment(sketch, "E1268", {"start": v(3.7, 5.13) * mm, "end": v(3.64, 5.09) * mm});
            skLineSegment(sketch, "E1269", {"start": v(3.64, 5.09) * mm, "end": v(3.58, 5.05) * mm});
            skLineSegment(sketch, "E1270", {"start": v(3.58, 5.05) * mm, "end": v(3.53, 5) * mm});
            skLineSegment(sketch, "E1271", {"start": v(3.53, 5) * mm, "end": v(3.48, 4.97) * mm});
            skLineSegment(sketch, "E1272", {"start": v(3.48, 4.97) * mm, "end": v(3.45, 4.94) * mm});
            skLineSegment(sketch, "E1273", {"start": v(3.45, 4.94) * mm, "end": v(3.42, 4.9) * mm});
            skLineSegment(sketch, "E1274", {"start": v(3.42, 4.9) * mm, "end": v(3.39, 4.88) * mm});
            skLineSegment(sketch, "E1275", {"start": v(3.39, 4.88) * mm, "end": v(3.37, 4.86) * mm});
            skLineSegment(sketch, "E1276", {"start": v(3.37, 4.86) * mm, "end": v(3.36, 4.85) * mm});
            skLineSegment(sketch, "E1277", {"start": v(3.36, 4.85) * mm, "end": v(3.35, 4.84) * mm});
            skLineSegment(sketch, "E1278", {"start": v(3.35, 4.84) * mm, "end": v(3.34, 4.83) * mm});
            skLineSegment(sketch, "E1279", {"start": v(3.34, 4.83) * mm, "end": v(2.74, 3.96) * mm});
            skLineSegment(sketch, "E1280", {"start": v(2.74, 3.96) * mm, "end": v(1.49, 4.58) * mm});
            skLineSegment(sketch, "E1281", {"start": v(1.49, 4.58) * mm, "end": v(1.82, 5.59) * mm});
            skLineSegment(sketch, "E1282", {"start": v(1.82, 5.59) * mm, "end": v(1.82, 5.6) * mm});
            skLineSegment(sketch, "E1283", {"start": v(1.82, 5.6) * mm, "end": v(1.82, 5.6) * mm});
            skLineSegment(sketch, "E1284", {"start": v(1.82, 5.6) * mm, "end": v(1.82, 5.63) * mm});
            skLineSegment(sketch, "E1285", {"start": v(1.82, 5.63) * mm, "end": v(1.83, 5.66) * mm});
            skLineSegment(sketch, "E1286", {"start": v(1.83, 5.66) * mm, "end": v(1.83, 5.7) * mm});
            skLineSegment(sketch, "E1287", {"start": v(1.83, 5.7) * mm, "end": v(1.84, 5.73) * mm});
            skLineSegment(sketch, "E1288", {"start": v(1.84, 5.73) * mm, "end": v(1.84, 5.78) * mm});
            skLineSegment(sketch, "E1289", {"start": v(1.84, 5.78) * mm, "end": v(1.84, 5.84) * mm});
            skLineSegment(sketch, "E1290", {"start": v(1.84, 5.84) * mm, "end": v(1.84, 5.9) * mm});
            skLineSegment(sketch, "E1291", {"start": v(1.84, 5.9) * mm, "end": v(1.84, 5.98) * mm});
            skLineSegment(sketch, "E1292", {"start": v(1.84, 5.98) * mm, "end": v(1.84, 6.06) * mm});
            skLineSegment(sketch, "E1293", {"start": v(1.84, 6.06) * mm, "end": v(1.83, 6.14) * mm});
            skLineSegment(sketch, "E1294", {"start": v(1.83, 6.14) * mm, "end": v(1.81, 6.23) * mm});
            skLineSegment(sketch, "E1295", {"start": v(1.81, 6.23) * mm, "end": v(1.8, 6.33) * mm});
            skLineSegment(sketch, "E1296", {"start": v(1.8, 6.33) * mm, "end": v(1.78, 6.44) * mm});
            skLineSegment(sketch, "E1297", {"start": v(1.78, 6.44) * mm, "end": v(1.75, 6.55) * mm});
            skLineSegment(sketch, "E1298", {"start": v(1.75, 6.55) * mm, "end": v(1.71, 6.67) * mm});
            skLineSegment(sketch, "E1299", {"start": v(1.71, 6.67) * mm, "end": v(1.67, 6.79) * mm});
            skLineSegment(sketch, "E1300", {"start": v(1.67, 6.79) * mm, "end": v(1.63, 6.92) * mm});
            skLineSegment(sketch, "E1301", {"start": v(1.63, 6.92) * mm, "end": v(1.57, 7.05) * mm});
            skLineSegment(sketch, "E1302", {"start": v(1.57, 7.05) * mm, "end": v(1.51, 7.19) * mm});
            skLineSegment(sketch, "E1303", {"start": v(1.51, 7.19) * mm, "end": v(1.44, 7.33) * mm});
            skLineSegment(sketch, "E1304", {"start": v(1.44, 7.33) * mm, "end": v(1.35, 7.38) * mm});
            skLineSegment(sketch, "E1305", {"start": v(1.35, 7.38) * mm, "end": v(0.83, 7.45) * mm});
            skLineSegment(sketch, "E1306", {"start": v(0.83, 7.45) * mm, "end": v(0.72, 7.43) * mm});
            skLineSegment(sketch, "E1307", {"start": v(0.72, 7.43) * mm, "end": v(0.62, 7.32) * mm});
            skLineSegment(sketch, "E1308", {"start": v(0.62, 7.32) * mm, "end": v(0.52, 7.2) * mm});
            skLineSegment(sketch, "E1309", {"start": v(0.52, 7.2) * mm, "end": v(0.43, 7.1) * mm});
            skLineSegment(sketch, "E1310", {"start": v(0.43, 7.1) * mm, "end": v(0.35, 6.98) * mm});
            skLineSegment(sketch, "E1311", {"start": v(0.35, 6.98) * mm, "end": v(0.27, 6.88) * mm});
            skLineSegment(sketch, "E1312", {"start": v(0.27, 6.88) * mm, "end": v(0.2, 6.77) * mm});
            skLineSegment(sketch, "E1313", {"start": v(0.2, 6.77) * mm, "end": v(0.15, 6.68) * mm});
            skLineSegment(sketch, "E1314", {"start": v(0.15, 6.68) * mm, "end": v(0.1, 6.58) * mm});
            skLineSegment(sketch, "E1315", {"start": v(0.1, 6.58) * mm, "end": v(0.05, 6.5) * mm});
            skLineSegment(sketch, "E1316", {"start": v(0.05, 6.5) * mm, "end": v(0.01, 6.4) * mm});
            skLineSegment(sketch, "E1317", {"start": v(0.01, 6.4) * mm, "end": v(-0.02, 6.33) * mm});
            skLineSegment(sketch, "E1318", {"start": v(-0.02, 6.33) * mm, "end": v(-0.05, 6.25) * mm});
            skLineSegment(sketch, "E1319", {"start": v(-0.05, 6.25) * mm, "end": v(-0.07, 6.19) * mm});
            skLineSegment(sketch, "E1320", {"start": v(-0.07, 6.19) * mm, "end": v(-0.09, 6.13) * mm});
            skLineSegment(sketch, "E1321", {"start": v(-0.09, 6.13) * mm, "end": v(-0.1, 6.07) * mm});
            skLineSegment(sketch, "E1322", {"start": v(-0.1, 6.07) * mm, "end": v(-0.11, 6.02) * mm});
            skLineSegment(sketch, "E1323", {"start": v(-0.11, 6.02) * mm, "end": v(-0.12, 5.98) * mm});
            skLineSegment(sketch, "E1324", {"start": v(-0.12, 5.98) * mm, "end": v(-0.13, 5.94) * mm});
            skLineSegment(sketch, "E1325", {"start": v(-0.13, 5.94) * mm, "end": v(-0.13, 5.92) * mm});
            skLineSegment(sketch, "E1326", {"start": v(-0.13, 5.92) * mm, "end": v(-0.13, 5.9) * mm});
            skLineSegment(sketch, "E1327", {"start": v(-0.13, 5.9) * mm, "end": v(-0.13, 5.88) * mm});
            skLineSegment(sketch, "E1328", {"start": v(-0.13, 5.88) * mm, "end": v(-0.13, 5.87) * mm});
            skLineSegment(sketch, "E1329", {"start": v(-0.13, 5.87) * mm, "end": v(-0.1, 4.81) * mm});
            skLineSegment(sketch, "E1330", {"start": v(-0.1, 4.81) * mm, "end": v(-1.49, 4.58) * mm});
            skLineSegment(sketch, "E1331", {"start": v(-1.49, 4.58) * mm, "end": v(-1.82, 5.59) * mm});
            skLineSegment(sketch, "E1332", {"start": v(-1.82, 5.59) * mm, "end": v(-1.82, 5.6) * mm});
            skLineSegment(sketch, "E1333", {"start": v(-1.82, 5.6) * mm, "end": v(-1.82, 5.6) * mm});
            skLineSegment(sketch, "E1334", {"start": v(-1.82, 5.6) * mm, "end": v(-1.83, 5.63) * mm});
            skLineSegment(sketch, "E1335", {"start": v(-1.83, 5.63) * mm, "end": v(-1.84, 5.65) * mm});
            skLineSegment(sketch, "E1336", {"start": v(-1.84, 5.65) * mm, "end": v(-1.86, 5.68) * mm});
            skLineSegment(sketch, "E1337", {"start": v(-1.86, 5.68) * mm, "end": v(-1.88, 5.72) * mm});
            skLineSegment(sketch, "E1338", {"start": v(-1.88, 5.72) * mm, "end": v(-1.9, 5.76) * mm});
            skLineSegment(sketch, "E1339", {"start": v(-1.9, 5.76) * mm, "end": v(-1.94, 5.81) * mm});
            skLineSegment(sketch, "E1340", {"start": v(-1.94, 5.81) * mm, "end": v(-1.98, 5.86) * mm});
            skLineSegment(sketch, "E1341", {"start": v(-1.98, 5.86) * mm, "end": v(-2.02, 5.92) * mm});
            skLineSegment(sketch, "E1342", {"start": v(-2.02, 5.92) * mm, "end": v(-2.07, 5.98) * mm});
            skLineSegment(sketch, "E1343", {"start": v(-2.07, 5.98) * mm, "end": v(-2.13, 6.04) * mm});
            skLineSegment(sketch, "E1344", {"start": v(-2.13, 6.04) * mm, "end": v(-2.2, 6.1) * mm});
            skLineSegment(sketch, "E1345", {"start": v(-2.2, 6.1) * mm, "end": v(-2.27, 6.18) * mm});
            skLineSegment(sketch, "E1346", {"start": v(-2.27, 6.18) * mm, "end": v(-2.35, 6.25) * mm});
            skLineSegment(sketch, "E1347", {"start": v(-2.35, 6.25) * mm, "end": v(-2.44, 6.32) * mm});
            skLineSegment(sketch, "E1348", {"start": v(-2.44, 6.32) * mm, "end": v(-2.53, 6.4) * mm});
            skLineSegment(sketch, "E1349", {"start": v(-2.53, 6.4) * mm, "end": v(-2.64, 6.48) * mm});
            skLineSegment(sketch, "E1350", {"start": v(-2.64, 6.48) * mm, "end": v(-2.75, 6.55) * mm});
            skLineSegment(sketch, "E1351", {"start": v(-2.75, 6.55) * mm, "end": v(-2.87, 6.63) * mm});
            skLineSegment(sketch, "E1352", {"start": v(-2.87, 6.63) * mm, "end": v(-3, 6.7) * mm});
            skLineSegment(sketch, "E1353", {"start": v(-3, 6.7) * mm, "end": v(-3.14, 6.78) * mm});
            skLineSegment(sketch, "E1354", {"start": v(-3.14, 6.78) * mm, "end": v(-3.25, 6.76) * mm});
            skLineSegment(sketch, "E1355", {"start": v(-3.25, 6.76) * mm, "end": v(-3.71, 6.52) * mm});
            skLineSegment(sketch, "E1356", {"start": v(-3.71, 6.52) * mm, "end": v(-3.79, 6.44) * mm});
            skLineSegment(sketch, "E1357", {"start": v(-3.79, 6.44) * mm, "end": v(-3.8, 6.28) * mm});
            skLineSegment(sketch, "E1358", {"start": v(-3.8, 6.28) * mm, "end": v(-3.82, 6.13) * mm});
            skLineSegment(sketch, "E1359", {"start": v(-3.82, 6.13) * mm, "end": v(-3.82, 5.99) * mm});
            skLineSegment(sketch, "E1360", {"start": v(-3.82, 5.99) * mm, "end": v(-3.82, 5.85) * mm});
            skLineSegment(sketch, "E1361", {"start": v(-3.82, 5.85) * mm, "end": v(-3.82, 5.72) * mm});
            skLineSegment(sketch, "E1362", {"start": v(-3.82, 5.72) * mm, "end": v(-3.81, 5.6) * mm});
            skLineSegment(sketch, "E1363", {"start": v(-3.81, 5.6) * mm, "end": v(-3.8, 5.49) * mm});
            skLineSegment(sketch, "E1364", {"start": v(-3.8, 5.49) * mm, "end": v(-3.8, 5.38) * mm});
            skLineSegment(sketch, "E1365", {"start": v(-3.8, 5.38) * mm, "end": v(-3.77, 5.28) * mm});
            skLineSegment(sketch, "E1366", {"start": v(-3.77, 5.28) * mm, "end": v(-3.76, 5.2) * mm});
            skLineSegment(sketch, "E1367", {"start": v(-3.76, 5.2) * mm, "end": v(-3.74, 5.1) * mm});
            skLineSegment(sketch, "E1368", {"start": v(-3.74, 5.1) * mm, "end": v(-3.72, 5.03) * mm});
            skLineSegment(sketch, "E1369", {"start": v(-3.72, 5.03) * mm, "end": v(-3.7, 4.96) * mm});
            skLineSegment(sketch, "E1370", {"start": v(-3.7, 4.96) * mm, "end": v(-3.67, 4.9) * mm});
            skLineSegment(sketch, "E1371", {"start": v(-3.67, 4.9) * mm, "end": v(-3.65, 4.85) * mm});
            skLineSegment(sketch, "E1372", {"start": v(-3.65, 4.85) * mm, "end": v(-3.63, 4.8) * mm});
            skLineSegment(sketch, "E1373", {"start": v(-3.63, 4.8) * mm, "end": v(-3.61, 4.77) * mm});
            skLineSegment(sketch, "E1374", {"start": v(-3.61, 4.77) * mm, "end": v(-3.6, 4.73) * mm});
            skLineSegment(sketch, "E1375", {"start": v(-3.6, 4.73) * mm, "end": v(-3.58, 4.7) * mm});
            skLineSegment(sketch, "E1376", {"start": v(-3.58, 4.7) * mm, "end": v(-3.57, 4.69) * mm});
            skLineSegment(sketch, "E1377", {"start": v(-3.57, 4.69) * mm, "end": v(-3.56, 4.68) * mm});
            skLineSegment(sketch, "E1378", {"start": v(-3.56, 4.68) * mm, "end": v(-3.56, 4.67) * mm});
            skLineSegment(sketch, "E1379", {"start": v(-3.56, 4.67) * mm, "end": v(-2.92, 3.83) * mm});
            skLineSegment(sketch, "E1380", {"start": v(-2.92, 3.83) * mm, "end": v(-3.9, 2.83) * mm});
            skLineSegment(sketch, "E1381", {"start": v(-3.9, 2.83) * mm, "end": v(-4.75, 3.45) * mm});
            skLineSegment(sketch, "E1382", {"start": v(-4.75, 3.45) * mm, "end": v(-4.76, 3.46) * mm});
            skLineSegment(sketch, "E1383", {"start": v(-4.76, 3.46) * mm, "end": v(-4.77, 3.46) * mm});
            skLineSegment(sketch, "E1384", {"start": v(-4.77, 3.46) * mm, "end": v(-4.79, 3.47) * mm});
            skLineSegment(sketch, "E1385", {"start": v(-4.79, 3.47) * mm, "end": v(-4.81, 3.49) * mm});
            skLineSegment(sketch, "E1386", {"start": v(-4.81, 3.49) * mm, "end": v(-4.85, 3.5) * mm});
            skLineSegment(sketch, "E1387", {"start": v(-4.85, 3.5) * mm, "end": v(-4.89, 3.52) * mm});
            skLineSegment(sketch, "E1388", {"start": v(-4.89, 3.52) * mm, "end": v(-4.93, 3.54) * mm});
            skLineSegment(sketch, "E1389", {"start": v(-4.93, 3.54) * mm, "end": v(-4.99, 3.56) * mm});
            skLineSegment(sketch, "E1390", {"start": v(-4.99, 3.56) * mm, "end": v(-5.05, 3.58) * mm});
            skLineSegment(sketch, "E1391", {"start": v(-5.05, 3.58) * mm, "end": v(-5.12, 3.6) * mm});
            skLineSegment(sketch, "E1392", {"start": v(-5.12, 3.6) * mm, "end": v(-5.2, 3.62) * mm});
            skLineSegment(sketch, "E1393", {"start": v(-5.2, 3.62) * mm, "end": v(-5.28, 3.64) * mm});
            skLineSegment(sketch, "E1394", {"start": v(-5.28, 3.64) * mm, "end": v(-5.37, 3.65) * mm});
            skLineSegment(sketch, "E1395", {"start": v(-5.37, 3.65) * mm, "end": v(-5.47, 3.67) * mm});
            skLineSegment(sketch, "E1396", {"start": v(-5.47, 3.67) * mm, "end": v(-5.57, 3.68) * mm});
            skLineSegment(sketch, "E1397", {"start": v(-5.57, 3.68) * mm, "end": v(-5.69, 3.69) * mm});
            skLineSegment(sketch, "E1398", {"start": v(-5.69, 3.69) * mm, "end": v(-5.8, 3.69) * mm});
            skLineSegment(sketch, "E1399", {"start": v(-5.8, 3.69) * mm, "end": v(-5.94, 3.69) * mm});
            skLineSegment(sketch, "E1400", {"start": v(-5.94, 3.69) * mm, "end": v(-6.07, 3.68) * mm});
            skLineSegment(sketch, "E1401", {"start": v(-6.07, 3.68) * mm, "end": v(-6.22, 3.67) * mm});
            skLineSegment(sketch, "E1402", {"start": v(-6.22, 3.67) * mm, "end": v(-6.37, 3.66) * mm});
            skLineSegment(sketch, "E1403", {"start": v(-6.37, 3.66) * mm, "end": v(-6.52, 3.64) * mm});
            skLineSegment(sketch, "E1404", {"start": v(-6.52, 3.64) * mm, "end": v(-6.6, 3.56) * mm});
            skLineSegment(sketch, "E1405", {"start": v(-6.6, 3.56) * mm, "end": v(-6.83, 3.09) * mm});
            skLineSegment(sketch, "E1406", {"start": v(-6.83, 3.09) * mm, "end": v(-6.85, 2.98) * mm});
            skLineSegment(sketch, "E1407", {"start": v(-6.85, 2.98) * mm, "end": v(-6.77, 2.85) * mm});
            skLineSegment(sketch, "E1408", {"start": v(-6.77, 2.85) * mm, "end": v(-6.7, 2.72) * mm});
            skLineSegment(sketch, "E1409", {"start": v(-6.7, 2.72) * mm, "end": v(-6.61, 2.6) * mm});
            skLineSegment(sketch, "E1410", {"start": v(-6.61, 2.6) * mm, "end": v(-6.53, 2.49) * mm});
            skLineSegment(sketch, "E1411", {"start": v(-6.53, 2.49) * mm, "end": v(-6.46, 2.38) * mm});
            skLineSegment(sketch, "E1412", {"start": v(-6.46, 2.38) * mm, "end": v(-6.38, 2.3) * mm});
            skLineSegment(sketch, "E1413", {"start": v(-6.38, 2.3) * mm, "end": v(-6.3, 2.2) * mm});
            skLineSegment(sketch, "E1414", {"start": v(-6.3, 2.2) * mm, "end": v(-6.23, 2.13) * mm});
            skLineSegment(sketch, "E1415", {"start": v(-6.23, 2.13) * mm, "end": v(-6.16, 2.06) * mm});
            skLineSegment(sketch, "E1416", {"start": v(-6.16, 2.06) * mm, "end": v(-6.1, 2) * mm});
            skLineSegment(sketch, "E1417", {"start": v(-6.1, 2) * mm, "end": v(-6.02, 1.94) * mm});
            skLineSegment(sketch, "E1418", {"start": v(-6.02, 1.94) * mm, "end": v(-5.96, 1.89) * mm});
            skLineSegment(sketch, "E1419", {"start": v(-5.96, 1.89) * mm, "end": v(-5.9, 1.84) * mm});
            skLineSegment(sketch, "E1420", {"start": v(-5.9, 1.84) * mm, "end": v(-5.85, 1.8) * mm});
            skLineSegment(sketch, "E1421", {"start": v(-5.85, 1.8) * mm, "end": v(-5.8, 1.78) * mm});
            skLineSegment(sketch, "E1422", {"start": v(-5.8, 1.78) * mm, "end": v(-5.76, 1.75) * mm});
            skLineSegment(sketch, "E1423", {"start": v(-5.76, 1.75) * mm, "end": v(-5.72, 1.73) * mm});
            skLineSegment(sketch, "E1424", {"start": v(-5.72, 1.73) * mm, "end": v(-5.7, 1.71) * mm});
            skLineSegment(sketch, "E1425", {"start": v(-5.7, 1.71) * mm, "end": v(-5.67, 1.7) * mm});
            skLineSegment(sketch, "E1426", {"start": v(-5.67, 1.7) * mm, "end": v(-5.65, 1.7) * mm});
            skLineSegment(sketch, "E1427", {"start": v(-5.65, 1.7) * mm, "end": v(-5.63, 1.69) * mm});
            skLineSegment(sketch, "E1428", {"start": v(-5.63, 1.69) * mm, "end": v(-5.63, 1.69) * mm});
            skLineSegment(sketch, "E1429", {"start": v(-5.63, 1.69) * mm, "end": v(-4.6, 1.38) * mm});
            skLineSegment(sketch, "E1430", {"start": v(-4.6, 1.38) * mm, "end": v(-4.81, 0) * mm});
            skLineSegment(sketch, "E1431", {"start": v(-4.81, 0) * mm, "end": v(-5.87, 0) * mm});
            skLineSegment(sketch, "E1432", {"start": v(-5.87, 0) * mm, "end": v(-5.88, 0) * mm});
            skLineSegment(sketch, "E1433", {"start": v(-5.88, 0) * mm, "end": v(-5.9, 0) * mm});
            skLineSegment(sketch, "E1434", {"start": v(-5.9, 0) * mm, "end": v(-5.92, 0) * mm});
            skLineSegment(sketch, "E1435", {"start": v(-5.92, 0) * mm, "end": v(-5.95, 0) * mm});
            skLineSegment(sketch, "E1436", {"start": v(-5.95, 0) * mm, "end": v(-5.98, -0.01) * mm});
            skLineSegment(sketch, "E1437", {"start": v(-5.98, -0.01) * mm, "end": v(-6.02, -0.02) * mm});
            skLineSegment(sketch, "E1438", {"start": v(-6.02, -0.02) * mm, "end": v(-6.07, -0.03) * mm});
            skLineSegment(sketch, "E1439", {"start": v(-6.07, -0.03) * mm, "end": v(-6.13, -0.05) * mm});
            skLineSegment(sketch, "E1440", {"start": v(-6.13, -0.05) * mm, "end": v(-6.19, -0.07) * mm});
            skLineSegment(sketch, "E1441", {"start": v(-6.19, -0.07) * mm, "end": v(-6.25, -0.1) * mm});
            skLineSegment(sketch, "E1442", {"start": v(-6.25, -0.1) * mm, "end": v(-6.33, -0.12) * mm});
            skLineSegment(sketch, "E1443", {"start": v(-6.33, -0.12) * mm, "end": v(-6.4, -0.16) * mm});
            skLineSegment(sketch, "E1444", {"start": v(-6.4, -0.16) * mm, "end": v(-6.49, -0.2) * mm});
            skLineSegment(sketch, "E1445", {"start": v(-6.49, -0.2) * mm, "end": v(-6.58, -0.25) * mm});
            skLineSegment(sketch, "E1446", {"start": v(-6.58, -0.25) * mm, "end": v(-6.67, -0.3) * mm});
            skLineSegment(sketch, "E1447", {"start": v(-6.67, -0.3) * mm, "end": v(-6.77, -0.36) * mm});
            skLineSegment(sketch, "E1448", {"start": v(-6.77, -0.36) * mm, "end": v(-6.87, -0.43) * mm});
            skLineSegment(sketch, "E1449", {"start": v(-6.87, -0.43) * mm, "end": v(-6.97, -0.5) * mm});
            skLineSegment(sketch, "E1450", {"start": v(-6.97, -0.5) * mm, "end": v(-7.08, -0.59) * mm});
            skLineSegment(sketch, "E1451", {"start": v(-7.08, -0.59) * mm, "end": v(-7.19, -0.68) * mm});
            skLineSegment(sketch, "E1452", {"start": v(-7.19, -0.68) * mm, "end": v(-7.3, -0.78) * mm});
            skLineSegment(sketch, "E1453", {"start": v(-7.3, -0.78) * mm, "end": v(-7.41, -0.9) * mm});
            skLineSegment(sketch, "E1454", {"start": v(-7.41, -0.9) * mm, "end": v(-7.43, -1) * mm});
            skLineSegment(sketch, "E1455", {"start": v(-7.43, -1) * mm, "end": v(-7.34, -1.52) * mm});
            skLineSegment(sketch, "E1456", {"start": v(-7.34, -1.52) * mm, "end": v(-7.3, -1.61) * mm});
            skLineSegment(sketch, "E1457", {"start": v(-7.3, -1.61) * mm, "end": v(-7.15, -1.68) * mm});
            skLineSegment(sketch, "E1458", {"start": v(-7.15, -1.68) * mm, "end": v(-7.01, -1.73) * mm});
            skLineSegment(sketch, "E1459", {"start": v(-7.01, -1.73) * mm, "end": v(-6.88, -1.78) * mm});
            skLineSegment(sketch, "E1460", {"start": v(-6.88, -1.78) * mm, "end": v(-6.75, -1.83) * mm});
            skLineSegment(sketch, "E1461", {"start": v(-6.75, -1.83) * mm, "end": v(-6.62, -1.87) * mm});
            skLineSegment(sketch, "E1462", {"start": v(-6.62, -1.87) * mm, "end": v(-6.5, -1.9) * mm});
            skLineSegment(sketch, "E1463", {"start": v(-6.5, -1.9) * mm, "end": v(-6.4, -1.92) * mm});
            skLineSegment(sketch, "E1464", {"start": v(-6.4, -1.92) * mm, "end": v(-6.29, -1.94) * mm});
            skLineSegment(sketch, "E1465", {"start": v(-6.29, -1.94) * mm, "end": v(-6.2, -1.96) * mm});
            skLineSegment(sketch, "E1466", {"start": v(-6.2, -1.96) * mm, "end": v(-6.1, -1.97) * mm});
            skLineSegment(sketch, "E1467", {"start": v(-6.1, -1.97) * mm, "end": v(-6.01, -1.97) * mm});
            skLineSegment(sketch, "E1468", {"start": v(-6.01, -1.97) * mm, "end": v(-5.93, -1.98) * mm});
            skLineSegment(sketch, "E1469", {"start": v(-5.93, -1.98) * mm, "end": v(-5.86, -1.98) * mm});
            skLineSegment(sketch, "E1470", {"start": v(-5.86, -1.98) * mm, "end": v(-5.8, -1.98) * mm});
            skLineSegment(sketch, "E1471", {"start": v(-5.8, -1.98) * mm, "end": v(-5.74, -1.97) * mm});
            skLineSegment(sketch, "E1472", {"start": v(-5.74, -1.97) * mm, "end": v(-5.7, -1.97) * mm});
            skLineSegment(sketch, "E1473", {"start": v(-5.7, -1.97) * mm, "end": v(-5.65, -1.96) * mm});
            skLineSegment(sketch, "E1474", {"start": v(-5.65, -1.96) * mm, "end": v(-5.61, -1.96) * mm});
            skLineSegment(sketch, "E1475", {"start": v(-5.61, -1.96) * mm, "end": v(-5.59, -1.95) * mm});
            skLineSegment(sketch, "E1476", {"start": v(-5.59, -1.95) * mm, "end": v(-5.56, -1.95) * mm});
            skLineSegment(sketch, "E1477", {"start": v(-5.56, -1.95) * mm, "end": v(-5.55, -1.94) * mm});
            skLineSegment(sketch, "E1478", {"start": v(-5.55, -1.94) * mm, "end": v(-5.54, -1.94) * mm});
            skLineSegment(sketch, "E1479", {"start": v(-5.54, -1.94) * mm, "end": v(-4.54, -1.6) * mm});
            skLineSegment(sketch, "E1480", {"start": v(-4.54, -1.6) * mm, "end": v(-3.9, -2.83) * mm});
            skLineSegment(sketch, "E1481", {"start": v(-3.9, -2.83) * mm, "end": v(-4.75, -3.45) * mm});
            skLineSegment(sketch, "E1482", {"start": v(-4.75, -3.45) * mm, "end": v(-4.76, -3.46) * mm});
            skLineSegment(sketch, "E1483", {"start": v(-4.76, -3.46) * mm, "end": v(-4.77, -3.47) * mm});
            skLineSegment(sketch, "E1484", {"start": v(-4.77, -3.47) * mm, "end": v(-4.78, -3.48) * mm});
            skLineSegment(sketch, "E1485", {"start": v(-4.78, -3.48) * mm, "end": v(-4.8, -3.5) * mm});
            skLineSegment(sketch, "E1486", {"start": v(-4.8, -3.5) * mm, "end": v(-4.83, -3.53) * mm});
            skLineSegment(sketch, "E1487", {"start": v(-4.83, -3.53) * mm, "end": v(-4.86, -3.56) * mm});
            skLineSegment(sketch, "E1488", {"start": v(-4.86, -3.56) * mm, "end": v(-4.9, -3.6) * mm});
            skLineSegment(sketch, "E1489", {"start": v(-4.9, -3.6) * mm, "end": v(-4.93, -3.64) * mm});
            skLineSegment(sketch, "E1490", {"start": v(-4.93, -3.64) * mm, "end": v(-4.96, -3.7) * mm});
            skLineSegment(sketch, "E1491", {"start": v(-4.96, -3.7) * mm, "end": v(-5, -3.75) * mm});
            skLineSegment(sketch, "E1492", {"start": v(-5, -3.75) * mm, "end": v(-5.05, -3.82) * mm});
            skLineSegment(sketch, "E1493", {"start": v(-5.05, -3.82) * mm, "end": v(-5.09, -3.9) * mm});
            skLineSegment(sketch, "E1494", {"start": v(-5.09, -3.9) * mm, "end": v(-5.13, -3.98) * mm});
            skLineSegment(sketch, "E1495", {"start": v(-5.13, -3.98) * mm, "end": v(-5.18, -4.07) * mm});
            skLineSegment(sketch, "E1496", {"start": v(-5.18, -4.07) * mm, "end": v(-5.22, -4.16) * mm});
            skLineSegment(sketch, "E1497", {"start": v(-5.22, -4.16) * mm, "end": v(-5.26, -4.27) * mm});
            skLineSegment(sketch, "E1498", {"start": v(-5.26, -4.27) * mm, "end": v(-5.3, -4.39) * mm});
            skLineSegment(sketch, "E1499", {"start": v(-5.3, -4.39) * mm, "end": v(-5.34, -4.5) * mm});
            skLineSegment(sketch, "E1500", {"start": v(-5.34, -4.5) * mm, "end": v(-5.38, -4.64) * mm});
            skLineSegment(sketch, "E1501", {"start": v(-5.38, -4.64) * mm, "end": v(-5.42, -4.78) * mm});
            skLineSegment(sketch, "E1502", {"start": v(-5.42, -4.78) * mm, "end": v(-5.45, -4.92) * mm});
            skLineSegment(sketch, "E1503", {"start": v(-5.45, -4.92) * mm, "end": v(-5.47, -5.08) * mm});
            skLineSegment(sketch, "E1504", {"start": v(-5.47, -5.08) * mm, "end": v(-5.43, -5.18) * mm});
            skLineSegment(sketch, "E1505", {"start": v(-5.43, -5.18) * mm, "end": v(-5.05, -5.54) * mm});
            skLineSegment(sketch, "E1506", {"start": v(-5.05, -5.54) * mm, "end": v(-4.95, -5.59) * mm});
            skLineSegment(sketch, "E1507", {"start": v(-4.95, -5.59) * mm, "end": v(-4.8, -5.56) * mm});
            skLineSegment(sketch, "E1508", {"start": v(-4.8, -5.56) * mm, "end": v(-4.65, -5.52) * mm});
            skLineSegment(sketch, "E1509", {"start": v(-4.65, -5.52) * mm, "end": v(-4.51, -5.49) * mm});
            skLineSegment(sketch, "E1510", {"start": v(-4.51, -5.49) * mm, "end": v(-4.38, -5.45) * mm});
            skLineSegment(sketch, "E1511", {"start": v(-4.38, -5.45) * mm, "end": v(-4.26, -5.4) * mm});
            skLineSegment(sketch, "E1512", {"start": v(-4.26, -5.4) * mm, "end": v(-4.15, -5.36) * mm});
            skLineSegment(sketch, "E1513", {"start": v(-4.15, -5.36) * mm, "end": v(-4.04, -5.31) * mm});
            skLineSegment(sketch, "E1514", {"start": v(-4.04, -5.31) * mm, "end": v(-3.95, -5.27) * mm});
            skLineSegment(sketch, "E1515", {"start": v(-3.95, -5.27) * mm, "end": v(-3.86, -5.22) * mm});
            skLineSegment(sketch, "E1516", {"start": v(-3.86, -5.22) * mm, "end": v(-3.78, -5.18) * mm});
            skLineSegment(sketch, "E1517", {"start": v(-3.78, -5.18) * mm, "end": v(-3.7, -5.13) * mm});
            skLineSegment(sketch, "E1518", {"start": v(-3.7, -5.13) * mm, "end": v(-3.64, -5.09) * mm});
            skLineSegment(sketch, "E1519", {"start": v(-3.64, -5.09) * mm, "end": v(-3.58, -5.05) * mm});
            skLineSegment(sketch, "E1520", {"start": v(-3.58, -5.05) * mm, "end": v(-3.53, -5) * mm});
            skLineSegment(sketch, "E1521", {"start": v(-3.53, -5) * mm, "end": v(-3.48, -4.97) * mm});
            skLineSegment(sketch, "E1522", {"start": v(-3.48, -4.97) * mm, "end": v(-3.45, -4.94) * mm});
            skLineSegment(sketch, "E1523", {"start": v(-3.45, -4.94) * mm, "end": v(-3.42, -4.9) * mm});
            skLineSegment(sketch, "E1524", {"start": v(-3.42, -4.9) * mm, "end": v(-3.39, -4.88) * mm});
            skLineSegment(sketch, "E1525", {"start": v(-3.39, -4.88) * mm, "end": v(-3.37, -4.86) * mm});
            skLineSegment(sketch, "E1526", {"start": v(-3.37, -4.86) * mm, "end": v(-3.36, -4.85) * mm});
            skLineSegment(sketch, "E1527", {"start": v(-3.36, -4.85) * mm, "end": v(-3.35, -4.84) * mm});
            skLineSegment(sketch, "E1528", {"start": v(-3.35, -4.84) * mm, "end": v(-3.34, -4.83) * mm});
            skLineSegment(sketch, "E1529", {"start": v(-3.34, -4.83) * mm, "end": v(-2.74, -3.96) * mm});
            skLineSegment(sketch, "E1530", {"start": v(-2.74, -3.96) * mm, "end": v(-1.49, -4.58) * mm});
            skLineSegment(sketch, "E1531", {"start": v(-1.49, -4.58) * mm, "end": v(-1.82, -5.59) * mm});
            skLineSegment(sketch, "E1532", {"start": v(-1.82, -5.59) * mm, "end": v(-1.82, -5.6) * mm});
            skLineSegment(sketch, "E1533", {"start": v(-1.82, -5.6) * mm, "end": v(-1.82, -5.6) * mm});
            skLineSegment(sketch, "E1534", {"start": v(-1.82, -5.6) * mm, "end": v(-1.82, -5.63) * mm});
            skLineSegment(sketch, "E1535", {"start": v(-1.82, -5.63) * mm, "end": v(-1.83, -5.66) * mm});
            skLineSegment(sketch, "E1536", {"start": v(-1.83, -5.66) * mm, "end": v(-1.83, -5.7) * mm});
            skLineSegment(sketch, "E1537", {"start": v(-1.83, -5.7) * mm, "end": v(-1.84, -5.73) * mm});
            skLineSegment(sketch, "E1538", {"start": v(-1.84, -5.73) * mm, "end": v(-1.84, -5.78) * mm});
            skLineSegment(sketch, "E1539", {"start": v(-1.84, -5.78) * mm, "end": v(-1.84, -5.84) * mm});
            skLineSegment(sketch, "E1540", {"start": v(-1.84, -5.84) * mm, "end": v(-1.84, -5.9) * mm});
            skLineSegment(sketch, "E1541", {"start": v(-1.84, -5.9) * mm, "end": v(-1.84, -5.98) * mm});
            skLineSegment(sketch, "E1542", {"start": v(-1.84, -5.98) * mm, "end": v(-1.84, -6.06) * mm});
            skLineSegment(sketch, "E1543", {"start": v(-1.84, -6.06) * mm, "end": v(-1.83, -6.14) * mm});
            skLineSegment(sketch, "E1544", {"start": v(-1.83, -6.14) * mm, "end": v(-1.81, -6.23) * mm});
            skLineSegment(sketch, "E1545", {"start": v(-1.81, -6.23) * mm, "end": v(-1.8, -6.33) * mm});
            skLineSegment(sketch, "E1546", {"start": v(-1.8, -6.33) * mm, "end": v(-1.78, -6.44) * mm});
            skLineSegment(sketch, "E1547", {"start": v(-1.78, -6.44) * mm, "end": v(-1.75, -6.55) * mm});
            skLineSegment(sketch, "E1548", {"start": v(-1.75, -6.55) * mm, "end": v(-1.71, -6.67) * mm});
            skLineSegment(sketch, "E1549", {"start": v(-1.71, -6.67) * mm, "end": v(-1.67, -6.79) * mm});
            skLineSegment(sketch, "E1550", {"start": v(-1.67, -6.79) * mm, "end": v(-1.63, -6.92) * mm});
            skLineSegment(sketch, "E1551", {"start": v(-1.63, -6.92) * mm, "end": v(-1.57, -7.05) * mm});
            skLineSegment(sketch, "E1552", {"start": v(-1.57, -7.05) * mm, "end": v(-1.51, -7.19) * mm});
            skLineSegment(sketch, "E1553", {"start": v(-1.51, -7.19) * mm, "end": v(-1.44, -7.33) * mm});
            skLineSegment(sketch, "E1554", {"start": v(-1.44, -7.33) * mm, "end": v(-1.35, -7.38) * mm});
            skLineSegment(sketch, "E1555", {"start": v(-1.35, -7.38) * mm, "end": v(-0.83, -7.45) * mm});
            skLineSegment(sketch, "E1556", {"start": v(-0.83, -7.45) * mm, "end": v(-0.72, -7.43) * mm});
            skLineSegment(sketch, "E1557", {"start": v(-0.72, -7.43) * mm, "end": v(-0.62, -7.32) * mm});
            skLineSegment(sketch, "E1558", {"start": v(-0.62, -7.32) * mm, "end": v(-0.52, -7.2) * mm});
            skLineSegment(sketch, "E1559", {"start": v(-0.52, -7.2) * mm, "end": v(-0.43, -7.1) * mm});
            skLineSegment(sketch, "E1560", {"start": v(-0.43, -7.1) * mm, "end": v(-0.35, -6.98) * mm});
            skLineSegment(sketch, "E1561", {"start": v(-0.35, -6.98) * mm, "end": v(-0.27, -6.88) * mm});
            skLineSegment(sketch, "E1562", {"start": v(-0.27, -6.88) * mm, "end": v(-0.2, -6.77) * mm});
            skLineSegment(sketch, "E1563", {"start": v(-0.2, -6.77) * mm, "end": v(-0.15, -6.68) * mm});
            skLineSegment(sketch, "E1564", {"start": v(-0.15, -6.68) * mm, "end": v(-0.1, -6.58) * mm});
            skLineSegment(sketch, "E1565", {"start": v(-0.1, -6.58) * mm, "end": v(-0.05, -6.5) * mm});
            skLineSegment(sketch, "E1566", {"start": v(-0.05, -6.5) * mm, "end": v(-0.01, -6.4) * mm});
            skLineSegment(sketch, "E1567", {"start": v(-0.01, -6.4) * mm, "end": v(0.02, -6.33) * mm});
            skLineSegment(sketch, "E1568", {"start": v(0.02, -6.33) * mm, "end": v(0.05, -6.25) * mm});
            skLineSegment(sketch, "E1569", {"start": v(0.05, -6.25) * mm, "end": v(0.07, -6.19) * mm});
            skLineSegment(sketch, "E1570", {"start": v(0.07, -6.19) * mm, "end": v(0.09, -6.13) * mm});
            skLineSegment(sketch, "E1571", {"start": v(0.09, -6.13) * mm, "end": v(0.1, -6.07) * mm});
            skLineSegment(sketch, "E1572", {"start": v(0.1, -6.07) * mm, "end": v(0.11, -6.02) * mm});
            skLineSegment(sketch, "E1573", {"start": v(0.11, -6.02) * mm, "end": v(0.12, -5.98) * mm});
            skLineSegment(sketch, "E1574", {"start": v(0.12, -5.98) * mm, "end": v(0.13, -5.94) * mm});
            skLineSegment(sketch, "E1575", {"start": v(0.13, -5.94) * mm, "end": v(0.13, -5.92) * mm});
            skLineSegment(sketch, "E1576", {"start": v(0.13, -5.92) * mm, "end": v(0.13, -5.9) * mm});
            skLineSegment(sketch, "E1577", {"start": v(0.13, -5.9) * mm, "end": v(0.13, -5.88) * mm});
            skLineSegment(sketch, "E1578", {"start": v(0.13, -5.88) * mm, "end": v(0.13, -5.87) * mm});
            skLineSegment(sketch, "E1579", {"start": v(0.13, -5.87) * mm, "end": v(0.1, -4.81) * mm});
            skLineSegment(sketch, "E1580", {"start": v(0.1, -4.81) * mm, "end": v(1.49, -4.58) * mm});
            skLineSegment(sketch, "E1581", {"start": v(1.49, -4.58) * mm, "end": v(1.82, -5.59) * mm});
            skLineSegment(sketch, "E1582", {"start": v(1.82, -5.59) * mm, "end": v(1.82, -5.6) * mm});
            skLineSegment(sketch, "E1583", {"start": v(1.82, -5.6) * mm, "end": v(1.82, -5.6) * mm});
            skLineSegment(sketch, "E1584", {"start": v(1.82, -5.6) * mm, "end": v(1.83, -5.63) * mm});
            skLineSegment(sketch, "E1585", {"start": v(1.83, -5.63) * mm, "end": v(1.84, -5.65) * mm});
            skLineSegment(sketch, "E1586", {"start": v(1.84, -5.65) * mm, "end": v(1.86, -5.68) * mm});
            skLineSegment(sketch, "E1587", {"start": v(1.86, -5.68) * mm, "end": v(1.88, -5.72) * mm});
            skLineSegment(sketch, "E1588", {"start": v(1.88, -5.72) * mm, "end": v(1.9, -5.76) * mm});
            skLineSegment(sketch, "E1589", {"start": v(1.9, -5.76) * mm, "end": v(1.94, -5.81) * mm});
            skLineSegment(sketch, "E1590", {"start": v(1.94, -5.81) * mm, "end": v(1.98, -5.86) * mm});
            skLineSegment(sketch, "E1591", {"start": v(1.98, -5.86) * mm, "end": v(2.02, -5.92) * mm});
            skLineSegment(sketch, "E1592", {"start": v(2.02, -5.92) * mm, "end": v(2.07, -5.98) * mm});
            skLineSegment(sketch, "E1593", {"start": v(2.07, -5.98) * mm, "end": v(2.13, -6.04) * mm});
            skLineSegment(sketch, "E1594", {"start": v(2.13, -6.04) * mm, "end": v(2.2, -6.1) * mm});
            skLineSegment(sketch, "E1595", {"start": v(2.2, -6.1) * mm, "end": v(2.27, -6.18) * mm});
            skLineSegment(sketch, "E1596", {"start": v(2.27, -6.18) * mm, "end": v(2.35, -6.25) * mm});
            skLineSegment(sketch, "E1597", {"start": v(2.35, -6.25) * mm, "end": v(2.44, -6.32) * mm});
            skLineSegment(sketch, "E1598", {"start": v(2.44, -6.32) * mm, "end": v(2.53, -6.4) * mm});
            skLineSegment(sketch, "E1599", {"start": v(2.53, -6.4) * mm, "end": v(2.64, -6.48) * mm});
            skLineSegment(sketch, "E1600", {"start": v(2.64, -6.48) * mm, "end": v(2.75, -6.55) * mm});
            skLineSegment(sketch, "E1601", {"start": v(2.75, -6.55) * mm, "end": v(2.87, -6.63) * mm});
            skLineSegment(sketch, "E1602", {"start": v(2.87, -6.63) * mm, "end": v(3, -6.7) * mm});
            skLineSegment(sketch, "E1603", {"start": v(3, -6.7) * mm, "end": v(3.14, -6.78) * mm});
            skLineSegment(sketch, "E1604", {"start": v(3.14, -6.78) * mm, "end": v(3.25, -6.76) * mm});
            skLineSegment(sketch, "E1605", {"start": v(3.25, -6.76) * mm, "end": v(3.71, -6.52) * mm});
            skLineSegment(sketch, "E1606", {"start": v(3.71, -6.52) * mm, "end": v(3.79, -6.44) * mm});
            skLineSegment(sketch, "E1607", {"start": v(3.79, -6.44) * mm, "end": v(3.8, -6.28) * mm});
            skLineSegment(sketch, "E1608", {"start": v(3.8, -6.28) * mm, "end": v(3.82, -6.13) * mm});
            skLineSegment(sketch, "E1609", {"start": v(3.82, -6.13) * mm, "end": v(3.82, -5.99) * mm});
            skLineSegment(sketch, "E1610", {"start": v(3.82, -5.99) * mm, "end": v(3.82, -5.85) * mm});
            skLineSegment(sketch, "E1611", {"start": v(3.82, -5.85) * mm, "end": v(3.82, -5.72) * mm});
            skLineSegment(sketch, "E1612", {"start": v(3.82, -5.72) * mm, "end": v(3.81, -5.6) * mm});
            skLineSegment(sketch, "E1613", {"start": v(3.81, -5.6) * mm, "end": v(3.8, -5.49) * mm});
            skLineSegment(sketch, "E1614", {"start": v(3.8, -5.49) * mm, "end": v(3.8, -5.38) * mm});
            skLineSegment(sketch, "E1615", {"start": v(3.8, -5.38) * mm, "end": v(3.77, -5.28) * mm});
            skLineSegment(sketch, "E1616", {"start": v(3.77, -5.28) * mm, "end": v(3.76, -5.2) * mm});
            skLineSegment(sketch, "E1617", {"start": v(3.76, -5.2) * mm, "end": v(3.74, -5.1) * mm});
            skLineSegment(sketch, "E1618", {"start": v(3.74, -5.1) * mm, "end": v(3.72, -5.03) * mm});
            skLineSegment(sketch, "E1619", {"start": v(3.72, -5.03) * mm, "end": v(3.7, -4.96) * mm});
            skLineSegment(sketch, "E1620", {"start": v(3.7, -4.96) * mm, "end": v(3.67, -4.9) * mm});
            skLineSegment(sketch, "E1621", {"start": v(3.67, -4.9) * mm, "end": v(3.65, -4.85) * mm});
            skLineSegment(sketch, "E1622", {"start": v(3.65, -4.85) * mm, "end": v(3.63, -4.8) * mm});
            skLineSegment(sketch, "E1623", {"start": v(3.63, -4.8) * mm, "end": v(3.61, -4.77) * mm});
            skLineSegment(sketch, "E1624", {"start": v(3.61, -4.77) * mm, "end": v(3.6, -4.73) * mm});
            skLineSegment(sketch, "E1625", {"start": v(3.6, -4.73) * mm, "end": v(3.58, -4.7) * mm});
            skLineSegment(sketch, "E1626", {"start": v(3.58, -4.7) * mm, "end": v(3.57, -4.69) * mm});
            skLineSegment(sketch, "E1627", {"start": v(3.57, -4.69) * mm, "end": v(3.56, -4.68) * mm});
            skLineSegment(sketch, "E1628", {"start": v(3.56, -4.68) * mm, "end": v(3.56, -4.67) * mm});
            skLineSegment(sketch, "E1629", {"start": v(3.56, -4.67) * mm, "end": v(2.92, -3.83) * mm});
            skLineSegment(sketch, "E1630", {"start": v(2.92, -3.83) * mm, "end": v(3.9, -2.83) * mm});
            skLineSegment(sketch, "E1631", {"start": v(3.9, -2.83) * mm, "end": v(4.75, -3.45) * mm});
            skLineSegment(sketch, "E1632", {"start": v(4.75, -3.45) * mm, "end": v(4.76, -3.46) * mm});
            skLineSegment(sketch, "E1633", {"start": v(4.76, -3.46) * mm, "end": v(4.77, -3.46) * mm});
            skLineSegment(sketch, "E1634", {"start": v(4.77, -3.46) * mm, "end": v(4.79, -3.47) * mm});
            skLineSegment(sketch, "E1635", {"start": v(4.79, -3.47) * mm, "end": v(4.81, -3.49) * mm});
            skLineSegment(sketch, "E1636", {"start": v(4.81, -3.49) * mm, "end": v(4.85, -3.5) * mm});
            skLineSegment(sketch, "E1637", {"start": v(4.85, -3.5) * mm, "end": v(4.89, -3.52) * mm});
            skLineSegment(sketch, "E1638", {"start": v(4.89, -3.52) * mm, "end": v(4.93, -3.54) * mm});
            skLineSegment(sketch, "E1639", {"start": v(4.93, -3.54) * mm, "end": v(4.99, -3.56) * mm});
            skLineSegment(sketch, "E1640", {"start": v(4.99, -3.56) * mm, "end": v(5.05, -3.58) * mm});
            skLineSegment(sketch, "E1641", {"start": v(5.05, -3.58) * mm, "end": v(5.12, -3.6) * mm});
            skLineSegment(sketch, "E1642", {"start": v(5.12, -3.6) * mm, "end": v(5.2, -3.62) * mm});
            skLineSegment(sketch, "E1643", {"start": v(5.2, -3.62) * mm, "end": v(5.28, -3.64) * mm});
            skLineSegment(sketch, "E1644", {"start": v(5.28, -3.64) * mm, "end": v(5.37, -3.65) * mm});
            skLineSegment(sketch, "E1645", {"start": v(5.37, -3.65) * mm, "end": v(5.47, -3.67) * mm});
            skLineSegment(sketch, "E1646", {"start": v(5.47, -3.67) * mm, "end": v(5.57, -3.68) * mm});
            skLineSegment(sketch, "E1647", {"start": v(5.57, -3.68) * mm, "end": v(5.69, -3.69) * mm});
            skLineSegment(sketch, "E1648", {"start": v(5.69, -3.69) * mm, "end": v(5.8, -3.69) * mm});
            skLineSegment(sketch, "E1649", {"start": v(5.8, -3.69) * mm, "end": v(5.94, -3.69) * mm});
            skLineSegment(sketch, "E1650", {"start": v(5.94, -3.69) * mm, "end": v(6.07, -3.68) * mm});
            skLineSegment(sketch, "E1651", {"start": v(6.07, -3.68) * mm, "end": v(6.22, -3.67) * mm});
            skLineSegment(sketch, "E1652", {"start": v(6.22, -3.67) * mm, "end": v(6.37, -3.66) * mm});
            skLineSegment(sketch, "E1653", {"start": v(6.37, -3.66) * mm, "end": v(6.52, -3.64) * mm});
            skLineSegment(sketch, "E1654", {"start": v(6.52, -3.64) * mm, "end": v(6.6, -3.56) * mm});
            skLineSegment(sketch, "E1655", {"start": v(6.6, -3.56) * mm, "end": v(6.83, -3.09) * mm});
            skLineSegment(sketch, "E1656", {"start": v(6.83, -3.09) * mm, "end": v(6.85, -2.98) * mm});
            skLineSegment(sketch, "E1657", {"start": v(6.85, -2.98) * mm, "end": v(6.77, -2.85) * mm});
            skLineSegment(sketch, "E1658", {"start": v(6.77, -2.85) * mm, "end": v(6.7, -2.72) * mm});
            skLineSegment(sketch, "E1659", {"start": v(6.7, -2.72) * mm, "end": v(6.61, -2.6) * mm});
            skLineSegment(sketch, "E1660", {"start": v(6.61, -2.6) * mm, "end": v(6.53, -2.49) * mm});
            skLineSegment(sketch, "E1661", {"start": v(6.53, -2.49) * mm, "end": v(6.46, -2.38) * mm});
            skLineSegment(sketch, "E1662", {"start": v(6.46, -2.38) * mm, "end": v(6.38, -2.3) * mm});
            skLineSegment(sketch, "E1663", {"start": v(6.38, -2.3) * mm, "end": v(6.3, -2.2) * mm});
            skLineSegment(sketch, "E1664", {"start": v(6.3, -2.2) * mm, "end": v(6.23, -2.13) * mm});
            skLineSegment(sketch, "E1665", {"start": v(6.23, -2.13) * mm, "end": v(6.16, -2.06) * mm});
            skLineSegment(sketch, "E1666", {"start": v(6.16, -2.06) * mm, "end": v(6.1, -2) * mm});
            skLineSegment(sketch, "E1667", {"start": v(6.1, -2) * mm, "end": v(6.02, -1.94) * mm});
            skLineSegment(sketch, "E1668", {"start": v(6.02, -1.94) * mm, "end": v(5.96, -1.89) * mm});
            skLineSegment(sketch, "E1669", {"start": v(5.96, -1.89) * mm, "end": v(5.9, -1.84) * mm});
            skLineSegment(sketch, "E1670", {"start": v(5.9, -1.84) * mm, "end": v(5.85, -1.8) * mm});
            skLineSegment(sketch, "E1671", {"start": v(5.85, -1.8) * mm, "end": v(5.8, -1.78) * mm});
            skLineSegment(sketch, "E1672", {"start": v(5.8, -1.78) * mm, "end": v(5.76, -1.75) * mm});
            skLineSegment(sketch, "E1673", {"start": v(5.76, -1.75) * mm, "end": v(5.72, -1.73) * mm});
            skLineSegment(sketch, "E1674", {"start": v(5.72, -1.73) * mm, "end": v(5.7, -1.71) * mm});
            skLineSegment(sketch, "E1675", {"start": v(5.7, -1.71) * mm, "end": v(5.67, -1.7) * mm});
            skLineSegment(sketch, "E1676", {"start": v(5.67, -1.7) * mm, "end": v(5.65, -1.7) * mm});
            skLineSegment(sketch, "E1677", {"start": v(5.65, -1.7) * mm, "end": v(5.63, -1.69) * mm});
            skLineSegment(sketch, "E1678", {"start": v(5.63, -1.69) * mm, "end": v(5.63, -1.69) * mm});
            skLineSegment(sketch, "E1679", {"start": v(5.63, -1.69) * mm, "end": v(4.6, -1.38) * mm});
            skLineSegment(sketch, "E1680", {"start": v(4.6, -1.38) * mm, "end": v(4.81, 0) * mm});
            skSolve(sketch);
        }
        {
            var Q0;
            Q0 = qSketchRegion(id + "F4", true);
            extrude(context, id + "F5", {"entities" : qUnion([Q0]), "operationType" : NewBodyOperationType.ADD, "depth" : 10 * mm});
        }
        {
            var Q0;
            Q0=qCreatedBy(makeId("Top.planeOp"),FACE);
            var sketch = newSketch(context, id + "F6", { "sketchPlane" : qUnion([Q0])});
            skCircle(sketch, "E1681", {"center": v(0, 0) * mm, "radius": 3 * mm});
            skSolve(sketch);
        }
        {
            var Q0;
            Q0 = qSketchRegion(id + "F6", true);
            extrude(context, id + "F7", {"entities" : qUnion([Q0]), "operationType" : NewBodyOperationType.REMOVE, "endBound" : BoundingType.THROUGH_ALL, "depth" : 25 * mm});
        }
    });
